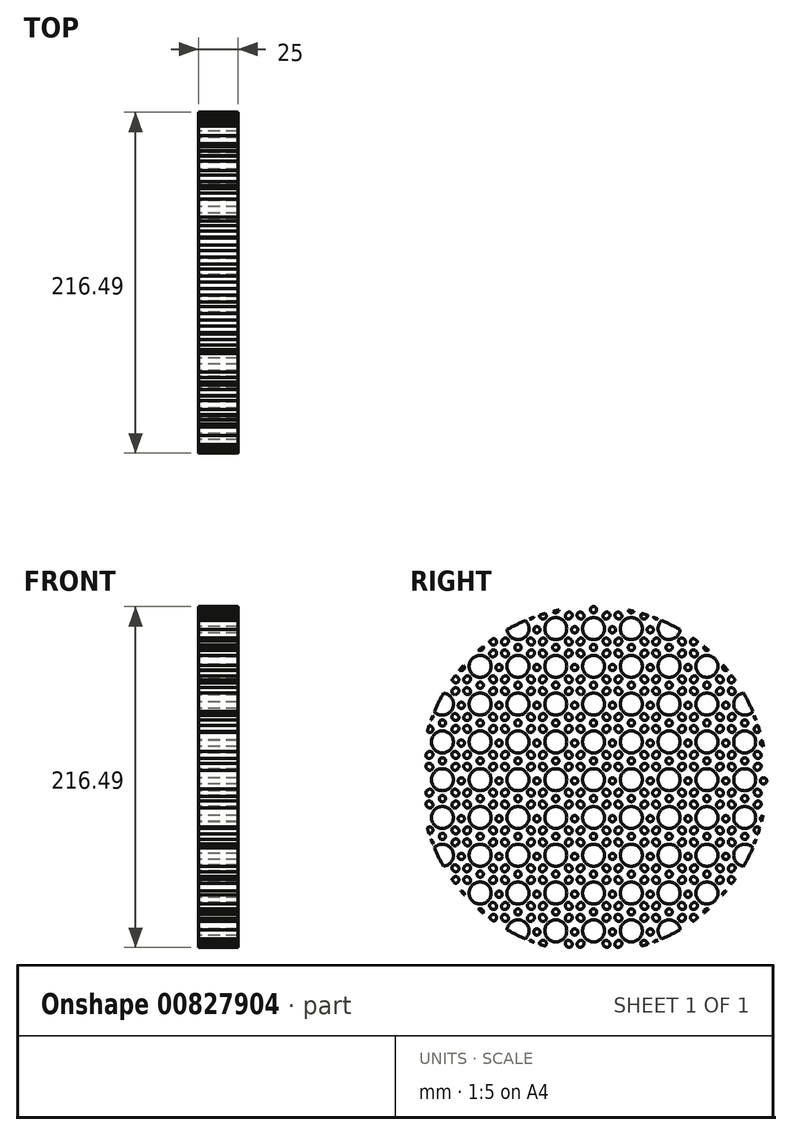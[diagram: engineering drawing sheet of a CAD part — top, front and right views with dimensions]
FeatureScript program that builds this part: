
annotation { "Feature Type Name" : "Feature", "Feature Type Description" : "" }
export const myFeature = defineFeature(function(context is Context, id is Id, definition is map)
    precondition{}
    {
        {
            var Q0;
            Q0=qCreatedBy(makeId("Right.planeOp"),FACE);
            var sketch = newSketch(context, id + "F0", { "sketchPlane" : qUnion([Q0])});
            skCircle(sketch, "E0.0", {"center": v(0, 0) * mm, "radius": 7 * mm});
            skArc(sketch, "E1.0", {"start": v(6.59, 9.41) * mm, "mid": v(6.59, 6.59) * mm, "end": v(9.41, 6.59) * mm});
            skArc(sketch, "E2.0", {"start": v(9.9, 7.07) * mm, "mid": v(9.9, 9.9) * mm, "end": v(7.07, 9.9) * mm});
            skCircle(sketch, "E3.0", {"center": v(0, 12) * mm, "radius": 2 * mm});
            skArc(sketch, "E4.0.0", {"start": v(-9.9, 7.07) * mm, "mid": v(-9.9, 9.9) * mm, "end": v(-7.07, 9.9) * mm});
            skArc(sketch, "E5.0", {"start": v(-9.41, 6.59) * mm, "mid": v(-6.59, 6.59) * mm, "end": v(-6.59, 9.41) * mm});
            skArc(sketch, "E6.0", {"start": v(-9.9, -7.07) * mm, "mid": v(-9.9, -9.9) * mm, "end": v(-7.07, -9.9) * mm});
            skArc(sketch, "E7.0", {"start": v(-6.59, -9.41) * mm, "mid": v(-6.59, -6.59) * mm, "end": v(-9.41, -6.59) * mm});
            skArc(sketch, "E8.0", {"start": v(9.41, -6.59) * mm, "mid": v(6.59, -6.59) * mm, "end": v(6.59, -9.41) * mm});
            skArc(sketch, "E9.0", {"start": v(7.07, -9.9) * mm, "mid": v(9.9, -9.9) * mm, "end": v(9.9, -7.07) * mm});
            skLineSegment(sketch, "E10", {"start": v(7.07, 9.9) * mm, "end": v(6.59, 9.41) * mm});
            skLineSegment(sketch, "E11", {"start": v(9.9, 7.07) * mm, "end": v(9.41, 6.59) * mm});
            skLineSegment(sketch, "E12", {"start": v(-7.07, 9.9) * mm, "end": v(-6.59, 9.41) * mm});
            skLineSegment(sketch, "E13", {"start": v(-9.9, 7.07) * mm, "end": v(-9.41, 6.59) * mm});
            skLineSegment(sketch, "E14", {"start": v(-9.41, -6.59) * mm, "end": v(-9.9, -7.07) * mm});
            skLineSegment(sketch, "E15", {"start": v(-7.07, -9.9) * mm, "end": v(-6.59, -9.41) * mm});
            skLineSegment(sketch, "E16", {"start": v(9.41, -6.59) * mm, "end": v(9.9, -7.07) * mm});
            skLineSegment(sketch, "E17", {"start": v(7.07, -9.9) * mm, "end": v(6.59, -9.41) * mm});
            skCircle(sketch, "E18", {"center": v(12, -0.75) * mm, "radius": 2 * mm});
            skCircle(sketch, "E19.0.1.0", {"center": v(12, 23.25) * mm, "radius": 2 * mm});
            skArc(sketch, "E19.0.1.1", {"start": v(9.41, 17.41) * mm, "mid": v(6.59, 17.41) * mm, "end": v(6.59, 14.59) * mm});
            skArc(sketch, "E19.0.1.2", {"start": v(-9.9, 31.07) * mm, "mid": v(-9.9, 33.9) * mm, "end": v(-7.07, 33.9) * mm});
            skArc(sketch, "E19.0.1.3", {"start": v(-6.59, 14.59) * mm, "mid": v(-6.59, 17.41) * mm, "end": v(-9.41, 17.41) * mm});
            skCircle(sketch, "E19.0.1.4", {"center": v(0, 36) * mm, "radius": 2 * mm});
            skArc(sketch, "E19.0.1.5", {"start": v(6.59, 33.41) * mm, "mid": v(6.59, 30.59) * mm, "end": v(9.41, 30.59) * mm});
            skArc(sketch, "E19.0.1.6", {"start": v(-9.41, 30.59) * mm, "mid": v(-6.59, 30.59) * mm, "end": v(-6.59, 33.41) * mm});
            skCircle(sketch, "E19.0.1.7", {"center": v(0, 24) * mm, "radius": 7 * mm});
            skArc(sketch, "E19.0.1.8", {"start": v(9.9, 31.07) * mm, "mid": v(9.9, 33.9) * mm, "end": v(7.07, 33.9) * mm});
            skArc(sketch, "E19.0.1.9", {"start": v(7.07, 14.1) * mm, "mid": v(9.9, 14.1) * mm, "end": v(9.9, 16.93) * mm});
            skArc(sketch, "E19.0.1.10", {"start": v(-9.9, 16.93) * mm, "mid": v(-9.9, 14.1) * mm, "end": v(-7.07, 14.1) * mm});
            skLineSegment(sketch, "E19.0.1.11", {"start": v(7.07, 14.1) * mm, "end": v(6.59, 14.59) * mm});
            skLineSegment(sketch, "E19.0.1.12", {"start": v(-7.07, 33.9) * mm, "end": v(-6.59, 33.41) * mm});
            skLineSegment(sketch, "E19.0.1.13", {"start": v(9.9, 31.07) * mm, "end": v(9.41, 30.59) * mm});
            skLineSegment(sketch, "E19.0.1.14", {"start": v(9.41, 17.41) * mm, "end": v(9.9, 16.93) * mm});
            skLineSegment(sketch, "E19.0.1.15", {"start": v(7.07, 33.9) * mm, "end": v(6.59, 33.41) * mm});
            skLineSegment(sketch, "E19.0.1.16", {"start": v(-9.9, 31.07) * mm, "end": v(-9.41, 30.59) * mm});
            skLineSegment(sketch, "E19.0.1.17", {"start": v(-9.41, 17.41) * mm, "end": v(-9.9, 16.93) * mm});
            skLineSegment(sketch, "E19.0.1.18", {"start": v(-7.07, 14.1) * mm, "end": v(-6.59, 14.59) * mm});
            skCircle(sketch, "E19.0.2.0", {"center": v(12, 47.25) * mm, "radius": 2 * mm});
            skArc(sketch, "E19.0.2.1", {"start": v(9.41, 41.41) * mm, "mid": v(6.59, 41.41) * mm, "end": v(6.59, 38.59) * mm});
            skArc(sketch, "E19.0.2.2", {"start": v(-9.9, 55.07) * mm, "mid": v(-9.9, 57.9) * mm, "end": v(-7.07, 57.9) * mm});
            skArc(sketch, "E19.0.2.3", {"start": v(-6.59, 38.59) * mm, "mid": v(-6.59, 41.41) * mm, "end": v(-9.41, 41.41) * mm});
            skCircle(sketch, "E19.0.2.4", {"center": v(0, 60) * mm, "radius": 2 * mm});
            skArc(sketch, "E19.0.2.5", {"start": v(6.59, 57.41) * mm, "mid": v(6.59, 54.59) * mm, "end": v(9.41, 54.59) * mm});
            skArc(sketch, "E19.0.2.6", {"start": v(-9.41, 54.59) * mm, "mid": v(-6.59, 54.59) * mm, "end": v(-6.59, 57.41) * mm});
            skCircle(sketch, "E19.0.2.7", {"center": v(0, 48) * mm, "radius": 7 * mm});
            skArc(sketch, "E19.0.2.8", {"start": v(9.9, 55.07) * mm, "mid": v(9.9, 57.9) * mm, "end": v(7.07, 57.9) * mm});
            skArc(sketch, "E19.0.2.9", {"start": v(7.07, 38.1) * mm, "mid": v(9.9, 38.1) * mm, "end": v(9.9, 40.93) * mm});
            skArc(sketch, "E19.0.2.10", {"start": v(-9.9, 40.93) * mm, "mid": v(-9.9, 38.1) * mm, "end": v(-7.07, 38.1) * mm});
            skLineSegment(sketch, "E19.0.2.11", {"start": v(7.07, 38.1) * mm, "end": v(6.59, 38.59) * mm});
            skLineSegment(sketch, "E19.0.2.12", {"start": v(-7.07, 57.9) * mm, "end": v(-6.59, 57.41) * mm});
            skLineSegment(sketch, "E19.0.2.13", {"start": v(9.9, 55.07) * mm, "end": v(9.41, 54.59) * mm});
            skLineSegment(sketch, "E19.0.2.14", {"start": v(9.41, 41.41) * mm, "end": v(9.9, 40.93) * mm});
            skLineSegment(sketch, "E19.0.2.15", {"start": v(7.07, 57.9) * mm, "end": v(6.59, 57.41) * mm});
            skLineSegment(sketch, "E19.0.2.16", {"start": v(-9.9, 55.07) * mm, "end": v(-9.41, 54.59) * mm});
            skLineSegment(sketch, "E19.0.2.17", {"start": v(-9.41, 41.41) * mm, "end": v(-9.9, 40.93) * mm});
            skLineSegment(sketch, "E19.0.2.18", {"start": v(-7.07, 38.1) * mm, "end": v(-6.59, 38.59) * mm});
            skCircle(sketch, "E19.0.3.0", {"center": v(12, 71.25) * mm, "radius": 2 * mm});
            skArc(sketch, "E19.0.3.1", {"start": v(9.41, 65.41) * mm, "mid": v(6.59, 65.41) * mm, "end": v(6.59, 62.59) * mm});
            skArc(sketch, "E19.0.3.2", {"start": v(-9.9, 79.07) * mm, "mid": v(-9.9, 81.9) * mm, "end": v(-7.07, 81.9) * mm});
            skArc(sketch, "E19.0.3.3", {"start": v(-6.59, 62.59) * mm, "mid": v(-6.59, 65.41) * mm, "end": v(-9.41, 65.41) * mm});
            skCircle(sketch, "E19.0.3.4", {"center": v(0, 84) * mm, "radius": 2 * mm});
            skArc(sketch, "E19.0.3.5", {"start": v(6.59, 81.41) * mm, "mid": v(6.59, 78.59) * mm, "end": v(9.41, 78.59) * mm});
            skArc(sketch, "E19.0.3.6", {"start": v(-9.41, 78.59) * mm, "mid": v(-6.59, 78.59) * mm, "end": v(-6.59, 81.41) * mm});
            skCircle(sketch, "E19.0.3.7", {"center": v(0, 72) * mm, "radius": 7 * mm});
            skArc(sketch, "E19.0.3.8", {"start": v(9.9, 79.07) * mm, "mid": v(9.9, 81.9) * mm, "end": v(7.07, 81.9) * mm});
            skArc(sketch, "E19.0.3.9", {"start": v(7.07, 62.1) * mm, "mid": v(9.9, 62.1) * mm, "end": v(9.9, 64.93) * mm});
            skArc(sketch, "E19.0.3.10", {"start": v(-9.9, 64.93) * mm, "mid": v(-9.9, 62.1) * mm, "end": v(-7.07, 62.1) * mm});
            skLineSegment(sketch, "E19.0.3.11", {"start": v(7.07, 62.1) * mm, "end": v(6.59, 62.59) * mm});
            skLineSegment(sketch, "E19.0.3.12", {"start": v(-7.07, 81.9) * mm, "end": v(-6.59, 81.41) * mm});
            skLineSegment(sketch, "E19.0.3.13", {"start": v(9.9, 79.07) * mm, "end": v(9.41, 78.59) * mm});
            skLineSegment(sketch, "E19.0.3.14", {"start": v(9.41, 65.41) * mm, "end": v(9.9, 64.93) * mm});
            skLineSegment(sketch, "E19.0.3.15", {"start": v(7.07, 81.9) * mm, "end": v(6.59, 81.41) * mm});
            skLineSegment(sketch, "E19.0.3.16", {"start": v(-9.9, 79.07) * mm, "end": v(-9.41, 78.59) * mm});
            skLineSegment(sketch, "E19.0.3.17", {"start": v(-9.41, 65.41) * mm, "end": v(-9.9, 64.93) * mm});
            skLineSegment(sketch, "E19.0.3.18", {"start": v(-7.07, 62.1) * mm, "end": v(-6.59, 62.59) * mm});
            skCircle(sketch, "E19.0.4.0", {"center": v(12, 95.25) * mm, "radius": 2 * mm});
            skArc(sketch, "E19.0.4.1", {"start": v(9.41, 89.41) * mm, "mid": v(6.59, 89.41) * mm, "end": v(6.59, 86.59) * mm});
            skArc(sketch, "E19.0.4.2", {"start": v(-9.9, 103.07) * mm, "mid": v(-9.9, 105.9) * mm, "end": v(-7.07, 105.9) * mm});
            skArc(sketch, "E19.0.4.3", {"start": v(-6.59, 86.59) * mm, "mid": v(-6.59, 89.41) * mm, "end": v(-9.41, 89.41) * mm});
            skCircle(sketch, "E19.0.4.4", {"center": v(0, 108) * mm, "radius": 2 * mm});
            skArc(sketch, "E19.0.4.5", {"start": v(6.59, 105.41) * mm, "mid": v(6.59, 102.59) * mm, "end": v(9.41, 102.59) * mm});
            skArc(sketch, "E19.0.4.6", {"start": v(-9.41, 102.59) * mm, "mid": v(-6.59, 102.59) * mm, "end": v(-6.59, 105.41) * mm});
            skCircle(sketch, "E19.0.4.7", {"center": v(0, 96) * mm, "radius": 7 * mm});
            skArc(sketch, "E19.0.4.8", {"start": v(9.9, 103.07) * mm, "mid": v(9.9, 105.9) * mm, "end": v(7.07, 105.9) * mm});
            skArc(sketch, "E19.0.4.9", {"start": v(7.07, 86.1) * mm, "mid": v(9.9, 86.1) * mm, "end": v(9.9, 88.93) * mm});
            skArc(sketch, "E19.0.4.10", {"start": v(-9.9, 88.93) * mm, "mid": v(-9.9, 86.1) * mm, "end": v(-7.07, 86.1) * mm});
            skLineSegment(sketch, "E19.0.4.11", {"start": v(7.07, 86.1) * mm, "end": v(6.59, 86.59) * mm});
            skLineSegment(sketch, "E19.0.4.12", {"start": v(-7.07, 105.9) * mm, "end": v(-6.59, 105.41) * mm});
            skLineSegment(sketch, "E19.0.4.13", {"start": v(9.9, 103.07) * mm, "end": v(9.41, 102.59) * mm});
            skLineSegment(sketch, "E19.0.4.14", {"start": v(9.41, 89.41) * mm, "end": v(9.9, 88.93) * mm});
            skLineSegment(sketch, "E19.0.4.15", {"start": v(7.07, 105.9) * mm, "end": v(6.59, 105.41) * mm});
            skLineSegment(sketch, "E19.0.4.16", {"start": v(-9.9, 103.07) * mm, "end": v(-9.41, 102.59) * mm});
            skLineSegment(sketch, "E19.0.4.17", {"start": v(-9.41, 89.41) * mm, "end": v(-9.9, 88.93) * mm});
            skLineSegment(sketch, "E19.0.4.18", {"start": v(-7.07, 86.1) * mm, "end": v(-6.59, 86.59) * mm});
            skCircle(sketch, "E19.0.5.0", {"center": v(12, 119.25) * mm, "radius": 2 * mm});
            skArc(sketch, "E19.0.5.1", {"start": v(9.41, 113.41) * mm, "mid": v(6.59, 113.41) * mm, "end": v(6.59, 110.59) * mm});
            skArc(sketch, "E19.0.5.2", {"start": v(-9.9, 127.07) * mm, "mid": v(-9.9, 129.9) * mm, "end": v(-7.07, 129.9) * mm});
            skArc(sketch, "E19.0.5.3", {"start": v(-6.59, 110.59) * mm, "mid": v(-6.59, 113.41) * mm, "end": v(-9.41, 113.41) * mm});
            skCircle(sketch, "E19.0.5.4", {"center": v(0, 132) * mm, "radius": 2 * mm});
            skArc(sketch, "E19.0.5.5", {"start": v(6.59, 129.41) * mm, "mid": v(6.59, 126.59) * mm, "end": v(9.41, 126.59) * mm});
            skArc(sketch, "E19.0.5.6", {"start": v(-9.41, 126.59) * mm, "mid": v(-6.59, 126.59) * mm, "end": v(-6.59, 129.41) * mm});
            skCircle(sketch, "E19.0.5.7", {"center": v(0, 120) * mm, "radius": 7 * mm});
            skArc(sketch, "E19.0.5.8", {"start": v(9.9, 127.07) * mm, "mid": v(9.9, 129.9) * mm, "end": v(7.07, 129.9) * mm});
            skArc(sketch, "E19.0.5.9", {"start": v(7.07, 110.1) * mm, "mid": v(9.9, 110.1) * mm, "end": v(9.9, 112.93) * mm});
            skArc(sketch, "E19.0.5.10", {"start": v(-9.9, 112.93) * mm, "mid": v(-9.9, 110.1) * mm, "end": v(-7.07, 110.1) * mm});
            skLineSegment(sketch, "E19.0.5.11", {"start": v(7.07, 110.1) * mm, "end": v(6.59, 110.59) * mm});
            skLineSegment(sketch, "E19.0.5.12", {"start": v(-7.07, 129.9) * mm, "end": v(-6.59, 129.41) * mm});
            skLineSegment(sketch, "E19.0.5.13", {"start": v(9.9, 127.07) * mm, "end": v(9.41, 126.59) * mm});
            skLineSegment(sketch, "E19.0.5.14", {"start": v(9.41, 113.41) * mm, "end": v(9.9, 112.93) * mm});
            skLineSegment(sketch, "E19.0.5.15", {"start": v(7.07, 129.9) * mm, "end": v(6.59, 129.41) * mm});
            skLineSegment(sketch, "E19.0.5.16", {"start": v(-9.9, 127.07) * mm, "end": v(-9.41, 126.59) * mm});
            skLineSegment(sketch, "E19.0.5.17", {"start": v(-9.41, 113.41) * mm, "end": v(-9.9, 112.93) * mm});
            skLineSegment(sketch, "E19.0.5.18", {"start": v(-7.07, 110.1) * mm, "end": v(-6.59, 110.59) * mm});
            skCircle(sketch, "E19.0.6.0", {"center": v(12, 143.25) * mm, "radius": 2 * mm});
            skArc(sketch, "E19.0.6.1", {"start": v(9.41, 137.41) * mm, "mid": v(6.59, 137.41) * mm, "end": v(6.59, 134.59) * mm});
            skArc(sketch, "E19.0.6.2", {"start": v(-9.9, 151.07) * mm, "mid": v(-9.9, 153.9) * mm, "end": v(-7.07, 153.9) * mm});
            skArc(sketch, "E19.0.6.3", {"start": v(-6.59, 134.59) * mm, "mid": v(-6.59, 137.41) * mm, "end": v(-9.41, 137.41) * mm});
            skCircle(sketch, "E19.0.6.4", {"center": v(0, 156) * mm, "radius": 2 * mm});
            skArc(sketch, "E19.0.6.5", {"start": v(6.59, 153.41) * mm, "mid": v(6.59, 150.59) * mm, "end": v(9.41, 150.59) * mm});
            skArc(sketch, "E19.0.6.6", {"start": v(-9.41, 150.59) * mm, "mid": v(-6.59, 150.59) * mm, "end": v(-6.59, 153.41) * mm});
            skCircle(sketch, "E19.0.6.7", {"center": v(0, 144) * mm, "radius": 7 * mm});
            skArc(sketch, "E19.0.6.8", {"start": v(9.9, 151.07) * mm, "mid": v(9.9, 153.9) * mm, "end": v(7.07, 153.9) * mm});
            skArc(sketch, "E19.0.6.9", {"start": v(7.07, 134.1) * mm, "mid": v(9.9, 134.1) * mm, "end": v(9.9, 136.93) * mm});
            skArc(sketch, "E19.0.6.10", {"start": v(-9.9, 136.93) * mm, "mid": v(-9.9, 134.1) * mm, "end": v(-7.07, 134.1) * mm});
            skLineSegment(sketch, "E19.0.6.11", {"start": v(7.07, 134.1) * mm, "end": v(6.59, 134.59) * mm});
            skLineSegment(sketch, "E19.0.6.12", {"start": v(-7.07, 153.9) * mm, "end": v(-6.59, 153.41) * mm});
            skLineSegment(sketch, "E19.0.6.13", {"start": v(9.9, 151.07) * mm, "end": v(9.41, 150.59) * mm});
            skLineSegment(sketch, "E19.0.6.14", {"start": v(9.41, 137.41) * mm, "end": v(9.9, 136.93) * mm});
            skLineSegment(sketch, "E19.0.6.15", {"start": v(7.07, 153.9) * mm, "end": v(6.59, 153.41) * mm});
            skLineSegment(sketch, "E19.0.6.16", {"start": v(-9.9, 151.07) * mm, "end": v(-9.41, 150.59) * mm});
            skLineSegment(sketch, "E19.0.6.17", {"start": v(-9.41, 137.41) * mm, "end": v(-9.9, 136.93) * mm});
            skLineSegment(sketch, "E19.0.6.18", {"start": v(-7.07, 134.1) * mm, "end": v(-6.59, 134.59) * mm});
            skCircle(sketch, "E19.0.7.0", {"center": v(12, 167.25) * mm, "radius": 2 * mm});
            skArc(sketch, "E19.0.7.1", {"start": v(9.41, 161.41) * mm, "mid": v(6.59, 161.41) * mm, "end": v(6.59, 158.59) * mm});
            skArc(sketch, "E19.0.7.2", {"start": v(-9.9, 175.07) * mm, "mid": v(-9.9, 177.9) * mm, "end": v(-7.07, 177.9) * mm});
            skArc(sketch, "E19.0.7.3", {"start": v(-6.59, 158.59) * mm, "mid": v(-6.59, 161.41) * mm, "end": v(-9.41, 161.41) * mm});
            skCircle(sketch, "E19.0.7.4", {"center": v(0, 180) * mm, "radius": 2 * mm});
            skArc(sketch, "E19.0.7.5", {"start": v(6.59, 177.41) * mm, "mid": v(6.59, 174.59) * mm, "end": v(9.41, 174.59) * mm});
            skArc(sketch, "E19.0.7.6", {"start": v(-9.41, 174.59) * mm, "mid": v(-6.59, 174.59) * mm, "end": v(-6.59, 177.41) * mm});
            skCircle(sketch, "E19.0.7.7", {"center": v(0, 168) * mm, "radius": 7 * mm});
            skArc(sketch, "E19.0.7.8", {"start": v(9.9, 175.07) * mm, "mid": v(9.9, 177.9) * mm, "end": v(7.07, 177.9) * mm});
            skArc(sketch, "E19.0.7.9", {"start": v(7.07, 158.1) * mm, "mid": v(9.9, 158.1) * mm, "end": v(9.9, 160.93) * mm});
            skArc(sketch, "E19.0.7.10", {"start": v(-9.9, 160.93) * mm, "mid": v(-9.9, 158.1) * mm, "end": v(-7.07, 158.1) * mm});
            skLineSegment(sketch, "E19.0.7.11", {"start": v(7.07, 158.1) * mm, "end": v(6.59, 158.59) * mm});
            skLineSegment(sketch, "E19.0.7.12", {"start": v(-7.07, 177.9) * mm, "end": v(-6.59, 177.41) * mm});
            skLineSegment(sketch, "E19.0.7.13", {"start": v(9.9, 175.07) * mm, "end": v(9.41, 174.59) * mm});
            skLineSegment(sketch, "E19.0.7.14", {"start": v(9.41, 161.41) * mm, "end": v(9.9, 160.93) * mm});
            skLineSegment(sketch, "E19.0.7.15", {"start": v(7.07, 177.9) * mm, "end": v(6.59, 177.41) * mm});
            skLineSegment(sketch, "E19.0.7.16", {"start": v(-9.9, 175.07) * mm, "end": v(-9.41, 174.59) * mm});
            skLineSegment(sketch, "E19.0.7.17", {"start": v(-9.41, 161.41) * mm, "end": v(-9.9, 160.93) * mm});
            skLineSegment(sketch, "E19.0.7.18", {"start": v(-7.07, 158.1) * mm, "end": v(-6.59, 158.59) * mm});
            skCircle(sketch, "E19.0.8.0", {"center": v(12, 191.25) * mm, "radius": 2 * mm});
            skArc(sketch, "E19.0.8.1", {"start": v(9.41, 185.41) * mm, "mid": v(6.59, 185.41) * mm, "end": v(6.59, 182.59) * mm});
            skArc(sketch, "E19.0.8.2", {"start": v(-9.9, 199.07) * mm, "mid": v(-9.9, 201.9) * mm, "end": v(-7.07, 201.9) * mm});
            skArc(sketch, "E19.0.8.3", {"start": v(-6.59, 182.59) * mm, "mid": v(-6.59, 185.41) * mm, "end": v(-9.41, 185.41) * mm});
            skCircle(sketch, "E19.0.8.4", {"center": v(0, 204) * mm, "radius": 2 * mm});
            skArc(sketch, "E19.0.8.5", {"start": v(6.59, 201.41) * mm, "mid": v(6.59, 198.59) * mm, "end": v(9.41, 198.59) * mm});
            skArc(sketch, "E19.0.8.6", {"start": v(-9.41, 198.59) * mm, "mid": v(-6.59, 198.59) * mm, "end": v(-6.59, 201.41) * mm});
            skCircle(sketch, "E19.0.8.7", {"center": v(0, 192) * mm, "radius": 7 * mm});
            skArc(sketch, "E19.0.8.8", {"start": v(9.9, 199.07) * mm, "mid": v(9.9, 201.9) * mm, "end": v(7.07, 201.9) * mm});
            skArc(sketch, "E19.0.8.9", {"start": v(7.07, 182.1) * mm, "mid": v(9.9, 182.1) * mm, "end": v(9.9, 184.93) * mm});
            skArc(sketch, "E19.0.8.10", {"start": v(-9.9, 184.93) * mm, "mid": v(-9.9, 182.1) * mm, "end": v(-7.07, 182.1) * mm});
            skLineSegment(sketch, "E19.0.8.11", {"start": v(7.07, 182.1) * mm, "end": v(6.59, 182.59) * mm});
            skLineSegment(sketch, "E19.0.8.12", {"start": v(-7.07, 201.9) * mm, "end": v(-6.59, 201.41) * mm});
            skLineSegment(sketch, "E19.0.8.13", {"start": v(9.9, 199.07) * mm, "end": v(9.41, 198.59) * mm});
            skLineSegment(sketch, "E19.0.8.14", {"start": v(9.41, 185.41) * mm, "end": v(9.9, 184.93) * mm});
            skLineSegment(sketch, "E19.0.8.15", {"start": v(7.07, 201.9) * mm, "end": v(6.59, 201.41) * mm});
            skLineSegment(sketch, "E19.0.8.16", {"start": v(-9.9, 199.07) * mm, "end": v(-9.41, 198.59) * mm});
            skLineSegment(sketch, "E19.0.8.17", {"start": v(-9.41, 185.41) * mm, "end": v(-9.9, 184.93) * mm});
            skLineSegment(sketch, "E19.0.8.18", {"start": v(-7.07, 182.1) * mm, "end": v(-6.59, 182.59) * mm});
            skCircle(sketch, "E19.1.0.0", {"center": v(36, -0.75) * mm, "radius": 2 * mm});
            skArc(sketch, "E19.1.0.1", {"start": v(33.41, -6.59) * mm, "mid": v(30.59, -6.59) * mm, "end": v(30.59, -9.41) * mm});
            skArc(sketch, "E19.1.0.2", {"start": v(14.1, 7.07) * mm, "mid": v(14.1, 9.9) * mm, "end": v(16.93, 9.9) * mm});
            skArc(sketch, "E19.1.0.3", {"start": v(17.41, -9.41) * mm, "mid": v(17.41, -6.59) * mm, "end": v(14.59, -6.59) * mm});
            skCircle(sketch, "E19.1.0.4", {"center": v(24, 12) * mm, "radius": 2 * mm});
            skArc(sketch, "E19.1.0.5", {"start": v(30.59, 9.41) * mm, "mid": v(30.59, 6.59) * mm, "end": v(33.41, 6.59) * mm});
            skArc(sketch, "E19.1.0.6", {"start": v(14.59, 6.59) * mm, "mid": v(17.41, 6.59) * mm, "end": v(17.41, 9.41) * mm});
            skCircle(sketch, "E19.1.0.7", {"center": v(24, 0) * mm, "radius": 7 * mm});
            skArc(sketch, "E19.1.0.8", {"start": v(33.9, 7.07) * mm, "mid": v(33.9, 9.9) * mm, "end": v(31.07, 9.9) * mm});
            skArc(sketch, "E19.1.0.9", {"start": v(31.07, -9.9) * mm, "mid": v(33.9, -9.9) * mm, "end": v(33.9, -7.07) * mm});
            skArc(sketch, "E19.1.0.10", {"start": v(14.1, -7.07) * mm, "mid": v(14.1, -9.9) * mm, "end": v(16.93, -9.9) * mm});
            skLineSegment(sketch, "E19.1.0.11", {"start": v(31.07, -9.9) * mm, "end": v(30.59, -9.41) * mm});
            skLineSegment(sketch, "E19.1.0.12", {"start": v(16.93, 9.9) * mm, "end": v(17.41, 9.41) * mm});
            skLineSegment(sketch, "E19.1.0.13", {"start": v(33.9, 7.07) * mm, "end": v(33.41, 6.59) * mm});
            skLineSegment(sketch, "E19.1.0.14", {"start": v(33.41, -6.59) * mm, "end": v(33.9, -7.07) * mm});
            skLineSegment(sketch, "E19.1.0.15", {"start": v(31.07, 9.9) * mm, "end": v(30.59, 9.41) * mm});
            skLineSegment(sketch, "E19.1.0.16", {"start": v(14.1, 7.07) * mm, "end": v(14.59, 6.59) * mm});
            skLineSegment(sketch, "E19.1.0.17", {"start": v(14.59, -6.59) * mm, "end": v(14.1, -7.07) * mm});
            skLineSegment(sketch, "E19.1.0.18", {"start": v(16.93, -9.9) * mm, "end": v(17.41, -9.41) * mm});
            skCircle(sketch, "E19.1.1.0", {"center": v(36, 23.25) * mm, "radius": 2 * mm});
            skArc(sketch, "E19.1.1.1", {"start": v(33.41, 17.41) * mm, "mid": v(30.59, 17.41) * mm, "end": v(30.59, 14.59) * mm});
            skArc(sketch, "E19.1.1.2", {"start": v(14.1, 31.07) * mm, "mid": v(14.1, 33.9) * mm, "end": v(16.93, 33.9) * mm});
            skArc(sketch, "E19.1.1.3", {"start": v(17.41, 14.59) * mm, "mid": v(17.41, 17.41) * mm, "end": v(14.59, 17.41) * mm});
            skCircle(sketch, "E19.1.1.4", {"center": v(24, 36) * mm, "radius": 2 * mm});
            skArc(sketch, "E19.1.1.5", {"start": v(30.59, 33.41) * mm, "mid": v(30.59, 30.59) * mm, "end": v(33.41, 30.59) * mm});
            skArc(sketch, "E19.1.1.6", {"start": v(14.59, 30.59) * mm, "mid": v(17.41, 30.59) * mm, "end": v(17.41, 33.41) * mm});
            skCircle(sketch, "E19.1.1.7", {"center": v(24, 24) * mm, "radius": 7 * mm});
            skArc(sketch, "E19.1.1.8", {"start": v(33.9, 31.07) * mm, "mid": v(33.9, 33.9) * mm, "end": v(31.07, 33.9) * mm});
            skArc(sketch, "E19.1.1.9", {"start": v(31.07, 14.1) * mm, "mid": v(33.9, 14.1) * mm, "end": v(33.9, 16.93) * mm});
            skArc(sketch, "E19.1.1.10", {"start": v(14.1, 16.93) * mm, "mid": v(14.1, 14.1) * mm, "end": v(16.93, 14.1) * mm});
            skLineSegment(sketch, "E19.1.1.11", {"start": v(31.07, 14.1) * mm, "end": v(30.59, 14.59) * mm});
            skLineSegment(sketch, "E19.1.1.12", {"start": v(16.93, 33.9) * mm, "end": v(17.41, 33.41) * mm});
            skLineSegment(sketch, "E19.1.1.13", {"start": v(33.9, 31.07) * mm, "end": v(33.41, 30.59) * mm});
            skLineSegment(sketch, "E19.1.1.14", {"start": v(33.41, 17.41) * mm, "end": v(33.9, 16.93) * mm});
            skLineSegment(sketch, "E19.1.1.15", {"start": v(31.07, 33.9) * mm, "end": v(30.59, 33.41) * mm});
            skLineSegment(sketch, "E19.1.1.16", {"start": v(14.1, 31.07) * mm, "end": v(14.59, 30.59) * mm});
            skLineSegment(sketch, "E19.1.1.17", {"start": v(14.59, 17.41) * mm, "end": v(14.1, 16.93) * mm});
            skLineSegment(sketch, "E19.1.1.18", {"start": v(16.93, 14.1) * mm, "end": v(17.41, 14.59) * mm});
            skCircle(sketch, "E19.1.2.0", {"center": v(36, 47.25) * mm, "radius": 2 * mm});
            skArc(sketch, "E19.1.2.1", {"start": v(33.41, 41.41) * mm, "mid": v(30.59, 41.41) * mm, "end": v(30.59, 38.59) * mm});
            skArc(sketch, "E19.1.2.2", {"start": v(14.1, 55.07) * mm, "mid": v(14.1, 57.9) * mm, "end": v(16.93, 57.9) * mm});
            skArc(sketch, "E19.1.2.3", {"start": v(17.41, 38.59) * mm, "mid": v(17.41, 41.41) * mm, "end": v(14.59, 41.41) * mm});
            skCircle(sketch, "E19.1.2.4", {"center": v(24, 60) * mm, "radius": 2 * mm});
            skArc(sketch, "E19.1.2.5", {"start": v(30.59, 57.41) * mm, "mid": v(30.59, 54.59) * mm, "end": v(33.41, 54.59) * mm});
            skArc(sketch, "E19.1.2.6", {"start": v(14.59, 54.59) * mm, "mid": v(17.41, 54.59) * mm, "end": v(17.41, 57.41) * mm});
            skCircle(sketch, "E19.1.2.7", {"center": v(24, 48) * mm, "radius": 7 * mm});
            skArc(sketch, "E19.1.2.8", {"start": v(33.9, 55.07) * mm, "mid": v(33.9, 57.9) * mm, "end": v(31.07, 57.9) * mm});
            skArc(sketch, "E19.1.2.9", {"start": v(31.07, 38.1) * mm, "mid": v(33.9, 38.1) * mm, "end": v(33.9, 40.93) * mm});
            skArc(sketch, "E19.1.2.10", {"start": v(14.1, 40.93) * mm, "mid": v(14.1, 38.1) * mm, "end": v(16.93, 38.1) * mm});
            skLineSegment(sketch, "E19.1.2.11", {"start": v(31.07, 38.1) * mm, "end": v(30.59, 38.59) * mm});
            skLineSegment(sketch, "E19.1.2.12", {"start": v(16.93, 57.9) * mm, "end": v(17.41, 57.41) * mm});
            skLineSegment(sketch, "E19.1.2.13", {"start": v(33.9, 55.07) * mm, "end": v(33.41, 54.59) * mm});
            skLineSegment(sketch, "E19.1.2.14", {"start": v(33.41, 41.41) * mm, "end": v(33.9, 40.93) * mm});
            skLineSegment(sketch, "E19.1.2.15", {"start": v(31.07, 57.9) * mm, "end": v(30.59, 57.41) * mm});
            skLineSegment(sketch, "E19.1.2.16", {"start": v(14.1, 55.07) * mm, "end": v(14.59, 54.59) * mm});
            skLineSegment(sketch, "E19.1.2.17", {"start": v(14.59, 41.41) * mm, "end": v(14.1, 40.93) * mm});
            skLineSegment(sketch, "E19.1.2.18", {"start": v(16.93, 38.1) * mm, "end": v(17.41, 38.59) * mm});
            skCircle(sketch, "E19.1.3.0", {"center": v(36, 71.25) * mm, "radius": 2 * mm});
            skArc(sketch, "E19.1.3.1", {"start": v(33.41, 65.41) * mm, "mid": v(30.59, 65.41) * mm, "end": v(30.59, 62.59) * mm});
            skArc(sketch, "E19.1.3.2", {"start": v(14.1, 79.07) * mm, "mid": v(14.1, 81.9) * mm, "end": v(16.93, 81.9) * mm});
            skArc(sketch, "E19.1.3.3", {"start": v(17.41, 62.59) * mm, "mid": v(17.41, 65.41) * mm, "end": v(14.59, 65.41) * mm});
            skCircle(sketch, "E19.1.3.4", {"center": v(24, 84) * mm, "radius": 2 * mm});
            skArc(sketch, "E19.1.3.5", {"start": v(30.59, 81.41) * mm, "mid": v(30.59, 78.59) * mm, "end": v(33.41, 78.59) * mm});
            skArc(sketch, "E19.1.3.6", {"start": v(14.59, 78.59) * mm, "mid": v(17.41, 78.59) * mm, "end": v(17.41, 81.41) * mm});
            skCircle(sketch, "E19.1.3.7", {"center": v(24, 72) * mm, "radius": 7 * mm});
            skArc(sketch, "E19.1.3.8", {"start": v(33.9, 79.07) * mm, "mid": v(33.9, 81.9) * mm, "end": v(31.07, 81.9) * mm});
            skArc(sketch, "E19.1.3.9", {"start": v(31.07, 62.1) * mm, "mid": v(33.9, 62.1) * mm, "end": v(33.9, 64.93) * mm});
            skArc(sketch, "E19.1.3.10", {"start": v(14.1, 64.93) * mm, "mid": v(14.1, 62.1) * mm, "end": v(16.93, 62.1) * mm});
            skLineSegment(sketch, "E19.1.3.11", {"start": v(31.07, 62.1) * mm, "end": v(30.59, 62.59) * mm});
            skLineSegment(sketch, "E19.1.3.12", {"start": v(16.93, 81.9) * mm, "end": v(17.41, 81.41) * mm});
            skLineSegment(sketch, "E19.1.3.13", {"start": v(33.9, 79.07) * mm, "end": v(33.41, 78.59) * mm});
            skLineSegment(sketch, "E19.1.3.14", {"start": v(33.41, 65.41) * mm, "end": v(33.9, 64.93) * mm});
            skLineSegment(sketch, "E19.1.3.15", {"start": v(31.07, 81.9) * mm, "end": v(30.59, 81.41) * mm});
            skLineSegment(sketch, "E19.1.3.16", {"start": v(14.1, 79.07) * mm, "end": v(14.59, 78.59) * mm});
            skLineSegment(sketch, "E19.1.3.17", {"start": v(14.59, 65.41) * mm, "end": v(14.1, 64.93) * mm});
            skLineSegment(sketch, "E19.1.3.18", {"start": v(16.93, 62.1) * mm, "end": v(17.41, 62.59) * mm});
            skCircle(sketch, "E19.1.4.0", {"center": v(36, 95.25) * mm, "radius": 2 * mm});
            skArc(sketch, "E19.1.4.1", {"start": v(33.41, 89.41) * mm, "mid": v(30.59, 89.41) * mm, "end": v(30.59, 86.59) * mm});
            skArc(sketch, "E19.1.4.2", {"start": v(14.1, 103.07) * mm, "mid": v(14.1, 105.9) * mm, "end": v(16.93, 105.9) * mm});
            skArc(sketch, "E19.1.4.3", {"start": v(17.41, 86.59) * mm, "mid": v(17.41, 89.41) * mm, "end": v(14.59, 89.41) * mm});
            skCircle(sketch, "E19.1.4.4", {"center": v(24, 108) * mm, "radius": 2 * mm});
            skArc(sketch, "E19.1.4.5", {"start": v(30.59, 105.41) * mm, "mid": v(30.59, 102.59) * mm, "end": v(33.41, 102.59) * mm});
            skArc(sketch, "E19.1.4.6", {"start": v(14.59, 102.59) * mm, "mid": v(17.41, 102.59) * mm, "end": v(17.41, 105.41) * mm});
            skCircle(sketch, "E19.1.4.7", {"center": v(24, 96) * mm, "radius": 7 * mm});
            skArc(sketch, "E19.1.4.8", {"start": v(33.9, 103.07) * mm, "mid": v(33.9, 105.9) * mm, "end": v(31.07, 105.9) * mm});
            skArc(sketch, "E19.1.4.9", {"start": v(31.07, 86.1) * mm, "mid": v(33.9, 86.1) * mm, "end": v(33.9, 88.93) * mm});
            skArc(sketch, "E19.1.4.10", {"start": v(14.1, 88.93) * mm, "mid": v(14.1, 86.1) * mm, "end": v(16.93, 86.1) * mm});
            skLineSegment(sketch, "E19.1.4.11", {"start": v(31.07, 86.1) * mm, "end": v(30.59, 86.59) * mm});
            skLineSegment(sketch, "E19.1.4.12", {"start": v(16.93, 105.9) * mm, "end": v(17.41, 105.41) * mm});
            skLineSegment(sketch, "E19.1.4.13", {"start": v(33.9, 103.07) * mm, "end": v(33.41, 102.59) * mm});
            skLineSegment(sketch, "E19.1.4.14", {"start": v(33.41, 89.41) * mm, "end": v(33.9, 88.93) * mm});
            skLineSegment(sketch, "E19.1.4.15", {"start": v(31.07, 105.9) * mm, "end": v(30.59, 105.41) * mm});
            skLineSegment(sketch, "E19.1.4.16", {"start": v(14.1, 103.07) * mm, "end": v(14.59, 102.59) * mm});
            skLineSegment(sketch, "E19.1.4.17", {"start": v(14.59, 89.41) * mm, "end": v(14.1, 88.93) * mm});
            skLineSegment(sketch, "E19.1.4.18", {"start": v(16.93, 86.1) * mm, "end": v(17.41, 86.59) * mm});
            skCircle(sketch, "E19.1.5.0", {"center": v(36, 119.25) * mm, "radius": 2 * mm});
            skArc(sketch, "E19.1.5.1", {"start": v(33.41, 113.41) * mm, "mid": v(30.59, 113.41) * mm, "end": v(30.59, 110.59) * mm});
            skArc(sketch, "E19.1.5.2", {"start": v(14.1, 127.07) * mm, "mid": v(14.1, 129.9) * mm, "end": v(16.93, 129.9) * mm});
            skArc(sketch, "E19.1.5.3", {"start": v(17.41, 110.59) * mm, "mid": v(17.41, 113.41) * mm, "end": v(14.59, 113.41) * mm});
            skCircle(sketch, "E19.1.5.4", {"center": v(24, 132) * mm, "radius": 2 * mm});
            skArc(sketch, "E19.1.5.5", {"start": v(30.59, 129.41) * mm, "mid": v(30.59, 126.59) * mm, "end": v(33.41, 126.59) * mm});
            skArc(sketch, "E19.1.5.6", {"start": v(14.59, 126.59) * mm, "mid": v(17.41, 126.59) * mm, "end": v(17.41, 129.41) * mm});
            skCircle(sketch, "E19.1.5.7", {"center": v(24, 120) * mm, "radius": 7 * mm});
            skArc(sketch, "E19.1.5.8", {"start": v(33.9, 127.07) * mm, "mid": v(33.9, 129.9) * mm, "end": v(31.07, 129.9) * mm});
            skArc(sketch, "E19.1.5.9", {"start": v(31.07, 110.1) * mm, "mid": v(33.9, 110.1) * mm, "end": v(33.9, 112.93) * mm});
            skArc(sketch, "E19.1.5.10", {"start": v(14.1, 112.93) * mm, "mid": v(14.1, 110.1) * mm, "end": v(16.93, 110.1) * mm});
            skLineSegment(sketch, "E19.1.5.11", {"start": v(31.07, 110.1) * mm, "end": v(30.59, 110.59) * mm});
            skLineSegment(sketch, "E19.1.5.12", {"start": v(16.93, 129.9) * mm, "end": v(17.41, 129.41) * mm});
            skLineSegment(sketch, "E19.1.5.13", {"start": v(33.9, 127.07) * mm, "end": v(33.41, 126.59) * mm});
            skLineSegment(sketch, "E19.1.5.14", {"start": v(33.41, 113.41) * mm, "end": v(33.9, 112.93) * mm});
            skLineSegment(sketch, "E19.1.5.15", {"start": v(31.07, 129.9) * mm, "end": v(30.59, 129.41) * mm});
            skLineSegment(sketch, "E19.1.5.16", {"start": v(14.1, 127.07) * mm, "end": v(14.59, 126.59) * mm});
            skLineSegment(sketch, "E19.1.5.17", {"start": v(14.59, 113.41) * mm, "end": v(14.1, 112.93) * mm});
            skLineSegment(sketch, "E19.1.5.18", {"start": v(16.93, 110.1) * mm, "end": v(17.41, 110.59) * mm});
            skCircle(sketch, "E19.1.6.0", {"center": v(36, 143.25) * mm, "radius": 2 * mm});
            skArc(sketch, "E19.1.6.1", {"start": v(33.41, 137.41) * mm, "mid": v(30.59, 137.41) * mm, "end": v(30.59, 134.59) * mm});
            skArc(sketch, "E19.1.6.2", {"start": v(14.1, 151.07) * mm, "mid": v(14.1, 153.9) * mm, "end": v(16.93, 153.9) * mm});
            skArc(sketch, "E19.1.6.3", {"start": v(17.41, 134.59) * mm, "mid": v(17.41, 137.41) * mm, "end": v(14.59, 137.41) * mm});
            skCircle(sketch, "E19.1.6.4", {"center": v(24, 156) * mm, "radius": 2 * mm});
            skArc(sketch, "E19.1.6.5", {"start": v(30.59, 153.41) * mm, "mid": v(30.59, 150.59) * mm, "end": v(33.41, 150.59) * mm});
            skArc(sketch, "E19.1.6.6", {"start": v(14.59, 150.59) * mm, "mid": v(17.41, 150.59) * mm, "end": v(17.41, 153.41) * mm});
            skCircle(sketch, "E19.1.6.7", {"center": v(24, 144) * mm, "radius": 7 * mm});
            skArc(sketch, "E19.1.6.8", {"start": v(33.9, 151.07) * mm, "mid": v(33.9, 153.9) * mm, "end": v(31.07, 153.9) * mm});
            skArc(sketch, "E19.1.6.9", {"start": v(31.07, 134.1) * mm, "mid": v(33.9, 134.1) * mm, "end": v(33.9, 136.93) * mm});
            skArc(sketch, "E19.1.6.10", {"start": v(14.1, 136.93) * mm, "mid": v(14.1, 134.1) * mm, "end": v(16.93, 134.1) * mm});
            skLineSegment(sketch, "E19.1.6.11", {"start": v(31.07, 134.1) * mm, "end": v(30.59, 134.59) * mm});
            skLineSegment(sketch, "E19.1.6.12", {"start": v(16.93, 153.9) * mm, "end": v(17.41, 153.41) * mm});
            skLineSegment(sketch, "E19.1.6.13", {"start": v(33.9, 151.07) * mm, "end": v(33.41, 150.59) * mm});
            skLineSegment(sketch, "E19.1.6.14", {"start": v(33.41, 137.41) * mm, "end": v(33.9, 136.93) * mm});
            skLineSegment(sketch, "E19.1.6.15", {"start": v(31.07, 153.9) * mm, "end": v(30.59, 153.41) * mm});
            skLineSegment(sketch, "E19.1.6.16", {"start": v(14.1, 151.07) * mm, "end": v(14.59, 150.59) * mm});
            skLineSegment(sketch, "E19.1.6.17", {"start": v(14.59, 137.41) * mm, "end": v(14.1, 136.93) * mm});
            skLineSegment(sketch, "E19.1.6.18", {"start": v(16.93, 134.1) * mm, "end": v(17.41, 134.59) * mm});
            skCircle(sketch, "E19.1.7.0", {"center": v(36, 167.25) * mm, "radius": 2 * mm});
            skArc(sketch, "E19.1.7.1", {"start": v(33.41, 161.41) * mm, "mid": v(30.59, 161.41) * mm, "end": v(30.59, 158.59) * mm});
            skArc(sketch, "E19.1.7.2", {"start": v(14.1, 175.07) * mm, "mid": v(14.1, 177.9) * mm, "end": v(16.93, 177.9) * mm});
            skArc(sketch, "E19.1.7.3", {"start": v(17.41, 158.59) * mm, "mid": v(17.41, 161.41) * mm, "end": v(14.59, 161.41) * mm});
            skCircle(sketch, "E19.1.7.4", {"center": v(24, 180) * mm, "radius": 2 * mm});
            skArc(sketch, "E19.1.7.5", {"start": v(30.59, 177.41) * mm, "mid": v(30.59, 174.59) * mm, "end": v(33.41, 174.59) * mm});
            skArc(sketch, "E19.1.7.6", {"start": v(14.59, 174.59) * mm, "mid": v(17.41, 174.59) * mm, "end": v(17.41, 177.41) * mm});
            skCircle(sketch, "E19.1.7.7", {"center": v(24, 168) * mm, "radius": 7 * mm});
            skArc(sketch, "E19.1.7.8", {"start": v(33.9, 175.07) * mm, "mid": v(33.9, 177.9) * mm, "end": v(31.07, 177.9) * mm});
            skArc(sketch, "E19.1.7.9", {"start": v(31.07, 158.1) * mm, "mid": v(33.9, 158.1) * mm, "end": v(33.9, 160.93) * mm});
            skArc(sketch, "E19.1.7.10", {"start": v(14.1, 160.93) * mm, "mid": v(14.1, 158.1) * mm, "end": v(16.93, 158.1) * mm});
            skLineSegment(sketch, "E19.1.7.11", {"start": v(31.07, 158.1) * mm, "end": v(30.59, 158.59) * mm});
            skLineSegment(sketch, "E19.1.7.12", {"start": v(16.93, 177.9) * mm, "end": v(17.41, 177.41) * mm});
            skLineSegment(sketch, "E19.1.7.13", {"start": v(33.9, 175.07) * mm, "end": v(33.41, 174.59) * mm});
            skLineSegment(sketch, "E19.1.7.14", {"start": v(33.41, 161.41) * mm, "end": v(33.9, 160.93) * mm});
            skLineSegment(sketch, "E19.1.7.15", {"start": v(31.07, 177.9) * mm, "end": v(30.59, 177.41) * mm});
            skLineSegment(sketch, "E19.1.7.16", {"start": v(14.1, 175.07) * mm, "end": v(14.59, 174.59) * mm});
            skLineSegment(sketch, "E19.1.7.17", {"start": v(14.59, 161.41) * mm, "end": v(14.1, 160.93) * mm});
            skLineSegment(sketch, "E19.1.7.18", {"start": v(16.93, 158.1) * mm, "end": v(17.41, 158.59) * mm});
            skCircle(sketch, "E19.1.8.0", {"center": v(36, 191.25) * mm, "radius": 2 * mm});
            skArc(sketch, "E19.1.8.1", {"start": v(33.41, 185.41) * mm, "mid": v(30.59, 185.41) * mm, "end": v(30.59, 182.59) * mm});
            skArc(sketch, "E19.1.8.2", {"start": v(14.1, 199.07) * mm, "mid": v(14.1, 201.9) * mm, "end": v(16.93, 201.9) * mm});
            skArc(sketch, "E19.1.8.3", {"start": v(17.41, 182.59) * mm, "mid": v(17.41, 185.41) * mm, "end": v(14.59, 185.41) * mm});
            skCircle(sketch, "E19.1.8.4", {"center": v(24, 204) * mm, "radius": 2 * mm});
            skArc(sketch, "E19.1.8.5", {"start": v(30.59, 201.41) * mm, "mid": v(30.59, 198.59) * mm, "end": v(33.41, 198.59) * mm});
            skArc(sketch, "E19.1.8.6", {"start": v(14.59, 198.59) * mm, "mid": v(17.41, 198.59) * mm, "end": v(17.41, 201.41) * mm});
            skCircle(sketch, "E19.1.8.7", {"center": v(24, 192) * mm, "radius": 7 * mm});
            skArc(sketch, "E19.1.8.8", {"start": v(33.9, 199.07) * mm, "mid": v(33.9, 201.9) * mm, "end": v(31.07, 201.9) * mm});
            skArc(sketch, "E19.1.8.9", {"start": v(31.07, 182.1) * mm, "mid": v(33.9, 182.1) * mm, "end": v(33.9, 184.93) * mm});
            skArc(sketch, "E19.1.8.10", {"start": v(14.1, 184.93) * mm, "mid": v(14.1, 182.1) * mm, "end": v(16.93, 182.1) * mm});
            skLineSegment(sketch, "E19.1.8.11", {"start": v(31.07, 182.1) * mm, "end": v(30.59, 182.59) * mm});
            skLineSegment(sketch, "E19.1.8.12", {"start": v(16.93, 201.9) * mm, "end": v(17.41, 201.41) * mm});
            skLineSegment(sketch, "E19.1.8.13", {"start": v(33.9, 199.07) * mm, "end": v(33.41, 198.59) * mm});
            skLineSegment(sketch, "E19.1.8.14", {"start": v(33.41, 185.41) * mm, "end": v(33.9, 184.93) * mm});
            skLineSegment(sketch, "E19.1.8.15", {"start": v(31.07, 201.9) * mm, "end": v(30.59, 201.41) * mm});
            skLineSegment(sketch, "E19.1.8.16", {"start": v(14.1, 199.07) * mm, "end": v(14.59, 198.59) * mm});
            skLineSegment(sketch, "E19.1.8.17", {"start": v(14.59, 185.41) * mm, "end": v(14.1, 184.93) * mm});
            skLineSegment(sketch, "E19.1.8.18", {"start": v(16.93, 182.1) * mm, "end": v(17.41, 182.59) * mm});
            skCircle(sketch, "E19.2.0.0", {"center": v(60, -0.75) * mm, "radius": 2 * mm});
            skArc(sketch, "E19.2.0.1", {"start": v(57.41, -6.59) * mm, "mid": v(54.59, -6.59) * mm, "end": v(54.59, -9.41) * mm});
            skArc(sketch, "E19.2.0.2", {"start": v(38.1, 7.07) * mm, "mid": v(38.1, 9.9) * mm, "end": v(40.93, 9.9) * mm});
            skArc(sketch, "E19.2.0.3", {"start": v(41.41, -9.41) * mm, "mid": v(41.41, -6.59) * mm, "end": v(38.59, -6.59) * mm});
            skCircle(sketch, "E19.2.0.4", {"center": v(48, 12) * mm, "radius": 2 * mm});
            skArc(sketch, "E19.2.0.5", {"start": v(54.59, 9.41) * mm, "mid": v(54.59, 6.59) * mm, "end": v(57.41, 6.59) * mm});
            skArc(sketch, "E19.2.0.6", {"start": v(38.59, 6.59) * mm, "mid": v(41.41, 6.59) * mm, "end": v(41.41, 9.41) * mm});
            skCircle(sketch, "E19.2.0.7", {"center": v(48, 0) * mm, "radius": 7 * mm});
            skArc(sketch, "E19.2.0.8", {"start": v(57.9, 7.07) * mm, "mid": v(57.9, 9.9) * mm, "end": v(55.07, 9.9) * mm});
            skArc(sketch, "E19.2.0.9", {"start": v(55.07, -9.9) * mm, "mid": v(57.9, -9.9) * mm, "end": v(57.9, -7.07) * mm});
            skArc(sketch, "E19.2.0.10", {"start": v(38.1, -7.07) * mm, "mid": v(38.1, -9.9) * mm, "end": v(40.93, -9.9) * mm});
            skLineSegment(sketch, "E19.2.0.11", {"start": v(55.07, -9.9) * mm, "end": v(54.59, -9.41) * mm});
            skLineSegment(sketch, "E19.2.0.12", {"start": v(40.93, 9.9) * mm, "end": v(41.41, 9.41) * mm});
            skLineSegment(sketch, "E19.2.0.13", {"start": v(57.9, 7.07) * mm, "end": v(57.41, 6.59) * mm});
            skLineSegment(sketch, "E19.2.0.14", {"start": v(57.41, -6.59) * mm, "end": v(57.9, -7.07) * mm});
            skLineSegment(sketch, "E19.2.0.15", {"start": v(55.07, 9.9) * mm, "end": v(54.59, 9.41) * mm});
            skLineSegment(sketch, "E19.2.0.16", {"start": v(38.1, 7.07) * mm, "end": v(38.59, 6.59) * mm});
            skLineSegment(sketch, "E19.2.0.17", {"start": v(38.59, -6.59) * mm, "end": v(38.1, -7.07) * mm});
            skLineSegment(sketch, "E19.2.0.18", {"start": v(40.93, -9.9) * mm, "end": v(41.41, -9.41) * mm});
            skCircle(sketch, "E19.2.1.0", {"center": v(60, 23.25) * mm, "radius": 2 * mm});
            skArc(sketch, "E19.2.1.1", {"start": v(57.41, 17.41) * mm, "mid": v(54.59, 17.41) * mm, "end": v(54.59, 14.59) * mm});
            skArc(sketch, "E19.2.1.2", {"start": v(38.1, 31.07) * mm, "mid": v(38.1, 33.9) * mm, "end": v(40.93, 33.9) * mm});
            skArc(sketch, "E19.2.1.3", {"start": v(41.41, 14.59) * mm, "mid": v(41.41, 17.41) * mm, "end": v(38.59, 17.41) * mm});
            skCircle(sketch, "E19.2.1.4", {"center": v(48, 36) * mm, "radius": 2 * mm});
            skArc(sketch, "E19.2.1.5", {"start": v(54.59, 33.41) * mm, "mid": v(54.59, 30.59) * mm, "end": v(57.41, 30.59) * mm});
            skArc(sketch, "E19.2.1.6", {"start": v(38.59, 30.59) * mm, "mid": v(41.41, 30.59) * mm, "end": v(41.41, 33.41) * mm});
            skCircle(sketch, "E19.2.1.7", {"center": v(48, 24) * mm, "radius": 7 * mm});
            skArc(sketch, "E19.2.1.8", {"start": v(57.9, 31.07) * mm, "mid": v(57.9, 33.9) * mm, "end": v(55.07, 33.9) * mm});
            skArc(sketch, "E19.2.1.9", {"start": v(55.07, 14.1) * mm, "mid": v(57.9, 14.1) * mm, "end": v(57.9, 16.93) * mm});
            skArc(sketch, "E19.2.1.10", {"start": v(38.1, 16.93) * mm, "mid": v(38.1, 14.1) * mm, "end": v(40.93, 14.1) * mm});
            skLineSegment(sketch, "E19.2.1.11", {"start": v(55.07, 14.1) * mm, "end": v(54.59, 14.59) * mm});
            skLineSegment(sketch, "E19.2.1.12", {"start": v(40.93, 33.9) * mm, "end": v(41.41, 33.41) * mm});
            skLineSegment(sketch, "E19.2.1.13", {"start": v(57.9, 31.07) * mm, "end": v(57.41, 30.59) * mm});
            skLineSegment(sketch, "E19.2.1.14", {"start": v(57.41, 17.41) * mm, "end": v(57.9, 16.93) * mm});
            skLineSegment(sketch, "E19.2.1.15", {"start": v(55.07, 33.9) * mm, "end": v(54.59, 33.41) * mm});
            skLineSegment(sketch, "E19.2.1.16", {"start": v(38.1, 31.07) * mm, "end": v(38.59, 30.59) * mm});
            skLineSegment(sketch, "E19.2.1.17", {"start": v(38.59, 17.41) * mm, "end": v(38.1, 16.93) * mm});
            skLineSegment(sketch, "E19.2.1.18", {"start": v(40.93, 14.1) * mm, "end": v(41.41, 14.59) * mm});
            skCircle(sketch, "E19.2.2.0", {"center": v(60, 47.25) * mm, "radius": 2 * mm});
            skArc(sketch, "E19.2.2.1", {"start": v(57.41, 41.41) * mm, "mid": v(54.59, 41.41) * mm, "end": v(54.59, 38.59) * mm});
            skArc(sketch, "E19.2.2.2", {"start": v(38.1, 55.07) * mm, "mid": v(38.1, 57.9) * mm, "end": v(40.93, 57.9) * mm});
            skArc(sketch, "E19.2.2.3", {"start": v(41.41, 38.59) * mm, "mid": v(41.41, 41.41) * mm, "end": v(38.59, 41.41) * mm});
            skCircle(sketch, "E19.2.2.4", {"center": v(48, 60) * mm, "radius": 2 * mm});
            skArc(sketch, "E19.2.2.5", {"start": v(54.59, 57.41) * mm, "mid": v(54.59, 54.59) * mm, "end": v(57.41, 54.59) * mm});
            skArc(sketch, "E19.2.2.6", {"start": v(38.59, 54.59) * mm, "mid": v(41.41, 54.59) * mm, "end": v(41.41, 57.41) * mm});
            skCircle(sketch, "E19.2.2.7", {"center": v(48, 48) * mm, "radius": 7 * mm});
            skArc(sketch, "E19.2.2.8", {"start": v(57.9, 55.07) * mm, "mid": v(57.9, 57.9) * mm, "end": v(55.07, 57.9) * mm});
            skArc(sketch, "E19.2.2.9", {"start": v(55.07, 38.1) * mm, "mid": v(57.9, 38.1) * mm, "end": v(57.9, 40.93) * mm});
            skArc(sketch, "E19.2.2.10", {"start": v(38.1, 40.93) * mm, "mid": v(38.1, 38.1) * mm, "end": v(40.93, 38.1) * mm});
            skLineSegment(sketch, "E19.2.2.11", {"start": v(55.07, 38.1) * mm, "end": v(54.59, 38.59) * mm});
            skLineSegment(sketch, "E19.2.2.12", {"start": v(40.93, 57.9) * mm, "end": v(41.41, 57.41) * mm});
            skLineSegment(sketch, "E19.2.2.13", {"start": v(57.9, 55.07) * mm, "end": v(57.41, 54.59) * mm});
            skLineSegment(sketch, "E19.2.2.14", {"start": v(57.41, 41.41) * mm, "end": v(57.9, 40.93) * mm});
            skLineSegment(sketch, "E19.2.2.15", {"start": v(55.07, 57.9) * mm, "end": v(54.59, 57.41) * mm});
            skLineSegment(sketch, "E19.2.2.16", {"start": v(38.1, 55.07) * mm, "end": v(38.59, 54.59) * mm});
            skLineSegment(sketch, "E19.2.2.17", {"start": v(38.59, 41.41) * mm, "end": v(38.1, 40.93) * mm});
            skLineSegment(sketch, "E19.2.2.18", {"start": v(40.93, 38.1) * mm, "end": v(41.41, 38.59) * mm});
            skCircle(sketch, "E19.2.3.0", {"center": v(60, 71.25) * mm, "radius": 2 * mm});
            skArc(sketch, "E19.2.3.1", {"start": v(57.41, 65.41) * mm, "mid": v(54.59, 65.41) * mm, "end": v(54.59, 62.59) * mm});
            skArc(sketch, "E19.2.3.2", {"start": v(38.1, 79.07) * mm, "mid": v(38.1, 81.9) * mm, "end": v(40.93, 81.9) * mm});
            skArc(sketch, "E19.2.3.3", {"start": v(41.41, 62.59) * mm, "mid": v(41.41, 65.41) * mm, "end": v(38.59, 65.41) * mm});
            skCircle(sketch, "E19.2.3.4", {"center": v(48, 84) * mm, "radius": 2 * mm});
            skArc(sketch, "E19.2.3.5", {"start": v(54.59, 81.41) * mm, "mid": v(54.59, 78.59) * mm, "end": v(57.41, 78.59) * mm});
            skArc(sketch, "E19.2.3.6", {"start": v(38.59, 78.59) * mm, "mid": v(41.41, 78.59) * mm, "end": v(41.41, 81.41) * mm});
            skCircle(sketch, "E19.2.3.7", {"center": v(48, 72) * mm, "radius": 7 * mm});
            skArc(sketch, "E19.2.3.8", {"start": v(57.9, 79.07) * mm, "mid": v(57.9, 81.9) * mm, "end": v(55.07, 81.9) * mm});
            skArc(sketch, "E19.2.3.9", {"start": v(55.07, 62.1) * mm, "mid": v(57.9, 62.1) * mm, "end": v(57.9, 64.93) * mm});
            skArc(sketch, "E19.2.3.10", {"start": v(38.1, 64.93) * mm, "mid": v(38.1, 62.1) * mm, "end": v(40.93, 62.1) * mm});
            skLineSegment(sketch, "E19.2.3.11", {"start": v(55.07, 62.1) * mm, "end": v(54.59, 62.59) * mm});
            skLineSegment(sketch, "E19.2.3.12", {"start": v(40.93, 81.9) * mm, "end": v(41.41, 81.41) * mm});
            skLineSegment(sketch, "E19.2.3.13", {"start": v(57.9, 79.07) * mm, "end": v(57.41, 78.59) * mm});
            skLineSegment(sketch, "E19.2.3.14", {"start": v(57.41, 65.41) * mm, "end": v(57.9, 64.93) * mm});
            skLineSegment(sketch, "E19.2.3.15", {"start": v(55.07, 81.9) * mm, "end": v(54.59, 81.41) * mm});
            skLineSegment(sketch, "E19.2.3.16", {"start": v(38.1, 79.07) * mm, "end": v(38.59, 78.59) * mm});
            skLineSegment(sketch, "E19.2.3.17", {"start": v(38.59, 65.41) * mm, "end": v(38.1, 64.93) * mm});
            skLineSegment(sketch, "E19.2.3.18", {"start": v(40.93, 62.1) * mm, "end": v(41.41, 62.59) * mm});
            skCircle(sketch, "E19.2.4.0", {"center": v(60, 95.25) * mm, "radius": 2 * mm});
            skArc(sketch, "E19.2.4.1", {"start": v(57.41, 89.41) * mm, "mid": v(54.59, 89.41) * mm, "end": v(54.59, 86.59) * mm});
            skArc(sketch, "E19.2.4.2", {"start": v(38.1, 103.07) * mm, "mid": v(38.1, 105.9) * mm, "end": v(40.93, 105.9) * mm});
            skArc(sketch, "E19.2.4.3", {"start": v(41.41, 86.59) * mm, "mid": v(41.41, 89.41) * mm, "end": v(38.59, 89.41) * mm});
            skCircle(sketch, "E19.2.4.4", {"center": v(48, 108) * mm, "radius": 2 * mm});
            skArc(sketch, "E19.2.4.5", {"start": v(54.59, 105.41) * mm, "mid": v(54.59, 102.59) * mm, "end": v(57.41, 102.59) * mm});
            skArc(sketch, "E19.2.4.6", {"start": v(38.59, 102.59) * mm, "mid": v(41.41, 102.59) * mm, "end": v(41.41, 105.41) * mm});
            skCircle(sketch, "E19.2.4.7", {"center": v(48, 96) * mm, "radius": 7 * mm});
            skArc(sketch, "E19.2.4.8", {"start": v(57.9, 103.07) * mm, "mid": v(57.9, 105.9) * mm, "end": v(55.07, 105.9) * mm});
            skArc(sketch, "E19.2.4.9", {"start": v(55.07, 86.1) * mm, "mid": v(57.9, 86.1) * mm, "end": v(57.9, 88.93) * mm});
            skArc(sketch, "E19.2.4.10", {"start": v(38.1, 88.93) * mm, "mid": v(38.1, 86.1) * mm, "end": v(40.93, 86.1) * mm});
            skLineSegment(sketch, "E19.2.4.11", {"start": v(55.07, 86.1) * mm, "end": v(54.59, 86.59) * mm});
            skLineSegment(sketch, "E19.2.4.12", {"start": v(40.93, 105.9) * mm, "end": v(41.41, 105.41) * mm});
            skLineSegment(sketch, "E19.2.4.13", {"start": v(57.9, 103.07) * mm, "end": v(57.41, 102.59) * mm});
            skLineSegment(sketch, "E19.2.4.14", {"start": v(57.41, 89.41) * mm, "end": v(57.9, 88.93) * mm});
            skLineSegment(sketch, "E19.2.4.15", {"start": v(55.07, 105.9) * mm, "end": v(54.59, 105.41) * mm});
            skLineSegment(sketch, "E19.2.4.16", {"start": v(38.1, 103.07) * mm, "end": v(38.59, 102.59) * mm});
            skLineSegment(sketch, "E19.2.4.17", {"start": v(38.59, 89.41) * mm, "end": v(38.1, 88.93) * mm});
            skLineSegment(sketch, "E19.2.4.18", {"start": v(40.93, 86.1) * mm, "end": v(41.41, 86.59) * mm});
            skCircle(sketch, "E19.2.5.0", {"center": v(60, 119.25) * mm, "radius": 2 * mm});
            skArc(sketch, "E19.2.5.1", {"start": v(57.41, 113.41) * mm, "mid": v(54.59, 113.41) * mm, "end": v(54.59, 110.59) * mm});
            skArc(sketch, "E19.2.5.2", {"start": v(38.1, 127.07) * mm, "mid": v(38.1, 129.9) * mm, "end": v(40.93, 129.9) * mm});
            skArc(sketch, "E19.2.5.3", {"start": v(41.41, 110.59) * mm, "mid": v(41.41, 113.41) * mm, "end": v(38.59, 113.41) * mm});
            skCircle(sketch, "E19.2.5.4", {"center": v(48, 132) * mm, "radius": 2 * mm});
            skArc(sketch, "E19.2.5.5", {"start": v(54.59, 129.41) * mm, "mid": v(54.59, 126.59) * mm, "end": v(57.41, 126.59) * mm});
            skArc(sketch, "E19.2.5.6", {"start": v(38.59, 126.59) * mm, "mid": v(41.41, 126.59) * mm, "end": v(41.41, 129.41) * mm});
            skCircle(sketch, "E19.2.5.7", {"center": v(48, 120) * mm, "radius": 7 * mm});
            skArc(sketch, "E19.2.5.8", {"start": v(57.9, 127.07) * mm, "mid": v(57.9, 129.9) * mm, "end": v(55.07, 129.9) * mm});
            skArc(sketch, "E19.2.5.9", {"start": v(55.07, 110.1) * mm, "mid": v(57.9, 110.1) * mm, "end": v(57.9, 112.93) * mm});
            skArc(sketch, "E19.2.5.10", {"start": v(38.1, 112.93) * mm, "mid": v(38.1, 110.1) * mm, "end": v(40.93, 110.1) * mm});
            skLineSegment(sketch, "E19.2.5.11", {"start": v(55.07, 110.1) * mm, "end": v(54.59, 110.59) * mm});
            skLineSegment(sketch, "E19.2.5.12", {"start": v(40.93, 129.9) * mm, "end": v(41.41, 129.41) * mm});
            skLineSegment(sketch, "E19.2.5.13", {"start": v(57.9, 127.07) * mm, "end": v(57.41, 126.59) * mm});
            skLineSegment(sketch, "E19.2.5.14", {"start": v(57.41, 113.41) * mm, "end": v(57.9, 112.93) * mm});
            skLineSegment(sketch, "E19.2.5.15", {"start": v(55.07, 129.9) * mm, "end": v(54.59, 129.41) * mm});
            skLineSegment(sketch, "E19.2.5.16", {"start": v(38.1, 127.07) * mm, "end": v(38.59, 126.59) * mm});
            skLineSegment(sketch, "E19.2.5.17", {"start": v(38.59, 113.41) * mm, "end": v(38.1, 112.93) * mm});
            skLineSegment(sketch, "E19.2.5.18", {"start": v(40.93, 110.1) * mm, "end": v(41.41, 110.59) * mm});
            skCircle(sketch, "E19.2.6.0", {"center": v(60, 143.25) * mm, "radius": 2 * mm});
            skArc(sketch, "E19.2.6.1", {"start": v(57.41, 137.41) * mm, "mid": v(54.59, 137.41) * mm, "end": v(54.59, 134.59) * mm});
            skArc(sketch, "E19.2.6.2", {"start": v(38.1, 151.07) * mm, "mid": v(38.1, 153.9) * mm, "end": v(40.93, 153.9) * mm});
            skArc(sketch, "E19.2.6.3", {"start": v(41.41, 134.59) * mm, "mid": v(41.41, 137.41) * mm, "end": v(38.59, 137.41) * mm});
            skCircle(sketch, "E19.2.6.4", {"center": v(48, 156) * mm, "radius": 2 * mm});
            skArc(sketch, "E19.2.6.5", {"start": v(54.59, 153.41) * mm, "mid": v(54.59, 150.59) * mm, "end": v(57.41, 150.59) * mm});
            skArc(sketch, "E19.2.6.6", {"start": v(38.59, 150.59) * mm, "mid": v(41.41, 150.59) * mm, "end": v(41.41, 153.41) * mm});
            skCircle(sketch, "E19.2.6.7", {"center": v(48, 144) * mm, "radius": 7 * mm});
            skArc(sketch, "E19.2.6.8", {"start": v(57.9, 151.07) * mm, "mid": v(57.9, 153.9) * mm, "end": v(55.07, 153.9) * mm});
            skArc(sketch, "E19.2.6.9", {"start": v(55.07, 134.1) * mm, "mid": v(57.9, 134.1) * mm, "end": v(57.9, 136.93) * mm});
            skArc(sketch, "E19.2.6.10", {"start": v(38.1, 136.93) * mm, "mid": v(38.1, 134.1) * mm, "end": v(40.93, 134.1) * mm});
            skLineSegment(sketch, "E19.2.6.11", {"start": v(55.07, 134.1) * mm, "end": v(54.59, 134.59) * mm});
            skLineSegment(sketch, "E19.2.6.12", {"start": v(40.93, 153.9) * mm, "end": v(41.41, 153.41) * mm});
            skLineSegment(sketch, "E19.2.6.13", {"start": v(57.9, 151.07) * mm, "end": v(57.41, 150.59) * mm});
            skLineSegment(sketch, "E19.2.6.14", {"start": v(57.41, 137.41) * mm, "end": v(57.9, 136.93) * mm});
            skLineSegment(sketch, "E19.2.6.15", {"start": v(55.07, 153.9) * mm, "end": v(54.59, 153.41) * mm});
            skLineSegment(sketch, "E19.2.6.16", {"start": v(38.1, 151.07) * mm, "end": v(38.59, 150.59) * mm});
            skLineSegment(sketch, "E19.2.6.17", {"start": v(38.59, 137.41) * mm, "end": v(38.1, 136.93) * mm});
            skLineSegment(sketch, "E19.2.6.18", {"start": v(40.93, 134.1) * mm, "end": v(41.41, 134.59) * mm});
            skCircle(sketch, "E19.2.7.0", {"center": v(60, 167.25) * mm, "radius": 2 * mm});
            skArc(sketch, "E19.2.7.1", {"start": v(57.41, 161.41) * mm, "mid": v(54.59, 161.41) * mm, "end": v(54.59, 158.59) * mm});
            skArc(sketch, "E19.2.7.2", {"start": v(38.1, 175.07) * mm, "mid": v(38.1, 177.9) * mm, "end": v(40.93, 177.9) * mm});
            skArc(sketch, "E19.2.7.3", {"start": v(41.41, 158.59) * mm, "mid": v(41.41, 161.41) * mm, "end": v(38.59, 161.41) * mm});
            skCircle(sketch, "E19.2.7.4", {"center": v(48, 180) * mm, "radius": 2 * mm});
            skArc(sketch, "E19.2.7.5", {"start": v(54.59, 177.41) * mm, "mid": v(54.59, 174.59) * mm, "end": v(57.41, 174.59) * mm});
            skArc(sketch, "E19.2.7.6", {"start": v(38.59, 174.59) * mm, "mid": v(41.41, 174.59) * mm, "end": v(41.41, 177.41) * mm});
            skCircle(sketch, "E19.2.7.7", {"center": v(48, 168) * mm, "radius": 7 * mm});
            skArc(sketch, "E19.2.7.8", {"start": v(57.9, 175.07) * mm, "mid": v(57.9, 177.9) * mm, "end": v(55.07, 177.9) * mm});
            skArc(sketch, "E19.2.7.9", {"start": v(55.07, 158.1) * mm, "mid": v(57.9, 158.1) * mm, "end": v(57.9, 160.93) * mm});
            skArc(sketch, "E19.2.7.10", {"start": v(38.1, 160.93) * mm, "mid": v(38.1, 158.1) * mm, "end": v(40.93, 158.1) * mm});
            skLineSegment(sketch, "E19.2.7.11", {"start": v(55.07, 158.1) * mm, "end": v(54.59, 158.59) * mm});
            skLineSegment(sketch, "E19.2.7.12", {"start": v(40.93, 177.9) * mm, "end": v(41.41, 177.41) * mm});
            skLineSegment(sketch, "E19.2.7.13", {"start": v(57.9, 175.07) * mm, "end": v(57.41, 174.59) * mm});
            skLineSegment(sketch, "E19.2.7.14", {"start": v(57.41, 161.41) * mm, "end": v(57.9, 160.93) * mm});
            skLineSegment(sketch, "E19.2.7.15", {"start": v(55.07, 177.9) * mm, "end": v(54.59, 177.41) * mm});
            skLineSegment(sketch, "E19.2.7.16", {"start": v(38.1, 175.07) * mm, "end": v(38.59, 174.59) * mm});
            skLineSegment(sketch, "E19.2.7.17", {"start": v(38.59, 161.41) * mm, "end": v(38.1, 160.93) * mm});
            skLineSegment(sketch, "E19.2.7.18", {"start": v(40.93, 158.1) * mm, "end": v(41.41, 158.59) * mm});
            skCircle(sketch, "E19.2.8.0", {"center": v(60, 191.25) * mm, "radius": 2 * mm});
            skArc(sketch, "E19.2.8.1", {"start": v(57.41, 185.41) * mm, "mid": v(54.59, 185.41) * mm, "end": v(54.59, 182.59) * mm});
            skArc(sketch, "E19.2.8.2", {"start": v(38.1, 199.07) * mm, "mid": v(38.1, 201.9) * mm, "end": v(40.93, 201.9) * mm});
            skArc(sketch, "E19.2.8.3", {"start": v(41.41, 182.59) * mm, "mid": v(41.41, 185.41) * mm, "end": v(38.59, 185.41) * mm});
            skCircle(sketch, "E19.2.8.4", {"center": v(48, 204) * mm, "radius": 2 * mm});
            skArc(sketch, "E19.2.8.5", {"start": v(54.59, 201.41) * mm, "mid": v(54.59, 198.59) * mm, "end": v(57.41, 198.59) * mm});
            skArc(sketch, "E19.2.8.6", {"start": v(38.59, 198.59) * mm, "mid": v(41.41, 198.59) * mm, "end": v(41.41, 201.41) * mm});
            skCircle(sketch, "E19.2.8.7", {"center": v(48, 192) * mm, "radius": 7 * mm});
            skArc(sketch, "E19.2.8.8", {"start": v(57.9, 199.07) * mm, "mid": v(57.9, 201.9) * mm, "end": v(55.07, 201.9) * mm});
            skArc(sketch, "E19.2.8.9", {"start": v(55.07, 182.1) * mm, "mid": v(57.9, 182.1) * mm, "end": v(57.9, 184.93) * mm});
            skArc(sketch, "E19.2.8.10", {"start": v(38.1, 184.93) * mm, "mid": v(38.1, 182.1) * mm, "end": v(40.93, 182.1) * mm});
            skLineSegment(sketch, "E19.2.8.11", {"start": v(55.07, 182.1) * mm, "end": v(54.59, 182.59) * mm});
            skLineSegment(sketch, "E19.2.8.12", {"start": v(40.93, 201.9) * mm, "end": v(41.41, 201.41) * mm});
            skLineSegment(sketch, "E19.2.8.13", {"start": v(57.9, 199.07) * mm, "end": v(57.41, 198.59) * mm});
            skLineSegment(sketch, "E19.2.8.14", {"start": v(57.41, 185.41) * mm, "end": v(57.9, 184.93) * mm});
            skLineSegment(sketch, "E19.2.8.15", {"start": v(55.07, 201.9) * mm, "end": v(54.59, 201.41) * mm});
            skLineSegment(sketch, "E19.2.8.16", {"start": v(38.1, 199.07) * mm, "end": v(38.59, 198.59) * mm});
            skLineSegment(sketch, "E19.2.8.17", {"start": v(38.59, 185.41) * mm, "end": v(38.1, 184.93) * mm});
            skLineSegment(sketch, "E19.2.8.18", {"start": v(40.93, 182.1) * mm, "end": v(41.41, 182.59) * mm});
            skCircle(sketch, "E19.3.0.0", {"center": v(84, -0.75) * mm, "radius": 2 * mm});
            skArc(sketch, "E19.3.0.1", {"start": v(81.41, -6.59) * mm, "mid": v(78.59, -6.59) * mm, "end": v(78.59, -9.41) * mm});
            skArc(sketch, "E19.3.0.2", {"start": v(62.1, 7.07) * mm, "mid": v(62.1, 9.9) * mm, "end": v(64.93, 9.9) * mm});
            skArc(sketch, "E19.3.0.3", {"start": v(65.41, -9.41) * mm, "mid": v(65.41, -6.59) * mm, "end": v(62.59, -6.59) * mm});
            skCircle(sketch, "E19.3.0.4", {"center": v(72, 12) * mm, "radius": 2 * mm});
            skArc(sketch, "E19.3.0.5", {"start": v(78.59, 9.41) * mm, "mid": v(78.59, 6.59) * mm, "end": v(81.41, 6.59) * mm});
            skArc(sketch, "E19.3.0.6", {"start": v(62.59, 6.59) * mm, "mid": v(65.41, 6.59) * mm, "end": v(65.41, 9.41) * mm});
            skCircle(sketch, "E19.3.0.7", {"center": v(72, 0) * mm, "radius": 7 * mm});
            skArc(sketch, "E19.3.0.8", {"start": v(81.9, 7.07) * mm, "mid": v(81.9, 9.9) * mm, "end": v(79.07, 9.9) * mm});
            skArc(sketch, "E19.3.0.9", {"start": v(79.07, -9.9) * mm, "mid": v(81.9, -9.9) * mm, "end": v(81.9, -7.07) * mm});
            skArc(sketch, "E19.3.0.10", {"start": v(62.1, -7.07) * mm, "mid": v(62.1, -9.9) * mm, "end": v(64.93, -9.9) * mm});
            skLineSegment(sketch, "E19.3.0.11", {"start": v(79.07, -9.9) * mm, "end": v(78.59, -9.41) * mm});
            skLineSegment(sketch, "E19.3.0.12", {"start": v(64.93, 9.9) * mm, "end": v(65.41, 9.41) * mm});
            skLineSegment(sketch, "E19.3.0.13", {"start": v(81.9, 7.07) * mm, "end": v(81.41, 6.59) * mm});
            skLineSegment(sketch, "E19.3.0.14", {"start": v(81.41, -6.59) * mm, "end": v(81.9, -7.07) * mm});
            skLineSegment(sketch, "E19.3.0.15", {"start": v(79.07, 9.9) * mm, "end": v(78.59, 9.41) * mm});
            skLineSegment(sketch, "E19.3.0.16", {"start": v(62.1, 7.07) * mm, "end": v(62.59, 6.59) * mm});
            skLineSegment(sketch, "E19.3.0.17", {"start": v(62.59, -6.59) * mm, "end": v(62.1, -7.07) * mm});
            skLineSegment(sketch, "E19.3.0.18", {"start": v(64.93, -9.9) * mm, "end": v(65.41, -9.41) * mm});
            skCircle(sketch, "E19.3.1.0", {"center": v(84, 23.25) * mm, "radius": 2 * mm});
            skArc(sketch, "E19.3.1.1", {"start": v(81.41, 17.41) * mm, "mid": v(78.59, 17.41) * mm, "end": v(78.59, 14.59) * mm});
            skArc(sketch, "E19.3.1.2", {"start": v(62.1, 31.07) * mm, "mid": v(62.1, 33.9) * mm, "end": v(64.93, 33.9) * mm});
            skArc(sketch, "E19.3.1.3", {"start": v(65.41, 14.59) * mm, "mid": v(65.41, 17.41) * mm, "end": v(62.59, 17.41) * mm});
            skCircle(sketch, "E19.3.1.4", {"center": v(72, 36) * mm, "radius": 2 * mm});
            skArc(sketch, "E19.3.1.5", {"start": v(78.59, 33.41) * mm, "mid": v(78.59, 30.59) * mm, "end": v(81.41, 30.59) * mm});
            skArc(sketch, "E19.3.1.6", {"start": v(62.59, 30.59) * mm, "mid": v(65.41, 30.59) * mm, "end": v(65.41, 33.41) * mm});
            skCircle(sketch, "E19.3.1.7", {"center": v(72, 24) * mm, "radius": 7 * mm});
            skArc(sketch, "E19.3.1.8", {"start": v(81.9, 31.07) * mm, "mid": v(81.9, 33.9) * mm, "end": v(79.07, 33.9) * mm});
            skArc(sketch, "E19.3.1.9", {"start": v(79.07, 14.1) * mm, "mid": v(81.9, 14.1) * mm, "end": v(81.9, 16.93) * mm});
            skArc(sketch, "E19.3.1.10", {"start": v(62.1, 16.93) * mm, "mid": v(62.1, 14.1) * mm, "end": v(64.93, 14.1) * mm});
            skLineSegment(sketch, "E19.3.1.11", {"start": v(79.07, 14.1) * mm, "end": v(78.59, 14.59) * mm});
            skLineSegment(sketch, "E19.3.1.12", {"start": v(64.93, 33.9) * mm, "end": v(65.41, 33.41) * mm});
            skLineSegment(sketch, "E19.3.1.13", {"start": v(81.9, 31.07) * mm, "end": v(81.41, 30.59) * mm});
            skLineSegment(sketch, "E19.3.1.14", {"start": v(81.41, 17.41) * mm, "end": v(81.9, 16.93) * mm});
            skLineSegment(sketch, "E19.3.1.15", {"start": v(79.07, 33.9) * mm, "end": v(78.59, 33.41) * mm});
            skLineSegment(sketch, "E19.3.1.16", {"start": v(62.1, 31.07) * mm, "end": v(62.59, 30.59) * mm});
            skLineSegment(sketch, "E19.3.1.17", {"start": v(62.59, 17.41) * mm, "end": v(62.1, 16.93) * mm});
            skLineSegment(sketch, "E19.3.1.18", {"start": v(64.93, 14.1) * mm, "end": v(65.41, 14.59) * mm});
            skCircle(sketch, "E19.3.2.0", {"center": v(84, 47.25) * mm, "radius": 2 * mm});
            skArc(sketch, "E19.3.2.1", {"start": v(81.41, 41.41) * mm, "mid": v(78.59, 41.41) * mm, "end": v(78.59, 38.59) * mm});
            skArc(sketch, "E19.3.2.2", {"start": v(62.1, 55.07) * mm, "mid": v(62.1, 57.9) * mm, "end": v(64.93, 57.9) * mm});
            skArc(sketch, "E19.3.2.3", {"start": v(65.41, 38.59) * mm, "mid": v(65.41, 41.41) * mm, "end": v(62.59, 41.41) * mm});
            skCircle(sketch, "E19.3.2.4", {"center": v(72, 60) * mm, "radius": 2 * mm});
            skArc(sketch, "E19.3.2.5", {"start": v(78.59, 57.41) * mm, "mid": v(78.59, 54.59) * mm, "end": v(81.41, 54.59) * mm});
            skArc(sketch, "E19.3.2.6", {"start": v(62.59, 54.59) * mm, "mid": v(65.41, 54.59) * mm, "end": v(65.41, 57.41) * mm});
            skCircle(sketch, "E19.3.2.7", {"center": v(72, 48) * mm, "radius": 7 * mm});
            skArc(sketch, "E19.3.2.8", {"start": v(81.9, 55.07) * mm, "mid": v(81.9, 57.9) * mm, "end": v(79.07, 57.9) * mm});
            skArc(sketch, "E19.3.2.9", {"start": v(79.07, 38.1) * mm, "mid": v(81.9, 38.1) * mm, "end": v(81.9, 40.93) * mm});
            skArc(sketch, "E19.3.2.10", {"start": v(62.1, 40.93) * mm, "mid": v(62.1, 38.1) * mm, "end": v(64.93, 38.1) * mm});
            skLineSegment(sketch, "E19.3.2.11", {"start": v(79.07, 38.1) * mm, "end": v(78.59, 38.59) * mm});
            skLineSegment(sketch, "E19.3.2.12", {"start": v(64.93, 57.9) * mm, "end": v(65.41, 57.41) * mm});
            skLineSegment(sketch, "E19.3.2.13", {"start": v(81.9, 55.07) * mm, "end": v(81.41, 54.59) * mm});
            skLineSegment(sketch, "E19.3.2.14", {"start": v(81.41, 41.41) * mm, "end": v(81.9, 40.93) * mm});
            skLineSegment(sketch, "E19.3.2.15", {"start": v(79.07, 57.9) * mm, "end": v(78.59, 57.41) * mm});
            skLineSegment(sketch, "E19.3.2.16", {"start": v(62.1, 55.07) * mm, "end": v(62.59, 54.59) * mm});
            skLineSegment(sketch, "E19.3.2.17", {"start": v(62.59, 41.41) * mm, "end": v(62.1, 40.93) * mm});
            skLineSegment(sketch, "E19.3.2.18", {"start": v(64.93, 38.1) * mm, "end": v(65.41, 38.59) * mm});
            skCircle(sketch, "E19.3.3.0", {"center": v(84, 71.25) * mm, "radius": 2 * mm});
            skArc(sketch, "E19.3.3.1", {"start": v(81.41, 65.41) * mm, "mid": v(78.59, 65.41) * mm, "end": v(78.59, 62.59) * mm});
            skArc(sketch, "E19.3.3.2", {"start": v(62.1, 79.07) * mm, "mid": v(62.1, 81.9) * mm, "end": v(64.93, 81.9) * mm});
            skArc(sketch, "E19.3.3.3", {"start": v(65.41, 62.59) * mm, "mid": v(65.41, 65.41) * mm, "end": v(62.59, 65.41) * mm});
            skCircle(sketch, "E19.3.3.4", {"center": v(72, 84) * mm, "radius": 2 * mm});
            skArc(sketch, "E19.3.3.5", {"start": v(78.59, 81.41) * mm, "mid": v(78.59, 78.59) * mm, "end": v(81.41, 78.59) * mm});
            skArc(sketch, "E19.3.3.6", {"start": v(62.59, 78.59) * mm, "mid": v(65.41, 78.59) * mm, "end": v(65.41, 81.41) * mm});
            skCircle(sketch, "E19.3.3.7", {"center": v(72, 72) * mm, "radius": 7 * mm});
            skArc(sketch, "E19.3.3.8", {"start": v(81.9, 79.07) * mm, "mid": v(81.9, 81.9) * mm, "end": v(79.07, 81.9) * mm});
            skArc(sketch, "E19.3.3.9", {"start": v(79.07, 62.1) * mm, "mid": v(81.9, 62.1) * mm, "end": v(81.9, 64.93) * mm});
            skArc(sketch, "E19.3.3.10", {"start": v(62.1, 64.93) * mm, "mid": v(62.1, 62.1) * mm, "end": v(64.93, 62.1) * mm});
            skLineSegment(sketch, "E19.3.3.11", {"start": v(79.07, 62.1) * mm, "end": v(78.59, 62.59) * mm});
            skLineSegment(sketch, "E19.3.3.12", {"start": v(64.93, 81.9) * mm, "end": v(65.41, 81.41) * mm});
            skLineSegment(sketch, "E19.3.3.13", {"start": v(81.9, 79.07) * mm, "end": v(81.41, 78.59) * mm});
            skLineSegment(sketch, "E19.3.3.14", {"start": v(81.41, 65.41) * mm, "end": v(81.9, 64.93) * mm});
            skLineSegment(sketch, "E19.3.3.15", {"start": v(79.07, 81.9) * mm, "end": v(78.59, 81.41) * mm});
            skLineSegment(sketch, "E19.3.3.16", {"start": v(62.1, 79.07) * mm, "end": v(62.59, 78.59) * mm});
            skLineSegment(sketch, "E19.3.3.17", {"start": v(62.59, 65.41) * mm, "end": v(62.1, 64.93) * mm});
            skLineSegment(sketch, "E19.3.3.18", {"start": v(64.93, 62.1) * mm, "end": v(65.41, 62.59) * mm});
            skCircle(sketch, "E19.3.4.0", {"center": v(84, 95.25) * mm, "radius": 2 * mm});
            skArc(sketch, "E19.3.4.1", {"start": v(81.41, 89.41) * mm, "mid": v(78.59, 89.41) * mm, "end": v(78.59, 86.59) * mm});
            skArc(sketch, "E19.3.4.2", {"start": v(62.1, 103.07) * mm, "mid": v(62.1, 105.9) * mm, "end": v(64.93, 105.9) * mm});
            skArc(sketch, "E19.3.4.3", {"start": v(65.41, 86.59) * mm, "mid": v(65.41, 89.41) * mm, "end": v(62.59, 89.41) * mm});
            skCircle(sketch, "E19.3.4.4", {"center": v(72, 108) * mm, "radius": 2 * mm});
            skArc(sketch, "E19.3.4.5", {"start": v(78.59, 105.41) * mm, "mid": v(78.59, 102.59) * mm, "end": v(81.41, 102.59) * mm});
            skArc(sketch, "E19.3.4.6", {"start": v(62.59, 102.59) * mm, "mid": v(65.41, 102.59) * mm, "end": v(65.41, 105.41) * mm});
            skCircle(sketch, "E19.3.4.7", {"center": v(72, 96) * mm, "radius": 7 * mm});
            skArc(sketch, "E19.3.4.8", {"start": v(81.9, 103.07) * mm, "mid": v(81.9, 105.9) * mm, "end": v(79.07, 105.9) * mm});
            skArc(sketch, "E19.3.4.9", {"start": v(79.07, 86.1) * mm, "mid": v(81.9, 86.1) * mm, "end": v(81.9, 88.93) * mm});
            skArc(sketch, "E19.3.4.10", {"start": v(62.1, 88.93) * mm, "mid": v(62.1, 86.1) * mm, "end": v(64.93, 86.1) * mm});
            skLineSegment(sketch, "E19.3.4.11", {"start": v(79.07, 86.1) * mm, "end": v(78.59, 86.59) * mm});
            skLineSegment(sketch, "E19.3.4.12", {"start": v(64.93, 105.9) * mm, "end": v(65.41, 105.41) * mm});
            skLineSegment(sketch, "E19.3.4.13", {"start": v(81.9, 103.07) * mm, "end": v(81.41, 102.59) * mm});
            skLineSegment(sketch, "E19.3.4.14", {"start": v(81.41, 89.41) * mm, "end": v(81.9, 88.93) * mm});
            skLineSegment(sketch, "E19.3.4.15", {"start": v(79.07, 105.9) * mm, "end": v(78.59, 105.41) * mm});
            skLineSegment(sketch, "E19.3.4.16", {"start": v(62.1, 103.07) * mm, "end": v(62.59, 102.59) * mm});
            skLineSegment(sketch, "E19.3.4.17", {"start": v(62.59, 89.41) * mm, "end": v(62.1, 88.93) * mm});
            skLineSegment(sketch, "E19.3.4.18", {"start": v(64.93, 86.1) * mm, "end": v(65.41, 86.59) * mm});
            skCircle(sketch, "E19.3.5.0", {"center": v(84, 119.25) * mm, "radius": 2 * mm});
            skArc(sketch, "E19.3.5.1", {"start": v(81.41, 113.41) * mm, "mid": v(78.59, 113.41) * mm, "end": v(78.59, 110.59) * mm});
            skArc(sketch, "E19.3.5.2", {"start": v(62.1, 127.07) * mm, "mid": v(62.1, 129.9) * mm, "end": v(64.93, 129.9) * mm});
            skArc(sketch, "E19.3.5.3", {"start": v(65.41, 110.59) * mm, "mid": v(65.41, 113.41) * mm, "end": v(62.59, 113.41) * mm});
            skCircle(sketch, "E19.3.5.4", {"center": v(72, 132) * mm, "radius": 2 * mm});
            skArc(sketch, "E19.3.5.5", {"start": v(78.59, 129.41) * mm, "mid": v(78.59, 126.59) * mm, "end": v(81.41, 126.59) * mm});
            skArc(sketch, "E19.3.5.6", {"start": v(62.59, 126.59) * mm, "mid": v(65.41, 126.59) * mm, "end": v(65.41, 129.41) * mm});
            skCircle(sketch, "E19.3.5.7", {"center": v(72, 120) * mm, "radius": 7 * mm});
            skArc(sketch, "E19.3.5.8", {"start": v(81.9, 127.07) * mm, "mid": v(81.9, 129.9) * mm, "end": v(79.07, 129.9) * mm});
            skArc(sketch, "E19.3.5.9", {"start": v(79.07, 110.1) * mm, "mid": v(81.9, 110.1) * mm, "end": v(81.9, 112.93) * mm});
            skArc(sketch, "E19.3.5.10", {"start": v(62.1, 112.93) * mm, "mid": v(62.1, 110.1) * mm, "end": v(64.93, 110.1) * mm});
            skLineSegment(sketch, "E19.3.5.11", {"start": v(79.07, 110.1) * mm, "end": v(78.59, 110.59) * mm});
            skLineSegment(sketch, "E19.3.5.12", {"start": v(64.93, 129.9) * mm, "end": v(65.41, 129.41) * mm});
            skLineSegment(sketch, "E19.3.5.13", {"start": v(81.9, 127.07) * mm, "end": v(81.41, 126.59) * mm});
            skLineSegment(sketch, "E19.3.5.14", {"start": v(81.41, 113.41) * mm, "end": v(81.9, 112.93) * mm});
            skLineSegment(sketch, "E19.3.5.15", {"start": v(79.07, 129.9) * mm, "end": v(78.59, 129.41) * mm});
            skLineSegment(sketch, "E19.3.5.16", {"start": v(62.1, 127.07) * mm, "end": v(62.59, 126.59) * mm});
            skLineSegment(sketch, "E19.3.5.17", {"start": v(62.59, 113.41) * mm, "end": v(62.1, 112.93) * mm});
            skLineSegment(sketch, "E19.3.5.18", {"start": v(64.93, 110.1) * mm, "end": v(65.41, 110.59) * mm});
            skCircle(sketch, "E19.3.6.0", {"center": v(84, 143.25) * mm, "radius": 2 * mm});
            skArc(sketch, "E19.3.6.1", {"start": v(81.41, 137.41) * mm, "mid": v(78.59, 137.41) * mm, "end": v(78.59, 134.59) * mm});
            skArc(sketch, "E19.3.6.2", {"start": v(62.1, 151.07) * mm, "mid": v(62.1, 153.9) * mm, "end": v(64.93, 153.9) * mm});
            skArc(sketch, "E19.3.6.3", {"start": v(65.41, 134.59) * mm, "mid": v(65.41, 137.41) * mm, "end": v(62.59, 137.41) * mm});
            skCircle(sketch, "E19.3.6.4", {"center": v(72, 156) * mm, "radius": 2 * mm});
            skArc(sketch, "E19.3.6.5", {"start": v(78.59, 153.41) * mm, "mid": v(78.59, 150.59) * mm, "end": v(81.41, 150.59) * mm});
            skArc(sketch, "E19.3.6.6", {"start": v(62.59, 150.59) * mm, "mid": v(65.41, 150.59) * mm, "end": v(65.41, 153.41) * mm});
            skCircle(sketch, "E19.3.6.7", {"center": v(72, 144) * mm, "radius": 7 * mm});
            skArc(sketch, "E19.3.6.8", {"start": v(81.9, 151.07) * mm, "mid": v(81.9, 153.9) * mm, "end": v(79.07, 153.9) * mm});
            skArc(sketch, "E19.3.6.9", {"start": v(79.07, 134.1) * mm, "mid": v(81.9, 134.1) * mm, "end": v(81.9, 136.93) * mm});
            skArc(sketch, "E19.3.6.10", {"start": v(62.1, 136.93) * mm, "mid": v(62.1, 134.1) * mm, "end": v(64.93, 134.1) * mm});
            skLineSegment(sketch, "E19.3.6.11", {"start": v(79.07, 134.1) * mm, "end": v(78.59, 134.59) * mm});
            skLineSegment(sketch, "E19.3.6.12", {"start": v(64.93, 153.9) * mm, "end": v(65.41, 153.41) * mm});
            skLineSegment(sketch, "E19.3.6.13", {"start": v(81.9, 151.07) * mm, "end": v(81.41, 150.59) * mm});
            skLineSegment(sketch, "E19.3.6.14", {"start": v(81.41, 137.41) * mm, "end": v(81.9, 136.93) * mm});
            skLineSegment(sketch, "E19.3.6.15", {"start": v(79.07, 153.9) * mm, "end": v(78.59, 153.41) * mm});
            skLineSegment(sketch, "E19.3.6.16", {"start": v(62.1, 151.07) * mm, "end": v(62.59, 150.59) * mm});
            skLineSegment(sketch, "E19.3.6.17", {"start": v(62.59, 137.41) * mm, "end": v(62.1, 136.93) * mm});
            skLineSegment(sketch, "E19.3.6.18", {"start": v(64.93, 134.1) * mm, "end": v(65.41, 134.59) * mm});
            skCircle(sketch, "E19.3.7.0", {"center": v(84, 167.25) * mm, "radius": 2 * mm});
            skArc(sketch, "E19.3.7.1", {"start": v(81.41, 161.41) * mm, "mid": v(78.59, 161.41) * mm, "end": v(78.59, 158.59) * mm});
            skArc(sketch, "E19.3.7.2", {"start": v(62.1, 175.07) * mm, "mid": v(62.1, 177.9) * mm, "end": v(64.93, 177.9) * mm});
            skArc(sketch, "E19.3.7.3", {"start": v(65.41, 158.59) * mm, "mid": v(65.41, 161.41) * mm, "end": v(62.59, 161.41) * mm});
            skCircle(sketch, "E19.3.7.4", {"center": v(72, 180) * mm, "radius": 2 * mm});
            skArc(sketch, "E19.3.7.5", {"start": v(78.59, 177.41) * mm, "mid": v(78.59, 174.59) * mm, "end": v(81.41, 174.59) * mm});
            skArc(sketch, "E19.3.7.6", {"start": v(62.59, 174.59) * mm, "mid": v(65.41, 174.59) * mm, "end": v(65.41, 177.41) * mm});
            skCircle(sketch, "E19.3.7.7", {"center": v(72, 168) * mm, "radius": 7 * mm});
            skArc(sketch, "E19.3.7.8", {"start": v(81.9, 175.07) * mm, "mid": v(81.9, 177.9) * mm, "end": v(79.07, 177.9) * mm});
            skArc(sketch, "E19.3.7.9", {"start": v(79.07, 158.1) * mm, "mid": v(81.9, 158.1) * mm, "end": v(81.9, 160.93) * mm});
            skArc(sketch, "E19.3.7.10", {"start": v(62.1, 160.93) * mm, "mid": v(62.1, 158.1) * mm, "end": v(64.93, 158.1) * mm});
            skLineSegment(sketch, "E19.3.7.11", {"start": v(79.07, 158.1) * mm, "end": v(78.59, 158.59) * mm});
            skLineSegment(sketch, "E19.3.7.12", {"start": v(64.93, 177.9) * mm, "end": v(65.41, 177.41) * mm});
            skLineSegment(sketch, "E19.3.7.13", {"start": v(81.9, 175.07) * mm, "end": v(81.41, 174.59) * mm});
            skLineSegment(sketch, "E19.3.7.14", {"start": v(81.41, 161.41) * mm, "end": v(81.9, 160.93) * mm});
            skLineSegment(sketch, "E19.3.7.15", {"start": v(79.07, 177.9) * mm, "end": v(78.59, 177.41) * mm});
            skLineSegment(sketch, "E19.3.7.16", {"start": v(62.1, 175.07) * mm, "end": v(62.59, 174.59) * mm});
            skLineSegment(sketch, "E19.3.7.17", {"start": v(62.59, 161.41) * mm, "end": v(62.1, 160.93) * mm});
            skLineSegment(sketch, "E19.3.7.18", {"start": v(64.93, 158.1) * mm, "end": v(65.41, 158.59) * mm});
            skCircle(sketch, "E19.3.8.0", {"center": v(84, 191.25) * mm, "radius": 2 * mm});
            skArc(sketch, "E19.3.8.1", {"start": v(81.41, 185.41) * mm, "mid": v(78.59, 185.41) * mm, "end": v(78.59, 182.59) * mm});
            skArc(sketch, "E19.3.8.2", {"start": v(62.1, 199.07) * mm, "mid": v(62.1, 201.9) * mm, "end": v(64.93, 201.9) * mm});
            skArc(sketch, "E19.3.8.3", {"start": v(65.41, 182.59) * mm, "mid": v(65.41, 185.41) * mm, "end": v(62.59, 185.41) * mm});
            skCircle(sketch, "E19.3.8.4", {"center": v(72, 204) * mm, "radius": 2 * mm});
            skArc(sketch, "E19.3.8.5", {"start": v(78.59, 201.41) * mm, "mid": v(78.59, 198.59) * mm, "end": v(81.41, 198.59) * mm});
            skArc(sketch, "E19.3.8.6", {"start": v(62.59, 198.59) * mm, "mid": v(65.41, 198.59) * mm, "end": v(65.41, 201.41) * mm});
            skCircle(sketch, "E19.3.8.7", {"center": v(72, 192) * mm, "radius": 7 * mm});
            skArc(sketch, "E19.3.8.8", {"start": v(81.9, 199.07) * mm, "mid": v(81.9, 201.9) * mm, "end": v(79.07, 201.9) * mm});
            skArc(sketch, "E19.3.8.9", {"start": v(79.07, 182.1) * mm, "mid": v(81.9, 182.1) * mm, "end": v(81.9, 184.93) * mm});
            skArc(sketch, "E19.3.8.10", {"start": v(62.1, 184.93) * mm, "mid": v(62.1, 182.1) * mm, "end": v(64.93, 182.1) * mm});
            skLineSegment(sketch, "E19.3.8.11", {"start": v(79.07, 182.1) * mm, "end": v(78.59, 182.59) * mm});
            skLineSegment(sketch, "E19.3.8.12", {"start": v(64.93, 201.9) * mm, "end": v(65.41, 201.41) * mm});
            skLineSegment(sketch, "E19.3.8.13", {"start": v(81.9, 199.07) * mm, "end": v(81.41, 198.59) * mm});
            skLineSegment(sketch, "E19.3.8.14", {"start": v(81.41, 185.41) * mm, "end": v(81.9, 184.93) * mm});
            skLineSegment(sketch, "E19.3.8.15", {"start": v(79.07, 201.9) * mm, "end": v(78.59, 201.41) * mm});
            skLineSegment(sketch, "E19.3.8.16", {"start": v(62.1, 199.07) * mm, "end": v(62.59, 198.59) * mm});
            skLineSegment(sketch, "E19.3.8.17", {"start": v(62.59, 185.41) * mm, "end": v(62.1, 184.93) * mm});
            skLineSegment(sketch, "E19.3.8.18", {"start": v(64.93, 182.1) * mm, "end": v(65.41, 182.59) * mm});
            skCircle(sketch, "E19.4.0.0", {"center": v(108, -0.75) * mm, "radius": 2 * mm});
            skArc(sketch, "E19.4.0.1", {"start": v(105.41, -6.59) * mm, "mid": v(102.59, -6.59) * mm, "end": v(102.59, -9.41) * mm});
            skArc(sketch, "E19.4.0.2", {"start": v(86.1, 7.07) * mm, "mid": v(86.1, 9.9) * mm, "end": v(88.93, 9.9) * mm});
            skArc(sketch, "E19.4.0.3", {"start": v(89.41, -9.41) * mm, "mid": v(89.41, -6.59) * mm, "end": v(86.59, -6.59) * mm});
            skCircle(sketch, "E19.4.0.4", {"center": v(96, 12) * mm, "radius": 2 * mm});
            skArc(sketch, "E19.4.0.5", {"start": v(102.59, 9.41) * mm, "mid": v(102.59, 6.59) * mm, "end": v(105.41, 6.59) * mm});
            skArc(sketch, "E19.4.0.6", {"start": v(86.59, 6.59) * mm, "mid": v(89.41, 6.59) * mm, "end": v(89.41, 9.41) * mm});
            skCircle(sketch, "E19.4.0.7", {"center": v(96, 0) * mm, "radius": 7 * mm});
            skArc(sketch, "E19.4.0.8", {"start": v(105.9, 7.07) * mm, "mid": v(105.9, 9.9) * mm, "end": v(103.07, 9.9) * mm});
            skArc(sketch, "E19.4.0.9", {"start": v(103.07, -9.9) * mm, "mid": v(105.9, -9.9) * mm, "end": v(105.9, -7.07) * mm});
            skArc(sketch, "E19.4.0.10", {"start": v(86.1, -7.07) * mm, "mid": v(86.1, -9.9) * mm, "end": v(88.93, -9.9) * mm});
            skLineSegment(sketch, "E19.4.0.11", {"start": v(103.07, -9.9) * mm, "end": v(102.59, -9.41) * mm});
            skLineSegment(sketch, "E19.4.0.12", {"start": v(88.93, 9.9) * mm, "end": v(89.41, 9.41) * mm});
            skLineSegment(sketch, "E19.4.0.13", {"start": v(105.9, 7.07) * mm, "end": v(105.41, 6.59) * mm});
            skLineSegment(sketch, "E19.4.0.14", {"start": v(105.41, -6.59) * mm, "end": v(105.9, -7.07) * mm});
            skLineSegment(sketch, "E19.4.0.15", {"start": v(103.07, 9.9) * mm, "end": v(102.59, 9.41) * mm});
            skLineSegment(sketch, "E19.4.0.16", {"start": v(86.1, 7.07) * mm, "end": v(86.59, 6.59) * mm});
            skLineSegment(sketch, "E19.4.0.17", {"start": v(86.59, -6.59) * mm, "end": v(86.1, -7.07) * mm});
            skLineSegment(sketch, "E19.4.0.18", {"start": v(88.93, -9.9) * mm, "end": v(89.41, -9.41) * mm});
            skCircle(sketch, "E19.4.1.0", {"center": v(108, 23.25) * mm, "radius": 2 * mm});
            skArc(sketch, "E19.4.1.1", {"start": v(105.41, 17.41) * mm, "mid": v(102.59, 17.41) * mm, "end": v(102.59, 14.59) * mm});
            skArc(sketch, "E19.4.1.2", {"start": v(86.1, 31.07) * mm, "mid": v(86.1, 33.9) * mm, "end": v(88.93, 33.9) * mm});
            skArc(sketch, "E19.4.1.3", {"start": v(89.41, 14.59) * mm, "mid": v(89.41, 17.41) * mm, "end": v(86.59, 17.41) * mm});
            skCircle(sketch, "E19.4.1.4", {"center": v(96, 36) * mm, "radius": 2 * mm});
            skArc(sketch, "E19.4.1.5", {"start": v(102.59, 33.41) * mm, "mid": v(102.59, 30.59) * mm, "end": v(105.41, 30.59) * mm});
            skArc(sketch, "E19.4.1.6", {"start": v(86.59, 30.59) * mm, "mid": v(89.41, 30.59) * mm, "end": v(89.41, 33.41) * mm});
            skCircle(sketch, "E19.4.1.7", {"center": v(96, 24) * mm, "radius": 7 * mm});
            skArc(sketch, "E19.4.1.8", {"start": v(105.9, 31.07) * mm, "mid": v(105.9, 33.9) * mm, "end": v(103.07, 33.9) * mm});
            skArc(sketch, "E19.4.1.9", {"start": v(103.07, 14.1) * mm, "mid": v(105.9, 14.1) * mm, "end": v(105.9, 16.93) * mm});
            skArc(sketch, "E19.4.1.10", {"start": v(86.1, 16.93) * mm, "mid": v(86.1, 14.1) * mm, "end": v(88.93, 14.1) * mm});
            skLineSegment(sketch, "E19.4.1.11", {"start": v(103.07, 14.1) * mm, "end": v(102.59, 14.59) * mm});
            skLineSegment(sketch, "E19.4.1.12", {"start": v(88.93, 33.9) * mm, "end": v(89.41, 33.41) * mm});
            skLineSegment(sketch, "E19.4.1.13", {"start": v(105.9, 31.07) * mm, "end": v(105.41, 30.59) * mm});
            skLineSegment(sketch, "E19.4.1.14", {"start": v(105.41, 17.41) * mm, "end": v(105.9, 16.93) * mm});
            skLineSegment(sketch, "E19.4.1.15", {"start": v(103.07, 33.9) * mm, "end": v(102.59, 33.41) * mm});
            skLineSegment(sketch, "E19.4.1.16", {"start": v(86.1, 31.07) * mm, "end": v(86.59, 30.59) * mm});
            skLineSegment(sketch, "E19.4.1.17", {"start": v(86.59, 17.41) * mm, "end": v(86.1, 16.93) * mm});
            skLineSegment(sketch, "E19.4.1.18", {"start": v(88.93, 14.1) * mm, "end": v(89.41, 14.59) * mm});
            skCircle(sketch, "E19.4.2.0", {"center": v(108, 47.25) * mm, "radius": 2 * mm});
            skArc(sketch, "E19.4.2.1", {"start": v(105.41, 41.41) * mm, "mid": v(102.59, 41.41) * mm, "end": v(102.59, 38.59) * mm});
            skArc(sketch, "E19.4.2.2", {"start": v(86.1, 55.07) * mm, "mid": v(86.1, 57.9) * mm, "end": v(88.93, 57.9) * mm});
            skArc(sketch, "E19.4.2.3", {"start": v(89.41, 38.59) * mm, "mid": v(89.41, 41.41) * mm, "end": v(86.59, 41.41) * mm});
            skCircle(sketch, "E19.4.2.4", {"center": v(96, 60) * mm, "radius": 2 * mm});
            skArc(sketch, "E19.4.2.5", {"start": v(102.59, 57.41) * mm, "mid": v(102.59, 54.59) * mm, "end": v(105.41, 54.59) * mm});
            skArc(sketch, "E19.4.2.6", {"start": v(86.59, 54.59) * mm, "mid": v(89.41, 54.59) * mm, "end": v(89.41, 57.41) * mm});
            skCircle(sketch, "E19.4.2.7", {"center": v(96, 48) * mm, "radius": 7 * mm});
            skArc(sketch, "E19.4.2.8", {"start": v(105.9, 55.07) * mm, "mid": v(105.9, 57.9) * mm, "end": v(103.07, 57.9) * mm});
            skArc(sketch, "E19.4.2.9", {"start": v(103.07, 38.1) * mm, "mid": v(105.9, 38.1) * mm, "end": v(105.9, 40.93) * mm});
            skArc(sketch, "E19.4.2.10", {"start": v(86.1, 40.93) * mm, "mid": v(86.1, 38.1) * mm, "end": v(88.93, 38.1) * mm});
            skLineSegment(sketch, "E19.4.2.11", {"start": v(103.07, 38.1) * mm, "end": v(102.59, 38.59) * mm});
            skLineSegment(sketch, "E19.4.2.12", {"start": v(88.93, 57.9) * mm, "end": v(89.41, 57.41) * mm});
            skLineSegment(sketch, "E19.4.2.13", {"start": v(105.9, 55.07) * mm, "end": v(105.41, 54.59) * mm});
            skLineSegment(sketch, "E19.4.2.14", {"start": v(105.41, 41.41) * mm, "end": v(105.9, 40.93) * mm});
            skLineSegment(sketch, "E19.4.2.15", {"start": v(103.07, 57.9) * mm, "end": v(102.59, 57.41) * mm});
            skLineSegment(sketch, "E19.4.2.16", {"start": v(86.1, 55.07) * mm, "end": v(86.59, 54.59) * mm});
            skLineSegment(sketch, "E19.4.2.17", {"start": v(86.59, 41.41) * mm, "end": v(86.1, 40.93) * mm});
            skLineSegment(sketch, "E19.4.2.18", {"start": v(88.93, 38.1) * mm, "end": v(89.41, 38.59) * mm});
            skCircle(sketch, "E19.4.3.0", {"center": v(108, 71.25) * mm, "radius": 2 * mm});
            skArc(sketch, "E19.4.3.1", {"start": v(105.41, 65.41) * mm, "mid": v(102.59, 65.41) * mm, "end": v(102.59, 62.59) * mm});
            skArc(sketch, "E19.4.3.2", {"start": v(86.1, 79.07) * mm, "mid": v(86.1, 81.9) * mm, "end": v(88.93, 81.9) * mm});
            skArc(sketch, "E19.4.3.3", {"start": v(89.41, 62.59) * mm, "mid": v(89.41, 65.41) * mm, "end": v(86.59, 65.41) * mm});
            skCircle(sketch, "E19.4.3.4", {"center": v(96, 84) * mm, "radius": 2 * mm});
            skArc(sketch, "E19.4.3.5", {"start": v(102.59, 81.41) * mm, "mid": v(102.59, 78.59) * mm, "end": v(105.41, 78.59) * mm});
            skArc(sketch, "E19.4.3.6", {"start": v(86.59, 78.59) * mm, "mid": v(89.41, 78.59) * mm, "end": v(89.41, 81.41) * mm});
            skCircle(sketch, "E19.4.3.7", {"center": v(96, 72) * mm, "radius": 7 * mm});
            skArc(sketch, "E19.4.3.8", {"start": v(105.9, 79.07) * mm, "mid": v(105.9, 81.9) * mm, "end": v(103.07, 81.9) * mm});
            skArc(sketch, "E19.4.3.9", {"start": v(103.07, 62.1) * mm, "mid": v(105.9, 62.1) * mm, "end": v(105.9, 64.93) * mm});
            skArc(sketch, "E19.4.3.10", {"start": v(86.1, 64.93) * mm, "mid": v(86.1, 62.1) * mm, "end": v(88.93, 62.1) * mm});
            skLineSegment(sketch, "E19.4.3.11", {"start": v(103.07, 62.1) * mm, "end": v(102.59, 62.59) * mm});
            skLineSegment(sketch, "E19.4.3.12", {"start": v(88.93, 81.9) * mm, "end": v(89.41, 81.41) * mm});
            skLineSegment(sketch, "E19.4.3.13", {"start": v(105.9, 79.07) * mm, "end": v(105.41, 78.59) * mm});
            skLineSegment(sketch, "E19.4.3.14", {"start": v(105.41, 65.41) * mm, "end": v(105.9, 64.93) * mm});
            skLineSegment(sketch, "E19.4.3.15", {"start": v(103.07, 81.9) * mm, "end": v(102.59, 81.41) * mm});
            skLineSegment(sketch, "E19.4.3.16", {"start": v(86.1, 79.07) * mm, "end": v(86.59, 78.59) * mm});
            skLineSegment(sketch, "E19.4.3.17", {"start": v(86.59, 65.41) * mm, "end": v(86.1, 64.93) * mm});
            skLineSegment(sketch, "E19.4.3.18", {"start": v(88.93, 62.1) * mm, "end": v(89.41, 62.59) * mm});
            skCircle(sketch, "E19.4.4.0", {"center": v(108, 95.25) * mm, "radius": 2 * mm});
            skArc(sketch, "E19.4.4.1", {"start": v(105.41, 89.41) * mm, "mid": v(102.59, 89.41) * mm, "end": v(102.59, 86.59) * mm});
            skArc(sketch, "E19.4.4.2", {"start": v(86.1, 103.07) * mm, "mid": v(86.1, 105.9) * mm, "end": v(88.93, 105.9) * mm});
            skArc(sketch, "E19.4.4.3", {"start": v(89.41, 86.59) * mm, "mid": v(89.41, 89.41) * mm, "end": v(86.59, 89.41) * mm});
            skCircle(sketch, "E19.4.4.4", {"center": v(96, 108) * mm, "radius": 2 * mm});
            skArc(sketch, "E19.4.4.5", {"start": v(102.59, 105.41) * mm, "mid": v(102.59, 102.59) * mm, "end": v(105.41, 102.59) * mm});
            skArc(sketch, "E19.4.4.6", {"start": v(86.59, 102.59) * mm, "mid": v(89.41, 102.59) * mm, "end": v(89.41, 105.41) * mm});
            skCircle(sketch, "E19.4.4.7", {"center": v(96, 96) * mm, "radius": 7 * mm});
            skArc(sketch, "E19.4.4.8", {"start": v(105.9, 103.07) * mm, "mid": v(105.9, 105.9) * mm, "end": v(103.07, 105.9) * mm});
            skArc(sketch, "E19.4.4.9", {"start": v(103.07, 86.1) * mm, "mid": v(105.9, 86.1) * mm, "end": v(105.9, 88.93) * mm});
            skArc(sketch, "E19.4.4.10", {"start": v(86.1, 88.93) * mm, "mid": v(86.1, 86.1) * mm, "end": v(88.93, 86.1) * mm});
            skLineSegment(sketch, "E19.4.4.11", {"start": v(103.07, 86.1) * mm, "end": v(102.59, 86.59) * mm});
            skLineSegment(sketch, "E19.4.4.12", {"start": v(88.93, 105.9) * mm, "end": v(89.41, 105.41) * mm});
            skLineSegment(sketch, "E19.4.4.13", {"start": v(105.9, 103.07) * mm, "end": v(105.41, 102.59) * mm});
            skLineSegment(sketch, "E19.4.4.14", {"start": v(105.41, 89.41) * mm, "end": v(105.9, 88.93) * mm});
            skLineSegment(sketch, "E19.4.4.15", {"start": v(103.07, 105.9) * mm, "end": v(102.59, 105.41) * mm});
            skLineSegment(sketch, "E19.4.4.16", {"start": v(86.1, 103.07) * mm, "end": v(86.59, 102.59) * mm});
            skLineSegment(sketch, "E19.4.4.17", {"start": v(86.59, 89.41) * mm, "end": v(86.1, 88.93) * mm});
            skLineSegment(sketch, "E19.4.4.18", {"start": v(88.93, 86.1) * mm, "end": v(89.41, 86.59) * mm});
            skCircle(sketch, "E19.4.5.0", {"center": v(108, 119.25) * mm, "radius": 2 * mm});
            skArc(sketch, "E19.4.5.1", {"start": v(105.41, 113.41) * mm, "mid": v(102.59, 113.41) * mm, "end": v(102.59, 110.59) * mm});
            skArc(sketch, "E19.4.5.2", {"start": v(86.1, 127.07) * mm, "mid": v(86.1, 129.9) * mm, "end": v(88.93, 129.9) * mm});
            skArc(sketch, "E19.4.5.3", {"start": v(89.41, 110.59) * mm, "mid": v(89.41, 113.41) * mm, "end": v(86.59, 113.41) * mm});
            skCircle(sketch, "E19.4.5.4", {"center": v(96, 132) * mm, "radius": 2 * mm});
            skArc(sketch, "E19.4.5.5", {"start": v(102.59, 129.41) * mm, "mid": v(102.59, 126.59) * mm, "end": v(105.41, 126.59) * mm});
            skArc(sketch, "E19.4.5.6", {"start": v(86.59, 126.59) * mm, "mid": v(89.41, 126.59) * mm, "end": v(89.41, 129.41) * mm});
            skCircle(sketch, "E19.4.5.7", {"center": v(96, 120) * mm, "radius": 7 * mm});
            skArc(sketch, "E19.4.5.8", {"start": v(105.9, 127.07) * mm, "mid": v(105.9, 129.9) * mm, "end": v(103.07, 129.9) * mm});
            skArc(sketch, "E19.4.5.9", {"start": v(103.07, 110.1) * mm, "mid": v(105.9, 110.1) * mm, "end": v(105.9, 112.93) * mm});
            skArc(sketch, "E19.4.5.10", {"start": v(86.1, 112.93) * mm, "mid": v(86.1, 110.1) * mm, "end": v(88.93, 110.1) * mm});
            skLineSegment(sketch, "E19.4.5.11", {"start": v(103.07, 110.1) * mm, "end": v(102.59, 110.59) * mm});
            skLineSegment(sketch, "E19.4.5.12", {"start": v(88.93, 129.9) * mm, "end": v(89.41, 129.41) * mm});
            skLineSegment(sketch, "E19.4.5.13", {"start": v(105.9, 127.07) * mm, "end": v(105.41, 126.59) * mm});
            skLineSegment(sketch, "E19.4.5.14", {"start": v(105.41, 113.41) * mm, "end": v(105.9, 112.93) * mm});
            skLineSegment(sketch, "E19.4.5.15", {"start": v(103.07, 129.9) * mm, "end": v(102.59, 129.41) * mm});
            skLineSegment(sketch, "E19.4.5.16", {"start": v(86.1, 127.07) * mm, "end": v(86.59, 126.59) * mm});
            skLineSegment(sketch, "E19.4.5.17", {"start": v(86.59, 113.41) * mm, "end": v(86.1, 112.93) * mm});
            skLineSegment(sketch, "E19.4.5.18", {"start": v(88.93, 110.1) * mm, "end": v(89.41, 110.59) * mm});
            skCircle(sketch, "E19.4.6.0", {"center": v(108, 143.25) * mm, "radius": 2 * mm});
            skArc(sketch, "E19.4.6.1", {"start": v(105.41, 137.41) * mm, "mid": v(102.59, 137.41) * mm, "end": v(102.59, 134.59) * mm});
            skArc(sketch, "E19.4.6.2", {"start": v(86.1, 151.07) * mm, "mid": v(86.1, 153.9) * mm, "end": v(88.93, 153.9) * mm});
            skArc(sketch, "E19.4.6.3", {"start": v(89.41, 134.59) * mm, "mid": v(89.41, 137.41) * mm, "end": v(86.59, 137.41) * mm});
            skCircle(sketch, "E19.4.6.4", {"center": v(96, 156) * mm, "radius": 2 * mm});
            skArc(sketch, "E19.4.6.5", {"start": v(102.59, 153.41) * mm, "mid": v(102.59, 150.59) * mm, "end": v(105.41, 150.59) * mm});
            skArc(sketch, "E19.4.6.6", {"start": v(86.59, 150.59) * mm, "mid": v(89.41, 150.59) * mm, "end": v(89.41, 153.41) * mm});
            skCircle(sketch, "E19.4.6.7", {"center": v(96, 144) * mm, "radius": 7 * mm});
            skArc(sketch, "E19.4.6.8", {"start": v(105.9, 151.07) * mm, "mid": v(105.9, 153.9) * mm, "end": v(103.07, 153.9) * mm});
            skArc(sketch, "E19.4.6.9", {"start": v(103.07, 134.1) * mm, "mid": v(105.9, 134.1) * mm, "end": v(105.9, 136.93) * mm});
            skArc(sketch, "E19.4.6.10", {"start": v(86.1, 136.93) * mm, "mid": v(86.1, 134.1) * mm, "end": v(88.93, 134.1) * mm});
            skLineSegment(sketch, "E19.4.6.11", {"start": v(103.07, 134.1) * mm, "end": v(102.59, 134.59) * mm});
            skLineSegment(sketch, "E19.4.6.12", {"start": v(88.93, 153.9) * mm, "end": v(89.41, 153.41) * mm});
            skLineSegment(sketch, "E19.4.6.13", {"start": v(105.9, 151.07) * mm, "end": v(105.41, 150.59) * mm});
            skLineSegment(sketch, "E19.4.6.14", {"start": v(105.41, 137.41) * mm, "end": v(105.9, 136.93) * mm});
            skLineSegment(sketch, "E19.4.6.15", {"start": v(103.07, 153.9) * mm, "end": v(102.59, 153.41) * mm});
            skLineSegment(sketch, "E19.4.6.16", {"start": v(86.1, 151.07) * mm, "end": v(86.59, 150.59) * mm});
            skLineSegment(sketch, "E19.4.6.17", {"start": v(86.59, 137.41) * mm, "end": v(86.1, 136.93) * mm});
            skLineSegment(sketch, "E19.4.6.18", {"start": v(88.93, 134.1) * mm, "end": v(89.41, 134.59) * mm});
            skCircle(sketch, "E19.4.7.0", {"center": v(108, 167.25) * mm, "radius": 2 * mm});
            skArc(sketch, "E19.4.7.1", {"start": v(105.41, 161.41) * mm, "mid": v(102.59, 161.41) * mm, "end": v(102.59, 158.59) * mm});
            skArc(sketch, "E19.4.7.2", {"start": v(86.1, 175.07) * mm, "mid": v(86.1, 177.9) * mm, "end": v(88.93, 177.9) * mm});
            skArc(sketch, "E19.4.7.3", {"start": v(89.41, 158.59) * mm, "mid": v(89.41, 161.41) * mm, "end": v(86.59, 161.41) * mm});
            skCircle(sketch, "E19.4.7.4", {"center": v(96, 180) * mm, "radius": 2 * mm});
            skArc(sketch, "E19.4.7.5", {"start": v(102.59, 177.41) * mm, "mid": v(102.59, 174.59) * mm, "end": v(105.41, 174.59) * mm});
            skArc(sketch, "E19.4.7.6", {"start": v(86.59, 174.59) * mm, "mid": v(89.41, 174.59) * mm, "end": v(89.41, 177.41) * mm});
            skCircle(sketch, "E19.4.7.7", {"center": v(96, 168) * mm, "radius": 7 * mm});
            skArc(sketch, "E19.4.7.8", {"start": v(105.9, 175.07) * mm, "mid": v(105.9, 177.9) * mm, "end": v(103.07, 177.9) * mm});
            skArc(sketch, "E19.4.7.9", {"start": v(103.07, 158.1) * mm, "mid": v(105.9, 158.1) * mm, "end": v(105.9, 160.93) * mm});
            skArc(sketch, "E19.4.7.10", {"start": v(86.1, 160.93) * mm, "mid": v(86.1, 158.1) * mm, "end": v(88.93, 158.1) * mm});
            skLineSegment(sketch, "E19.4.7.11", {"start": v(103.07, 158.1) * mm, "end": v(102.59, 158.59) * mm});
            skLineSegment(sketch, "E19.4.7.12", {"start": v(88.93, 177.9) * mm, "end": v(89.41, 177.41) * mm});
            skLineSegment(sketch, "E19.4.7.13", {"start": v(105.9, 175.07) * mm, "end": v(105.41, 174.59) * mm});
            skLineSegment(sketch, "E19.4.7.14", {"start": v(105.41, 161.41) * mm, "end": v(105.9, 160.93) * mm});
            skLineSegment(sketch, "E19.4.7.15", {"start": v(103.07, 177.9) * mm, "end": v(102.59, 177.41) * mm});
            skLineSegment(sketch, "E19.4.7.16", {"start": v(86.1, 175.07) * mm, "end": v(86.59, 174.59) * mm});
            skLineSegment(sketch, "E19.4.7.17", {"start": v(86.59, 161.41) * mm, "end": v(86.1, 160.93) * mm});
            skLineSegment(sketch, "E19.4.7.18", {"start": v(88.93, 158.1) * mm, "end": v(89.41, 158.59) * mm});
            skCircle(sketch, "E19.4.8.0", {"center": v(108, 191.25) * mm, "radius": 2 * mm});
            skArc(sketch, "E19.4.8.1", {"start": v(105.41, 185.41) * mm, "mid": v(102.59, 185.41) * mm, "end": v(102.59, 182.59) * mm});
            skArc(sketch, "E19.4.8.2", {"start": v(86.1, 199.07) * mm, "mid": v(86.1, 201.9) * mm, "end": v(88.93, 201.9) * mm});
            skArc(sketch, "E19.4.8.3", {"start": v(89.41, 182.59) * mm, "mid": v(89.41, 185.41) * mm, "end": v(86.59, 185.41) * mm});
            skCircle(sketch, "E19.4.8.4", {"center": v(96, 204) * mm, "radius": 2 * mm});
            skArc(sketch, "E19.4.8.5", {"start": v(102.59, 201.41) * mm, "mid": v(102.59, 198.59) * mm, "end": v(105.41, 198.59) * mm});
            skArc(sketch, "E19.4.8.6", {"start": v(86.59, 198.59) * mm, "mid": v(89.41, 198.59) * mm, "end": v(89.41, 201.41) * mm});
            skCircle(sketch, "E19.4.8.7", {"center": v(96, 192) * mm, "radius": 7 * mm});
            skArc(sketch, "E19.4.8.8", {"start": v(105.9, 199.07) * mm, "mid": v(105.9, 201.9) * mm, "end": v(103.07, 201.9) * mm});
            skArc(sketch, "E19.4.8.9", {"start": v(103.07, 182.1) * mm, "mid": v(105.9, 182.1) * mm, "end": v(105.9, 184.93) * mm});
            skArc(sketch, "E19.4.8.10", {"start": v(86.1, 184.93) * mm, "mid": v(86.1, 182.1) * mm, "end": v(88.93, 182.1) * mm});
            skLineSegment(sketch, "E19.4.8.11", {"start": v(103.07, 182.1) * mm, "end": v(102.59, 182.59) * mm});
            skLineSegment(sketch, "E19.4.8.12", {"start": v(88.93, 201.9) * mm, "end": v(89.41, 201.41) * mm});
            skLineSegment(sketch, "E19.4.8.13", {"start": v(105.9, 199.07) * mm, "end": v(105.41, 198.59) * mm});
            skLineSegment(sketch, "E19.4.8.14", {"start": v(105.41, 185.41) * mm, "end": v(105.9, 184.93) * mm});
            skLineSegment(sketch, "E19.4.8.15", {"start": v(103.07, 201.9) * mm, "end": v(102.59, 201.41) * mm});
            skLineSegment(sketch, "E19.4.8.16", {"start": v(86.1, 199.07) * mm, "end": v(86.59, 198.59) * mm});
            skLineSegment(sketch, "E19.4.8.17", {"start": v(86.59, 185.41) * mm, "end": v(86.1, 184.93) * mm});
            skLineSegment(sketch, "E19.4.8.18", {"start": v(88.93, 182.1) * mm, "end": v(89.41, 182.59) * mm});
            skCircle(sketch, "E19.5.0.0", {"center": v(132, -0.75) * mm, "radius": 2 * mm});
            skArc(sketch, "E19.5.0.1", {"start": v(129.41, -6.59) * mm, "mid": v(126.59, -6.59) * mm, "end": v(126.59, -9.41) * mm});
            skArc(sketch, "E19.5.0.2", {"start": v(110.1, 7.07) * mm, "mid": v(110.1, 9.9) * mm, "end": v(112.93, 9.9) * mm});
            skArc(sketch, "E19.5.0.3", {"start": v(113.41, -9.41) * mm, "mid": v(113.41, -6.59) * mm, "end": v(110.59, -6.59) * mm});
            skCircle(sketch, "E19.5.0.4", {"center": v(120, 12) * mm, "radius": 2 * mm});
            skArc(sketch, "E19.5.0.5", {"start": v(126.59, 9.41) * mm, "mid": v(126.59, 6.59) * mm, "end": v(129.41, 6.59) * mm});
            skArc(sketch, "E19.5.0.6", {"start": v(110.59, 6.59) * mm, "mid": v(113.41, 6.59) * mm, "end": v(113.41, 9.41) * mm});
            skCircle(sketch, "E19.5.0.7", {"center": v(120, 0) * mm, "radius": 7 * mm});
            skArc(sketch, "E19.5.0.8", {"start": v(129.9, 7.07) * mm, "mid": v(129.9, 9.9) * mm, "end": v(127.07, 9.9) * mm});
            skArc(sketch, "E19.5.0.9", {"start": v(127.07, -9.9) * mm, "mid": v(129.9, -9.9) * mm, "end": v(129.9, -7.07) * mm});
            skArc(sketch, "E19.5.0.10", {"start": v(110.1, -7.07) * mm, "mid": v(110.1, -9.9) * mm, "end": v(112.93, -9.9) * mm});
            skLineSegment(sketch, "E19.5.0.11", {"start": v(127.07, -9.9) * mm, "end": v(126.59, -9.41) * mm});
            skLineSegment(sketch, "E19.5.0.12", {"start": v(112.93, 9.9) * mm, "end": v(113.41, 9.41) * mm});
            skLineSegment(sketch, "E19.5.0.13", {"start": v(129.9, 7.07) * mm, "end": v(129.41, 6.59) * mm});
            skLineSegment(sketch, "E19.5.0.14", {"start": v(129.41, -6.59) * mm, "end": v(129.9, -7.07) * mm});
            skLineSegment(sketch, "E19.5.0.15", {"start": v(127.07, 9.9) * mm, "end": v(126.59, 9.41) * mm});
            skLineSegment(sketch, "E19.5.0.16", {"start": v(110.1, 7.07) * mm, "end": v(110.59, 6.59) * mm});
            skLineSegment(sketch, "E19.5.0.17", {"start": v(110.59, -6.59) * mm, "end": v(110.1, -7.07) * mm});
            skLineSegment(sketch, "E19.5.0.18", {"start": v(112.93, -9.9) * mm, "end": v(113.41, -9.41) * mm});
            skCircle(sketch, "E19.5.1.0", {"center": v(132, 23.25) * mm, "radius": 2 * mm});
            skArc(sketch, "E19.5.1.1", {"start": v(129.41, 17.41) * mm, "mid": v(126.59, 17.41) * mm, "end": v(126.59, 14.59) * mm});
            skArc(sketch, "E19.5.1.2", {"start": v(110.1, 31.07) * mm, "mid": v(110.1, 33.9) * mm, "end": v(112.93, 33.9) * mm});
            skArc(sketch, "E19.5.1.3", {"start": v(113.41, 14.59) * mm, "mid": v(113.41, 17.41) * mm, "end": v(110.59, 17.41) * mm});
            skCircle(sketch, "E19.5.1.4", {"center": v(120, 36) * mm, "radius": 2 * mm});
            skArc(sketch, "E19.5.1.5", {"start": v(126.59, 33.41) * mm, "mid": v(126.59, 30.59) * mm, "end": v(129.41, 30.59) * mm});
            skArc(sketch, "E19.5.1.6", {"start": v(110.59, 30.59) * mm, "mid": v(113.41, 30.59) * mm, "end": v(113.41, 33.41) * mm});
            skCircle(sketch, "E19.5.1.7", {"center": v(120, 24) * mm, "radius": 7 * mm});
            skArc(sketch, "E19.5.1.8", {"start": v(129.9, 31.07) * mm, "mid": v(129.9, 33.9) * mm, "end": v(127.07, 33.9) * mm});
            skArc(sketch, "E19.5.1.9", {"start": v(127.07, 14.1) * mm, "mid": v(129.9, 14.1) * mm, "end": v(129.9, 16.93) * mm});
            skArc(sketch, "E19.5.1.10", {"start": v(110.1, 16.93) * mm, "mid": v(110.1, 14.1) * mm, "end": v(112.93, 14.1) * mm});
            skLineSegment(sketch, "E19.5.1.11", {"start": v(127.07, 14.1) * mm, "end": v(126.59, 14.59) * mm});
            skLineSegment(sketch, "E19.5.1.12", {"start": v(112.93, 33.9) * mm, "end": v(113.41, 33.41) * mm});
            skLineSegment(sketch, "E19.5.1.13", {"start": v(129.9, 31.07) * mm, "end": v(129.41, 30.59) * mm});
            skLineSegment(sketch, "E19.5.1.14", {"start": v(129.41, 17.41) * mm, "end": v(129.9, 16.93) * mm});
            skLineSegment(sketch, "E19.5.1.15", {"start": v(127.07, 33.9) * mm, "end": v(126.59, 33.41) * mm});
            skLineSegment(sketch, "E19.5.1.16", {"start": v(110.1, 31.07) * mm, "end": v(110.59, 30.59) * mm});
            skLineSegment(sketch, "E19.5.1.17", {"start": v(110.59, 17.41) * mm, "end": v(110.1, 16.93) * mm});
            skLineSegment(sketch, "E19.5.1.18", {"start": v(112.93, 14.1) * mm, "end": v(113.41, 14.59) * mm});
            skCircle(sketch, "E19.5.2.0", {"center": v(132, 47.25) * mm, "radius": 2 * mm});
            skArc(sketch, "E19.5.2.1", {"start": v(129.41, 41.41) * mm, "mid": v(126.59, 41.41) * mm, "end": v(126.59, 38.59) * mm});
            skArc(sketch, "E19.5.2.2", {"start": v(110.1, 55.07) * mm, "mid": v(110.1, 57.9) * mm, "end": v(112.93, 57.9) * mm});
            skArc(sketch, "E19.5.2.3", {"start": v(113.41, 38.59) * mm, "mid": v(113.41, 41.41) * mm, "end": v(110.59, 41.41) * mm});
            skCircle(sketch, "E19.5.2.4", {"center": v(120, 60) * mm, "radius": 2 * mm});
            skArc(sketch, "E19.5.2.5", {"start": v(126.59, 57.41) * mm, "mid": v(126.59, 54.59) * mm, "end": v(129.41, 54.59) * mm});
            skArc(sketch, "E19.5.2.6", {"start": v(110.59, 54.59) * mm, "mid": v(113.41, 54.59) * mm, "end": v(113.41, 57.41) * mm});
            skCircle(sketch, "E19.5.2.7", {"center": v(120, 48) * mm, "radius": 7 * mm});
            skArc(sketch, "E19.5.2.8", {"start": v(129.9, 55.07) * mm, "mid": v(129.9, 57.9) * mm, "end": v(127.07, 57.9) * mm});
            skArc(sketch, "E19.5.2.9", {"start": v(127.07, 38.1) * mm, "mid": v(129.9, 38.1) * mm, "end": v(129.9, 40.93) * mm});
            skArc(sketch, "E19.5.2.10", {"start": v(110.1, 40.93) * mm, "mid": v(110.1, 38.1) * mm, "end": v(112.93, 38.1) * mm});
            skLineSegment(sketch, "E19.5.2.11", {"start": v(127.07, 38.1) * mm, "end": v(126.59, 38.59) * mm});
            skLineSegment(sketch, "E19.5.2.12", {"start": v(112.93, 57.9) * mm, "end": v(113.41, 57.41) * mm});
            skLineSegment(sketch, "E19.5.2.13", {"start": v(129.9, 55.07) * mm, "end": v(129.41, 54.59) * mm});
            skLineSegment(sketch, "E19.5.2.14", {"start": v(129.41, 41.41) * mm, "end": v(129.9, 40.93) * mm});
            skLineSegment(sketch, "E19.5.2.15", {"start": v(127.07, 57.9) * mm, "end": v(126.59, 57.41) * mm});
            skLineSegment(sketch, "E19.5.2.16", {"start": v(110.1, 55.07) * mm, "end": v(110.59, 54.59) * mm});
            skLineSegment(sketch, "E19.5.2.17", {"start": v(110.59, 41.41) * mm, "end": v(110.1, 40.93) * mm});
            skLineSegment(sketch, "E19.5.2.18", {"start": v(112.93, 38.1) * mm, "end": v(113.41, 38.59) * mm});
            skCircle(sketch, "E19.5.3.0", {"center": v(132, 71.25) * mm, "radius": 2 * mm});
            skArc(sketch, "E19.5.3.1", {"start": v(129.41, 65.41) * mm, "mid": v(126.59, 65.41) * mm, "end": v(126.59, 62.59) * mm});
            skArc(sketch, "E19.5.3.2", {"start": v(110.1, 79.07) * mm, "mid": v(110.1, 81.9) * mm, "end": v(112.93, 81.9) * mm});
            skArc(sketch, "E19.5.3.3", {"start": v(113.41, 62.59) * mm, "mid": v(113.41, 65.41) * mm, "end": v(110.59, 65.41) * mm});
            skCircle(sketch, "E19.5.3.4", {"center": v(120, 84) * mm, "radius": 2 * mm});
            skArc(sketch, "E19.5.3.5", {"start": v(126.59, 81.41) * mm, "mid": v(126.59, 78.59) * mm, "end": v(129.41, 78.59) * mm});
            skArc(sketch, "E19.5.3.6", {"start": v(110.59, 78.59) * mm, "mid": v(113.41, 78.59) * mm, "end": v(113.41, 81.41) * mm});
            skCircle(sketch, "E19.5.3.7", {"center": v(120, 72) * mm, "radius": 7 * mm});
            skArc(sketch, "E19.5.3.8", {"start": v(129.9, 79.07) * mm, "mid": v(129.9, 81.9) * mm, "end": v(127.07, 81.9) * mm});
            skArc(sketch, "E19.5.3.9", {"start": v(127.07, 62.1) * mm, "mid": v(129.9, 62.1) * mm, "end": v(129.9, 64.93) * mm});
            skArc(sketch, "E19.5.3.10", {"start": v(110.1, 64.93) * mm, "mid": v(110.1, 62.1) * mm, "end": v(112.93, 62.1) * mm});
            skLineSegment(sketch, "E19.5.3.11", {"start": v(127.07, 62.1) * mm, "end": v(126.59, 62.59) * mm});
            skLineSegment(sketch, "E19.5.3.12", {"start": v(112.93, 81.9) * mm, "end": v(113.41, 81.41) * mm});
            skLineSegment(sketch, "E19.5.3.13", {"start": v(129.9, 79.07) * mm, "end": v(129.41, 78.59) * mm});
            skLineSegment(sketch, "E19.5.3.14", {"start": v(129.41, 65.41) * mm, "end": v(129.9, 64.93) * mm});
            skLineSegment(sketch, "E19.5.3.15", {"start": v(127.07, 81.9) * mm, "end": v(126.59, 81.41) * mm});
            skLineSegment(sketch, "E19.5.3.16", {"start": v(110.1, 79.07) * mm, "end": v(110.59, 78.59) * mm});
            skLineSegment(sketch, "E19.5.3.17", {"start": v(110.59, 65.41) * mm, "end": v(110.1, 64.93) * mm});
            skLineSegment(sketch, "E19.5.3.18", {"start": v(112.93, 62.1) * mm, "end": v(113.41, 62.59) * mm});
            skCircle(sketch, "E19.5.4.0", {"center": v(132, 95.25) * mm, "radius": 2 * mm});
            skArc(sketch, "E19.5.4.1", {"start": v(129.41, 89.41) * mm, "mid": v(126.59, 89.41) * mm, "end": v(126.59, 86.59) * mm});
            skArc(sketch, "E19.5.4.2", {"start": v(110.1, 103.07) * mm, "mid": v(110.1, 105.9) * mm, "end": v(112.93, 105.9) * mm});
            skArc(sketch, "E19.5.4.3", {"start": v(113.41, 86.59) * mm, "mid": v(113.41, 89.41) * mm, "end": v(110.59, 89.41) * mm});
            skCircle(sketch, "E19.5.4.4", {"center": v(120, 108) * mm, "radius": 2 * mm});
            skArc(sketch, "E19.5.4.5", {"start": v(126.59, 105.41) * mm, "mid": v(126.59, 102.59) * mm, "end": v(129.41, 102.59) * mm});
            skArc(sketch, "E19.5.4.6", {"start": v(110.59, 102.59) * mm, "mid": v(113.41, 102.59) * mm, "end": v(113.41, 105.41) * mm});
            skCircle(sketch, "E19.5.4.7", {"center": v(120, 96) * mm, "radius": 7 * mm});
            skArc(sketch, "E19.5.4.8", {"start": v(129.9, 103.07) * mm, "mid": v(129.9, 105.9) * mm, "end": v(127.07, 105.9) * mm});
            skArc(sketch, "E19.5.4.9", {"start": v(127.07, 86.1) * mm, "mid": v(129.9, 86.1) * mm, "end": v(129.9, 88.93) * mm});
            skArc(sketch, "E19.5.4.10", {"start": v(110.1, 88.93) * mm, "mid": v(110.1, 86.1) * mm, "end": v(112.93, 86.1) * mm});
            skLineSegment(sketch, "E19.5.4.11", {"start": v(127.07, 86.1) * mm, "end": v(126.59, 86.59) * mm});
            skLineSegment(sketch, "E19.5.4.12", {"start": v(112.93, 105.9) * mm, "end": v(113.41, 105.41) * mm});
            skLineSegment(sketch, "E19.5.4.13", {"start": v(129.9, 103.07) * mm, "end": v(129.41, 102.59) * mm});
            skLineSegment(sketch, "E19.5.4.14", {"start": v(129.41, 89.41) * mm, "end": v(129.9, 88.93) * mm});
            skLineSegment(sketch, "E19.5.4.15", {"start": v(127.07, 105.9) * mm, "end": v(126.59, 105.41) * mm});
            skLineSegment(sketch, "E19.5.4.16", {"start": v(110.1, 103.07) * mm, "end": v(110.59, 102.59) * mm});
            skLineSegment(sketch, "E19.5.4.17", {"start": v(110.59, 89.41) * mm, "end": v(110.1, 88.93) * mm});
            skLineSegment(sketch, "E19.5.4.18", {"start": v(112.93, 86.1) * mm, "end": v(113.41, 86.59) * mm});
            skCircle(sketch, "E19.5.5.0", {"center": v(132, 119.25) * mm, "radius": 2 * mm});
            skArc(sketch, "E19.5.5.1", {"start": v(129.41, 113.41) * mm, "mid": v(126.59, 113.41) * mm, "end": v(126.59, 110.59) * mm});
            skArc(sketch, "E19.5.5.2", {"start": v(110.1, 127.07) * mm, "mid": v(110.1, 129.9) * mm, "end": v(112.93, 129.9) * mm});
            skArc(sketch, "E19.5.5.3", {"start": v(113.41, 110.59) * mm, "mid": v(113.41, 113.41) * mm, "end": v(110.59, 113.41) * mm});
            skCircle(sketch, "E19.5.5.4", {"center": v(120, 132) * mm, "radius": 2 * mm});
            skArc(sketch, "E19.5.5.5", {"start": v(126.59, 129.41) * mm, "mid": v(126.59, 126.59) * mm, "end": v(129.41, 126.59) * mm});
            skArc(sketch, "E19.5.5.6", {"start": v(110.59, 126.59) * mm, "mid": v(113.41, 126.59) * mm, "end": v(113.41, 129.41) * mm});
            skCircle(sketch, "E19.5.5.7", {"center": v(120, 120) * mm, "radius": 7 * mm});
            skArc(sketch, "E19.5.5.8", {"start": v(129.9, 127.07) * mm, "mid": v(129.9, 129.9) * mm, "end": v(127.07, 129.9) * mm});
            skArc(sketch, "E19.5.5.9", {"start": v(127.07, 110.1) * mm, "mid": v(129.9, 110.1) * mm, "end": v(129.9, 112.93) * mm});
            skArc(sketch, "E19.5.5.10", {"start": v(110.1, 112.93) * mm, "mid": v(110.1, 110.1) * mm, "end": v(112.93, 110.1) * mm});
            skLineSegment(sketch, "E19.5.5.11", {"start": v(127.07, 110.1) * mm, "end": v(126.59, 110.59) * mm});
            skLineSegment(sketch, "E19.5.5.12", {"start": v(112.93, 129.9) * mm, "end": v(113.41, 129.41) * mm});
            skLineSegment(sketch, "E19.5.5.13", {"start": v(129.9, 127.07) * mm, "end": v(129.41, 126.59) * mm});
            skLineSegment(sketch, "E19.5.5.14", {"start": v(129.41, 113.41) * mm, "end": v(129.9, 112.93) * mm});
            skLineSegment(sketch, "E19.5.5.15", {"start": v(127.07, 129.9) * mm, "end": v(126.59, 129.41) * mm});
            skLineSegment(sketch, "E19.5.5.16", {"start": v(110.1, 127.07) * mm, "end": v(110.59, 126.59) * mm});
            skLineSegment(sketch, "E19.5.5.17", {"start": v(110.59, 113.41) * mm, "end": v(110.1, 112.93) * mm});
            skLineSegment(sketch, "E19.5.5.18", {"start": v(112.93, 110.1) * mm, "end": v(113.41, 110.59) * mm});
            skCircle(sketch, "E19.5.6.0", {"center": v(132, 143.25) * mm, "radius": 2 * mm});
            skArc(sketch, "E19.5.6.1", {"start": v(129.41, 137.41) * mm, "mid": v(126.59, 137.41) * mm, "end": v(126.59, 134.59) * mm});
            skArc(sketch, "E19.5.6.2", {"start": v(110.1, 151.07) * mm, "mid": v(110.1, 153.9) * mm, "end": v(112.93, 153.9) * mm});
            skArc(sketch, "E19.5.6.3", {"start": v(113.41, 134.59) * mm, "mid": v(113.41, 137.41) * mm, "end": v(110.59, 137.41) * mm});
            skCircle(sketch, "E19.5.6.4", {"center": v(120, 156) * mm, "radius": 2 * mm});
            skArc(sketch, "E19.5.6.5", {"start": v(126.59, 153.41) * mm, "mid": v(126.59, 150.59) * mm, "end": v(129.41, 150.59) * mm});
            skArc(sketch, "E19.5.6.6", {"start": v(110.59, 150.59) * mm, "mid": v(113.41, 150.59) * mm, "end": v(113.41, 153.41) * mm});
            skCircle(sketch, "E19.5.6.7", {"center": v(120, 144) * mm, "radius": 7 * mm});
            skArc(sketch, "E19.5.6.8", {"start": v(129.9, 151.07) * mm, "mid": v(129.9, 153.9) * mm, "end": v(127.07, 153.9) * mm});
            skArc(sketch, "E19.5.6.9", {"start": v(127.07, 134.1) * mm, "mid": v(129.9, 134.1) * mm, "end": v(129.9, 136.93) * mm});
            skArc(sketch, "E19.5.6.10", {"start": v(110.1, 136.93) * mm, "mid": v(110.1, 134.1) * mm, "end": v(112.93, 134.1) * mm});
            skLineSegment(sketch, "E19.5.6.11", {"start": v(127.07, 134.1) * mm, "end": v(126.59, 134.59) * mm});
            skLineSegment(sketch, "E19.5.6.12", {"start": v(112.93, 153.9) * mm, "end": v(113.41, 153.41) * mm});
            skLineSegment(sketch, "E19.5.6.13", {"start": v(129.9, 151.07) * mm, "end": v(129.41, 150.59) * mm});
            skLineSegment(sketch, "E19.5.6.14", {"start": v(129.41, 137.41) * mm, "end": v(129.9, 136.93) * mm});
            skLineSegment(sketch, "E19.5.6.15", {"start": v(127.07, 153.9) * mm, "end": v(126.59, 153.41) * mm});
            skLineSegment(sketch, "E19.5.6.16", {"start": v(110.1, 151.07) * mm, "end": v(110.59, 150.59) * mm});
            skLineSegment(sketch, "E19.5.6.17", {"start": v(110.59, 137.41) * mm, "end": v(110.1, 136.93) * mm});
            skLineSegment(sketch, "E19.5.6.18", {"start": v(112.93, 134.1) * mm, "end": v(113.41, 134.59) * mm});
            skCircle(sketch, "E19.5.7.0", {"center": v(132, 167.25) * mm, "radius": 2 * mm});
            skArc(sketch, "E19.5.7.1", {"start": v(129.41, 161.41) * mm, "mid": v(126.59, 161.41) * mm, "end": v(126.59, 158.59) * mm});
            skArc(sketch, "E19.5.7.2", {"start": v(110.1, 175.07) * mm, "mid": v(110.1, 177.9) * mm, "end": v(112.93, 177.9) * mm});
            skArc(sketch, "E19.5.7.3", {"start": v(113.41, 158.59) * mm, "mid": v(113.41, 161.41) * mm, "end": v(110.59, 161.41) * mm});
            skCircle(sketch, "E19.5.7.4", {"center": v(120, 180) * mm, "radius": 2 * mm});
            skArc(sketch, "E19.5.7.5", {"start": v(126.59, 177.41) * mm, "mid": v(126.59, 174.59) * mm, "end": v(129.41, 174.59) * mm});
            skArc(sketch, "E19.5.7.6", {"start": v(110.59, 174.59) * mm, "mid": v(113.41, 174.59) * mm, "end": v(113.41, 177.41) * mm});
            skCircle(sketch, "E19.5.7.7", {"center": v(120, 168) * mm, "radius": 7 * mm});
            skArc(sketch, "E19.5.7.8", {"start": v(129.9, 175.07) * mm, "mid": v(129.9, 177.9) * mm, "end": v(127.07, 177.9) * mm});
            skArc(sketch, "E19.5.7.9", {"start": v(127.07, 158.1) * mm, "mid": v(129.9, 158.1) * mm, "end": v(129.9, 160.93) * mm});
            skArc(sketch, "E19.5.7.10", {"start": v(110.1, 160.93) * mm, "mid": v(110.1, 158.1) * mm, "end": v(112.93, 158.1) * mm});
            skLineSegment(sketch, "E19.5.7.11", {"start": v(127.07, 158.1) * mm, "end": v(126.59, 158.59) * mm});
            skLineSegment(sketch, "E19.5.7.12", {"start": v(112.93, 177.9) * mm, "end": v(113.41, 177.41) * mm});
            skLineSegment(sketch, "E19.5.7.13", {"start": v(129.9, 175.07) * mm, "end": v(129.41, 174.59) * mm});
            skLineSegment(sketch, "E19.5.7.14", {"start": v(129.41, 161.41) * mm, "end": v(129.9, 160.93) * mm});
            skLineSegment(sketch, "E19.5.7.15", {"start": v(127.07, 177.9) * mm, "end": v(126.59, 177.41) * mm});
            skLineSegment(sketch, "E19.5.7.16", {"start": v(110.1, 175.07) * mm, "end": v(110.59, 174.59) * mm});
            skLineSegment(sketch, "E19.5.7.17", {"start": v(110.59, 161.41) * mm, "end": v(110.1, 160.93) * mm});
            skLineSegment(sketch, "E19.5.7.18", {"start": v(112.93, 158.1) * mm, "end": v(113.41, 158.59) * mm});
            skCircle(sketch, "E19.5.8.0", {"center": v(132, 191.25) * mm, "radius": 2 * mm});
            skArc(sketch, "E19.5.8.1", {"start": v(129.41, 185.41) * mm, "mid": v(126.59, 185.41) * mm, "end": v(126.59, 182.59) * mm});
            skArc(sketch, "E19.5.8.2", {"start": v(110.1, 199.07) * mm, "mid": v(110.1, 201.9) * mm, "end": v(112.93, 201.9) * mm});
            skArc(sketch, "E19.5.8.3", {"start": v(113.41, 182.59) * mm, "mid": v(113.41, 185.41) * mm, "end": v(110.59, 185.41) * mm});
            skCircle(sketch, "E19.5.8.4", {"center": v(120, 204) * mm, "radius": 2 * mm});
            skArc(sketch, "E19.5.8.5", {"start": v(126.59, 201.41) * mm, "mid": v(126.59, 198.59) * mm, "end": v(129.41, 198.59) * mm});
            skArc(sketch, "E19.5.8.6", {"start": v(110.59, 198.59) * mm, "mid": v(113.41, 198.59) * mm, "end": v(113.41, 201.41) * mm});
            skCircle(sketch, "E19.5.8.7", {"center": v(120, 192) * mm, "radius": 7 * mm});
            skArc(sketch, "E19.5.8.8", {"start": v(129.9, 199.07) * mm, "mid": v(129.9, 201.9) * mm, "end": v(127.07, 201.9) * mm});
            skArc(sketch, "E19.5.8.9", {"start": v(127.07, 182.1) * mm, "mid": v(129.9, 182.1) * mm, "end": v(129.9, 184.93) * mm});
            skArc(sketch, "E19.5.8.10", {"start": v(110.1, 184.93) * mm, "mid": v(110.1, 182.1) * mm, "end": v(112.93, 182.1) * mm});
            skLineSegment(sketch, "E19.5.8.11", {"start": v(127.07, 182.1) * mm, "end": v(126.59, 182.59) * mm});
            skLineSegment(sketch, "E19.5.8.12", {"start": v(112.93, 201.9) * mm, "end": v(113.41, 201.41) * mm});
            skLineSegment(sketch, "E19.5.8.13", {"start": v(129.9, 199.07) * mm, "end": v(129.41, 198.59) * mm});
            skLineSegment(sketch, "E19.5.8.14", {"start": v(129.41, 185.41) * mm, "end": v(129.9, 184.93) * mm});
            skLineSegment(sketch, "E19.5.8.15", {"start": v(127.07, 201.9) * mm, "end": v(126.59, 201.41) * mm});
            skLineSegment(sketch, "E19.5.8.16", {"start": v(110.1, 199.07) * mm, "end": v(110.59, 198.59) * mm});
            skLineSegment(sketch, "E19.5.8.17", {"start": v(110.59, 185.41) * mm, "end": v(110.1, 184.93) * mm});
            skLineSegment(sketch, "E19.5.8.18", {"start": v(112.93, 182.1) * mm, "end": v(113.41, 182.59) * mm});
            skCircle(sketch, "E19.6.0.0", {"center": v(156, -0.75) * mm, "radius": 2 * mm});
            skArc(sketch, "E19.6.0.1", {"start": v(153.41, -6.59) * mm, "mid": v(150.59, -6.59) * mm, "end": v(150.59, -9.41) * mm});
            skArc(sketch, "E19.6.0.2", {"start": v(134.1, 7.07) * mm, "mid": v(134.1, 9.9) * mm, "end": v(136.93, 9.9) * mm});
            skArc(sketch, "E19.6.0.3", {"start": v(137.41, -9.41) * mm, "mid": v(137.41, -6.59) * mm, "end": v(134.59, -6.59) * mm});
            skCircle(sketch, "E19.6.0.4", {"center": v(144, 12) * mm, "radius": 2 * mm});
            skArc(sketch, "E19.6.0.5", {"start": v(150.59, 9.41) * mm, "mid": v(150.59, 6.59) * mm, "end": v(153.41, 6.59) * mm});
            skArc(sketch, "E19.6.0.6", {"start": v(134.59, 6.59) * mm, "mid": v(137.41, 6.59) * mm, "end": v(137.41, 9.41) * mm});
            skCircle(sketch, "E19.6.0.7", {"center": v(144, 0) * mm, "radius": 7 * mm});
            skArc(sketch, "E19.6.0.8", {"start": v(153.9, 7.07) * mm, "mid": v(153.9, 9.9) * mm, "end": v(151.07, 9.9) * mm});
            skArc(sketch, "E19.6.0.9", {"start": v(151.07, -9.9) * mm, "mid": v(153.9, -9.9) * mm, "end": v(153.9, -7.07) * mm});
            skArc(sketch, "E19.6.0.10", {"start": v(134.1, -7.07) * mm, "mid": v(134.1, -9.9) * mm, "end": v(136.93, -9.9) * mm});
            skLineSegment(sketch, "E19.6.0.11", {"start": v(151.07, -9.9) * mm, "end": v(150.59, -9.41) * mm});
            skLineSegment(sketch, "E19.6.0.12", {"start": v(136.93, 9.9) * mm, "end": v(137.41, 9.41) * mm});
            skLineSegment(sketch, "E19.6.0.13", {"start": v(153.9, 7.07) * mm, "end": v(153.41, 6.59) * mm});
            skLineSegment(sketch, "E19.6.0.14", {"start": v(153.41, -6.59) * mm, "end": v(153.9, -7.07) * mm});
            skLineSegment(sketch, "E19.6.0.15", {"start": v(151.07, 9.9) * mm, "end": v(150.59, 9.41) * mm});
            skLineSegment(sketch, "E19.6.0.16", {"start": v(134.1, 7.07) * mm, "end": v(134.59, 6.59) * mm});
            skLineSegment(sketch, "E19.6.0.17", {"start": v(134.59, -6.59) * mm, "end": v(134.1, -7.07) * mm});
            skLineSegment(sketch, "E19.6.0.18", {"start": v(136.93, -9.9) * mm, "end": v(137.41, -9.41) * mm});
            skCircle(sketch, "E19.6.1.0", {"center": v(156, 23.25) * mm, "radius": 2 * mm});
            skArc(sketch, "E19.6.1.1", {"start": v(153.41, 17.41) * mm, "mid": v(150.59, 17.41) * mm, "end": v(150.59, 14.59) * mm});
            skArc(sketch, "E19.6.1.2", {"start": v(134.1, 31.07) * mm, "mid": v(134.1, 33.9) * mm, "end": v(136.93, 33.9) * mm});
            skArc(sketch, "E19.6.1.3", {"start": v(137.41, 14.59) * mm, "mid": v(137.41, 17.41) * mm, "end": v(134.59, 17.41) * mm});
            skCircle(sketch, "E19.6.1.4", {"center": v(144, 36) * mm, "radius": 2 * mm});
            skArc(sketch, "E19.6.1.5", {"start": v(150.59, 33.41) * mm, "mid": v(150.59, 30.59) * mm, "end": v(153.41, 30.59) * mm});
            skArc(sketch, "E19.6.1.6", {"start": v(134.59, 30.59) * mm, "mid": v(137.41, 30.59) * mm, "end": v(137.41, 33.41) * mm});
            skCircle(sketch, "E19.6.1.7", {"center": v(144, 24) * mm, "radius": 7 * mm});
            skArc(sketch, "E19.6.1.8", {"start": v(153.9, 31.07) * mm, "mid": v(153.9, 33.9) * mm, "end": v(151.07, 33.9) * mm});
            skArc(sketch, "E19.6.1.9", {"start": v(151.07, 14.1) * mm, "mid": v(153.9, 14.1) * mm, "end": v(153.9, 16.93) * mm});
            skArc(sketch, "E19.6.1.10", {"start": v(134.1, 16.93) * mm, "mid": v(134.1, 14.1) * mm, "end": v(136.93, 14.1) * mm});
            skLineSegment(sketch, "E19.6.1.11", {"start": v(151.07, 14.1) * mm, "end": v(150.59, 14.59) * mm});
            skLineSegment(sketch, "E19.6.1.12", {"start": v(136.93, 33.9) * mm, "end": v(137.41, 33.41) * mm});
            skLineSegment(sketch, "E19.6.1.13", {"start": v(153.9, 31.07) * mm, "end": v(153.41, 30.59) * mm});
            skLineSegment(sketch, "E19.6.1.14", {"start": v(153.41, 17.41) * mm, "end": v(153.9, 16.93) * mm});
            skLineSegment(sketch, "E19.6.1.15", {"start": v(151.07, 33.9) * mm, "end": v(150.59, 33.41) * mm});
            skLineSegment(sketch, "E19.6.1.16", {"start": v(134.1, 31.07) * mm, "end": v(134.59, 30.59) * mm});
            skLineSegment(sketch, "E19.6.1.17", {"start": v(134.59, 17.41) * mm, "end": v(134.1, 16.93) * mm});
            skLineSegment(sketch, "E19.6.1.18", {"start": v(136.93, 14.1) * mm, "end": v(137.41, 14.59) * mm});
            skCircle(sketch, "E19.6.2.0", {"center": v(156, 47.25) * mm, "radius": 2 * mm});
            skArc(sketch, "E19.6.2.1", {"start": v(153.41, 41.41) * mm, "mid": v(150.59, 41.41) * mm, "end": v(150.59, 38.59) * mm});
            skArc(sketch, "E19.6.2.2", {"start": v(134.1, 55.07) * mm, "mid": v(134.1, 57.9) * mm, "end": v(136.93, 57.9) * mm});
            skArc(sketch, "E19.6.2.3", {"start": v(137.41, 38.59) * mm, "mid": v(137.41, 41.41) * mm, "end": v(134.59, 41.41) * mm});
            skCircle(sketch, "E19.6.2.4", {"center": v(144, 60) * mm, "radius": 2 * mm});
            skArc(sketch, "E19.6.2.5", {"start": v(150.59, 57.41) * mm, "mid": v(150.59, 54.59) * mm, "end": v(153.41, 54.59) * mm});
            skArc(sketch, "E19.6.2.6", {"start": v(134.59, 54.59) * mm, "mid": v(137.41, 54.59) * mm, "end": v(137.41, 57.41) * mm});
            skCircle(sketch, "E19.6.2.7", {"center": v(144, 48) * mm, "radius": 7 * mm});
            skArc(sketch, "E19.6.2.8", {"start": v(153.9, 55.07) * mm, "mid": v(153.9, 57.9) * mm, "end": v(151.07, 57.9) * mm});
            skArc(sketch, "E19.6.2.9", {"start": v(151.07, 38.1) * mm, "mid": v(153.9, 38.1) * mm, "end": v(153.9, 40.93) * mm});
            skArc(sketch, "E19.6.2.10", {"start": v(134.1, 40.93) * mm, "mid": v(134.1, 38.1) * mm, "end": v(136.93, 38.1) * mm});
            skLineSegment(sketch, "E19.6.2.11", {"start": v(151.07, 38.1) * mm, "end": v(150.59, 38.59) * mm});
            skLineSegment(sketch, "E19.6.2.12", {"start": v(136.93, 57.9) * mm, "end": v(137.41, 57.41) * mm});
            skLineSegment(sketch, "E19.6.2.13", {"start": v(153.9, 55.07) * mm, "end": v(153.41, 54.59) * mm});
            skLineSegment(sketch, "E19.6.2.14", {"start": v(153.41, 41.41) * mm, "end": v(153.9, 40.93) * mm});
            skLineSegment(sketch, "E19.6.2.15", {"start": v(151.07, 57.9) * mm, "end": v(150.59, 57.41) * mm});
            skLineSegment(sketch, "E19.6.2.16", {"start": v(134.1, 55.07) * mm, "end": v(134.59, 54.59) * mm});
            skLineSegment(sketch, "E19.6.2.17", {"start": v(134.59, 41.41) * mm, "end": v(134.1, 40.93) * mm});
            skLineSegment(sketch, "E19.6.2.18", {"start": v(136.93, 38.1) * mm, "end": v(137.41, 38.59) * mm});
            skCircle(sketch, "E19.6.3.0", {"center": v(156, 71.25) * mm, "radius": 2 * mm});
            skArc(sketch, "E19.6.3.1", {"start": v(153.41, 65.41) * mm, "mid": v(150.59, 65.41) * mm, "end": v(150.59, 62.59) * mm});
            skArc(sketch, "E19.6.3.2", {"start": v(134.1, 79.07) * mm, "mid": v(134.1, 81.9) * mm, "end": v(136.93, 81.9) * mm});
            skArc(sketch, "E19.6.3.3", {"start": v(137.41, 62.59) * mm, "mid": v(137.41, 65.41) * mm, "end": v(134.59, 65.41) * mm});
            skCircle(sketch, "E19.6.3.4", {"center": v(144, 84) * mm, "radius": 2 * mm});
            skArc(sketch, "E19.6.3.5", {"start": v(150.59, 81.41) * mm, "mid": v(150.59, 78.59) * mm, "end": v(153.41, 78.59) * mm});
            skArc(sketch, "E19.6.3.6", {"start": v(134.59, 78.59) * mm, "mid": v(137.41, 78.59) * mm, "end": v(137.41, 81.41) * mm});
            skCircle(sketch, "E19.6.3.7", {"center": v(144, 72) * mm, "radius": 7 * mm});
            skArc(sketch, "E19.6.3.8", {"start": v(153.9, 79.07) * mm, "mid": v(153.9, 81.9) * mm, "end": v(151.07, 81.9) * mm});
            skArc(sketch, "E19.6.3.9", {"start": v(151.07, 62.1) * mm, "mid": v(153.9, 62.1) * mm, "end": v(153.9, 64.93) * mm});
            skArc(sketch, "E19.6.3.10", {"start": v(134.1, 64.93) * mm, "mid": v(134.1, 62.1) * mm, "end": v(136.93, 62.1) * mm});
            skLineSegment(sketch, "E19.6.3.11", {"start": v(151.07, 62.1) * mm, "end": v(150.59, 62.59) * mm});
            skLineSegment(sketch, "E19.6.3.12", {"start": v(136.93, 81.9) * mm, "end": v(137.41, 81.41) * mm});
            skLineSegment(sketch, "E19.6.3.13", {"start": v(153.9, 79.07) * mm, "end": v(153.41, 78.59) * mm});
            skLineSegment(sketch, "E19.6.3.14", {"start": v(153.41, 65.41) * mm, "end": v(153.9, 64.93) * mm});
            skLineSegment(sketch, "E19.6.3.15", {"start": v(151.07, 81.9) * mm, "end": v(150.59, 81.41) * mm});
            skLineSegment(sketch, "E19.6.3.16", {"start": v(134.1, 79.07) * mm, "end": v(134.59, 78.59) * mm});
            skLineSegment(sketch, "E19.6.3.17", {"start": v(134.59, 65.41) * mm, "end": v(134.1, 64.93) * mm});
            skLineSegment(sketch, "E19.6.3.18", {"start": v(136.93, 62.1) * mm, "end": v(137.41, 62.59) * mm});
            skCircle(sketch, "E19.6.4.0", {"center": v(156, 95.25) * mm, "radius": 2 * mm});
            skArc(sketch, "E19.6.4.1", {"start": v(153.41, 89.41) * mm, "mid": v(150.59, 89.41) * mm, "end": v(150.59, 86.59) * mm});
            skArc(sketch, "E19.6.4.2", {"start": v(134.1, 103.07) * mm, "mid": v(134.1, 105.9) * mm, "end": v(136.93, 105.9) * mm});
            skArc(sketch, "E19.6.4.3", {"start": v(137.41, 86.59) * mm, "mid": v(137.41, 89.41) * mm, "end": v(134.59, 89.41) * mm});
            skCircle(sketch, "E19.6.4.4", {"center": v(144, 108) * mm, "radius": 2 * mm});
            skArc(sketch, "E19.6.4.5", {"start": v(150.59, 105.41) * mm, "mid": v(150.59, 102.59) * mm, "end": v(153.41, 102.59) * mm});
            skArc(sketch, "E19.6.4.6", {"start": v(134.59, 102.59) * mm, "mid": v(137.41, 102.59) * mm, "end": v(137.41, 105.41) * mm});
            skCircle(sketch, "E19.6.4.7", {"center": v(144, 96) * mm, "radius": 7 * mm});
            skArc(sketch, "E19.6.4.8", {"start": v(153.9, 103.07) * mm, "mid": v(153.9, 105.9) * mm, "end": v(151.07, 105.9) * mm});
            skArc(sketch, "E19.6.4.9", {"start": v(151.07, 86.1) * mm, "mid": v(153.9, 86.1) * mm, "end": v(153.9, 88.93) * mm});
            skArc(sketch, "E19.6.4.10", {"start": v(134.1, 88.93) * mm, "mid": v(134.1, 86.1) * mm, "end": v(136.93, 86.1) * mm});
            skLineSegment(sketch, "E19.6.4.11", {"start": v(151.07, 86.1) * mm, "end": v(150.59, 86.59) * mm});
            skLineSegment(sketch, "E19.6.4.12", {"start": v(136.93, 105.9) * mm, "end": v(137.41, 105.41) * mm});
            skLineSegment(sketch, "E19.6.4.13", {"start": v(153.9, 103.07) * mm, "end": v(153.41, 102.59) * mm});
            skLineSegment(sketch, "E19.6.4.14", {"start": v(153.41, 89.41) * mm, "end": v(153.9, 88.93) * mm});
            skLineSegment(sketch, "E19.6.4.15", {"start": v(151.07, 105.9) * mm, "end": v(150.59, 105.41) * mm});
            skLineSegment(sketch, "E19.6.4.16", {"start": v(134.1, 103.07) * mm, "end": v(134.59, 102.59) * mm});
            skLineSegment(sketch, "E19.6.4.17", {"start": v(134.59, 89.41) * mm, "end": v(134.1, 88.93) * mm});
            skLineSegment(sketch, "E19.6.4.18", {"start": v(136.93, 86.1) * mm, "end": v(137.41, 86.59) * mm});
            skCircle(sketch, "E19.6.5.0", {"center": v(156, 119.25) * mm, "radius": 2 * mm});
            skArc(sketch, "E19.6.5.1", {"start": v(153.41, 113.41) * mm, "mid": v(150.59, 113.41) * mm, "end": v(150.59, 110.59) * mm});
            skArc(sketch, "E19.6.5.2", {"start": v(134.1, 127.07) * mm, "mid": v(134.1, 129.9) * mm, "end": v(136.93, 129.9) * mm});
            skArc(sketch, "E19.6.5.3", {"start": v(137.41, 110.59) * mm, "mid": v(137.41, 113.41) * mm, "end": v(134.59, 113.41) * mm});
            skCircle(sketch, "E19.6.5.4", {"center": v(144, 132) * mm, "radius": 2 * mm});
            skArc(sketch, "E19.6.5.5", {"start": v(150.59, 129.41) * mm, "mid": v(150.59, 126.59) * mm, "end": v(153.41, 126.59) * mm});
            skArc(sketch, "E19.6.5.6", {"start": v(134.59, 126.59) * mm, "mid": v(137.41, 126.59) * mm, "end": v(137.41, 129.41) * mm});
            skCircle(sketch, "E19.6.5.7", {"center": v(144, 120) * mm, "radius": 7 * mm});
            skArc(sketch, "E19.6.5.8", {"start": v(153.9, 127.07) * mm, "mid": v(153.9, 129.9) * mm, "end": v(151.07, 129.9) * mm});
            skArc(sketch, "E19.6.5.9", {"start": v(151.07, 110.1) * mm, "mid": v(153.9, 110.1) * mm, "end": v(153.9, 112.93) * mm});
            skArc(sketch, "E19.6.5.10", {"start": v(134.1, 112.93) * mm, "mid": v(134.1, 110.1) * mm, "end": v(136.93, 110.1) * mm});
            skLineSegment(sketch, "E19.6.5.11", {"start": v(151.07, 110.1) * mm, "end": v(150.59, 110.59) * mm});
            skLineSegment(sketch, "E19.6.5.12", {"start": v(136.93, 129.9) * mm, "end": v(137.41, 129.41) * mm});
            skLineSegment(sketch, "E19.6.5.13", {"start": v(153.9, 127.07) * mm, "end": v(153.41, 126.59) * mm});
            skLineSegment(sketch, "E19.6.5.14", {"start": v(153.41, 113.41) * mm, "end": v(153.9, 112.93) * mm});
            skLineSegment(sketch, "E19.6.5.15", {"start": v(151.07, 129.9) * mm, "end": v(150.59, 129.41) * mm});
            skLineSegment(sketch, "E19.6.5.16", {"start": v(134.1, 127.07) * mm, "end": v(134.59, 126.59) * mm});
            skLineSegment(sketch, "E19.6.5.17", {"start": v(134.59, 113.41) * mm, "end": v(134.1, 112.93) * mm});
            skLineSegment(sketch, "E19.6.5.18", {"start": v(136.93, 110.1) * mm, "end": v(137.41, 110.59) * mm});
            skCircle(sketch, "E19.6.6.0", {"center": v(156, 143.25) * mm, "radius": 2 * mm});
            skArc(sketch, "E19.6.6.1", {"start": v(153.41, 137.41) * mm, "mid": v(150.59, 137.41) * mm, "end": v(150.59, 134.59) * mm});
            skArc(sketch, "E19.6.6.2", {"start": v(134.1, 151.07) * mm, "mid": v(134.1, 153.9) * mm, "end": v(136.93, 153.9) * mm});
            skArc(sketch, "E19.6.6.3", {"start": v(137.41, 134.59) * mm, "mid": v(137.41, 137.41) * mm, "end": v(134.59, 137.41) * mm});
            skCircle(sketch, "E19.6.6.4", {"center": v(144, 156) * mm, "radius": 2 * mm});
            skArc(sketch, "E19.6.6.5", {"start": v(150.59, 153.41) * mm, "mid": v(150.59, 150.59) * mm, "end": v(153.41, 150.59) * mm});
            skArc(sketch, "E19.6.6.6", {"start": v(134.59, 150.59) * mm, "mid": v(137.41, 150.59) * mm, "end": v(137.41, 153.41) * mm});
            skCircle(sketch, "E19.6.6.7", {"center": v(144, 144) * mm, "radius": 7 * mm});
            skArc(sketch, "E19.6.6.8", {"start": v(153.9, 151.07) * mm, "mid": v(153.9, 153.9) * mm, "end": v(151.07, 153.9) * mm});
            skArc(sketch, "E19.6.6.9", {"start": v(151.07, 134.1) * mm, "mid": v(153.9, 134.1) * mm, "end": v(153.9, 136.93) * mm});
            skArc(sketch, "E19.6.6.10", {"start": v(134.1, 136.93) * mm, "mid": v(134.1, 134.1) * mm, "end": v(136.93, 134.1) * mm});
            skLineSegment(sketch, "E19.6.6.11", {"start": v(151.07, 134.1) * mm, "end": v(150.59, 134.59) * mm});
            skLineSegment(sketch, "E19.6.6.12", {"start": v(136.93, 153.9) * mm, "end": v(137.41, 153.41) * mm});
            skLineSegment(sketch, "E19.6.6.13", {"start": v(153.9, 151.07) * mm, "end": v(153.41, 150.59) * mm});
            skLineSegment(sketch, "E19.6.6.14", {"start": v(153.41, 137.41) * mm, "end": v(153.9, 136.93) * mm});
            skLineSegment(sketch, "E19.6.6.15", {"start": v(151.07, 153.9) * mm, "end": v(150.59, 153.41) * mm});
            skLineSegment(sketch, "E19.6.6.16", {"start": v(134.1, 151.07) * mm, "end": v(134.59, 150.59) * mm});
            skLineSegment(sketch, "E19.6.6.17", {"start": v(134.59, 137.41) * mm, "end": v(134.1, 136.93) * mm});
            skLineSegment(sketch, "E19.6.6.18", {"start": v(136.93, 134.1) * mm, "end": v(137.41, 134.59) * mm});
            skCircle(sketch, "E19.6.7.0", {"center": v(156, 167.25) * mm, "radius": 2 * mm});
            skArc(sketch, "E19.6.7.1", {"start": v(153.41, 161.41) * mm, "mid": v(150.59, 161.41) * mm, "end": v(150.59, 158.59) * mm});
            skArc(sketch, "E19.6.7.2", {"start": v(134.1, 175.07) * mm, "mid": v(134.1, 177.9) * mm, "end": v(136.93, 177.9) * mm});
            skArc(sketch, "E19.6.7.3", {"start": v(137.41, 158.59) * mm, "mid": v(137.41, 161.41) * mm, "end": v(134.59, 161.41) * mm});
            skCircle(sketch, "E19.6.7.4", {"center": v(144, 180) * mm, "radius": 2 * mm});
            skArc(sketch, "E19.6.7.5", {"start": v(150.59, 177.41) * mm, "mid": v(150.59, 174.59) * mm, "end": v(153.41, 174.59) * mm});
            skArc(sketch, "E19.6.7.6", {"start": v(134.59, 174.59) * mm, "mid": v(137.41, 174.59) * mm, "end": v(137.41, 177.41) * mm});
            skCircle(sketch, "E19.6.7.7", {"center": v(144, 168) * mm, "radius": 7 * mm});
            skArc(sketch, "E19.6.7.8", {"start": v(153.9, 175.07) * mm, "mid": v(153.9, 177.9) * mm, "end": v(151.07, 177.9) * mm});
            skArc(sketch, "E19.6.7.9", {"start": v(151.07, 158.1) * mm, "mid": v(153.9, 158.1) * mm, "end": v(153.9, 160.93) * mm});
            skArc(sketch, "E19.6.7.10", {"start": v(134.1, 160.93) * mm, "mid": v(134.1, 158.1) * mm, "end": v(136.93, 158.1) * mm});
            skLineSegment(sketch, "E19.6.7.11", {"start": v(151.07, 158.1) * mm, "end": v(150.59, 158.59) * mm});
            skLineSegment(sketch, "E19.6.7.12", {"start": v(136.93, 177.9) * mm, "end": v(137.41, 177.41) * mm});
            skLineSegment(sketch, "E19.6.7.13", {"start": v(153.9, 175.07) * mm, "end": v(153.41, 174.59) * mm});
            skLineSegment(sketch, "E19.6.7.14", {"start": v(153.41, 161.41) * mm, "end": v(153.9, 160.93) * mm});
            skLineSegment(sketch, "E19.6.7.15", {"start": v(151.07, 177.9) * mm, "end": v(150.59, 177.41) * mm});
            skLineSegment(sketch, "E19.6.7.16", {"start": v(134.1, 175.07) * mm, "end": v(134.59, 174.59) * mm});
            skLineSegment(sketch, "E19.6.7.17", {"start": v(134.59, 161.41) * mm, "end": v(134.1, 160.93) * mm});
            skLineSegment(sketch, "E19.6.7.18", {"start": v(136.93, 158.1) * mm, "end": v(137.41, 158.59) * mm});
            skCircle(sketch, "E19.6.8.0", {"center": v(156, 191.25) * mm, "radius": 2 * mm});
            skArc(sketch, "E19.6.8.1", {"start": v(153.41, 185.41) * mm, "mid": v(150.59, 185.41) * mm, "end": v(150.59, 182.59) * mm});
            skArc(sketch, "E19.6.8.2", {"start": v(134.1, 199.07) * mm, "mid": v(134.1, 201.9) * mm, "end": v(136.93, 201.9) * mm});
            skArc(sketch, "E19.6.8.3", {"start": v(137.41, 182.59) * mm, "mid": v(137.41, 185.41) * mm, "end": v(134.59, 185.41) * mm});
            skCircle(sketch, "E19.6.8.4", {"center": v(144, 204) * mm, "radius": 2 * mm});
            skArc(sketch, "E19.6.8.5", {"start": v(150.59, 201.41) * mm, "mid": v(150.59, 198.59) * mm, "end": v(153.41, 198.59) * mm});
            skArc(sketch, "E19.6.8.6", {"start": v(134.59, 198.59) * mm, "mid": v(137.41, 198.59) * mm, "end": v(137.41, 201.41) * mm});
            skCircle(sketch, "E19.6.8.7", {"center": v(144, 192) * mm, "radius": 7 * mm});
            skArc(sketch, "E19.6.8.8", {"start": v(153.9, 199.07) * mm, "mid": v(153.9, 201.9) * mm, "end": v(151.07, 201.9) * mm});
            skArc(sketch, "E19.6.8.9", {"start": v(151.07, 182.1) * mm, "mid": v(153.9, 182.1) * mm, "end": v(153.9, 184.93) * mm});
            skArc(sketch, "E19.6.8.10", {"start": v(134.1, 184.93) * mm, "mid": v(134.1, 182.1) * mm, "end": v(136.93, 182.1) * mm});
            skLineSegment(sketch, "E19.6.8.11", {"start": v(151.07, 182.1) * mm, "end": v(150.59, 182.59) * mm});
            skLineSegment(sketch, "E19.6.8.12", {"start": v(136.93, 201.9) * mm, "end": v(137.41, 201.41) * mm});
            skLineSegment(sketch, "E19.6.8.13", {"start": v(153.9, 199.07) * mm, "end": v(153.41, 198.59) * mm});
            skLineSegment(sketch, "E19.6.8.14", {"start": v(153.41, 185.41) * mm, "end": v(153.9, 184.93) * mm});
            skLineSegment(sketch, "E19.6.8.15", {"start": v(151.07, 201.9) * mm, "end": v(150.59, 201.41) * mm});
            skLineSegment(sketch, "E19.6.8.16", {"start": v(134.1, 199.07) * mm, "end": v(134.59, 198.59) * mm});
            skLineSegment(sketch, "E19.6.8.17", {"start": v(134.59, 185.41) * mm, "end": v(134.1, 184.93) * mm});
            skLineSegment(sketch, "E19.6.8.18", {"start": v(136.93, 182.1) * mm, "end": v(137.41, 182.59) * mm});
            skCircle(sketch, "E19.7.0.0", {"center": v(180, -0.75) * mm, "radius": 2 * mm});
            skArc(sketch, "E19.7.0.1", {"start": v(177.41, -6.59) * mm, "mid": v(174.59, -6.59) * mm, "end": v(174.59, -9.41) * mm});
            skArc(sketch, "E19.7.0.2", {"start": v(158.1, 7.07) * mm, "mid": v(158.1, 9.9) * mm, "end": v(160.93, 9.9) * mm});
            skArc(sketch, "E19.7.0.3", {"start": v(161.41, -9.41) * mm, "mid": v(161.41, -6.59) * mm, "end": v(158.59, -6.59) * mm});
            skCircle(sketch, "E19.7.0.4", {"center": v(168, 12) * mm, "radius": 2 * mm});
            skArc(sketch, "E19.7.0.5", {"start": v(174.59, 9.41) * mm, "mid": v(174.59, 6.59) * mm, "end": v(177.41, 6.59) * mm});
            skArc(sketch, "E19.7.0.6", {"start": v(158.59, 6.59) * mm, "mid": v(161.41, 6.59) * mm, "end": v(161.41, 9.41) * mm});
            skCircle(sketch, "E19.7.0.7", {"center": v(168, 0) * mm, "radius": 7 * mm});
            skArc(sketch, "E19.7.0.8", {"start": v(177.9, 7.07) * mm, "mid": v(177.9, 9.9) * mm, "end": v(175.07, 9.9) * mm});
            skArc(sketch, "E19.7.0.9", {"start": v(175.07, -9.9) * mm, "mid": v(177.9, -9.9) * mm, "end": v(177.9, -7.07) * mm});
            skArc(sketch, "E19.7.0.10", {"start": v(158.1, -7.07) * mm, "mid": v(158.1, -9.9) * mm, "end": v(160.93, -9.9) * mm});
            skLineSegment(sketch, "E19.7.0.11", {"start": v(175.07, -9.9) * mm, "end": v(174.59, -9.41) * mm});
            skLineSegment(sketch, "E19.7.0.12", {"start": v(160.93, 9.9) * mm, "end": v(161.41, 9.41) * mm});
            skLineSegment(sketch, "E19.7.0.13", {"start": v(177.9, 7.07) * mm, "end": v(177.41, 6.59) * mm});
            skLineSegment(sketch, "E19.7.0.14", {"start": v(177.41, -6.59) * mm, "end": v(177.9, -7.07) * mm});
            skLineSegment(sketch, "E19.7.0.15", {"start": v(175.07, 9.9) * mm, "end": v(174.59, 9.41) * mm});
            skLineSegment(sketch, "E19.7.0.16", {"start": v(158.1, 7.07) * mm, "end": v(158.59, 6.59) * mm});
            skLineSegment(sketch, "E19.7.0.17", {"start": v(158.59, -6.59) * mm, "end": v(158.1, -7.07) * mm});
            skLineSegment(sketch, "E19.7.0.18", {"start": v(160.93, -9.9) * mm, "end": v(161.41, -9.41) * mm});
            skCircle(sketch, "E19.7.1.0", {"center": v(180, 23.25) * mm, "radius": 2 * mm});
            skArc(sketch, "E19.7.1.1", {"start": v(177.41, 17.41) * mm, "mid": v(174.59, 17.41) * mm, "end": v(174.59, 14.59) * mm});
            skArc(sketch, "E19.7.1.2", {"start": v(158.1, 31.07) * mm, "mid": v(158.1, 33.9) * mm, "end": v(160.93, 33.9) * mm});
            skArc(sketch, "E19.7.1.3", {"start": v(161.41, 14.59) * mm, "mid": v(161.41, 17.41) * mm, "end": v(158.59, 17.41) * mm});
            skCircle(sketch, "E19.7.1.4", {"center": v(168, 36) * mm, "radius": 2 * mm});
            skArc(sketch, "E19.7.1.5", {"start": v(174.59, 33.41) * mm, "mid": v(174.59, 30.59) * mm, "end": v(177.41, 30.59) * mm});
            skArc(sketch, "E19.7.1.6", {"start": v(158.59, 30.59) * mm, "mid": v(161.41, 30.59) * mm, "end": v(161.41, 33.41) * mm});
            skCircle(sketch, "E19.7.1.7", {"center": v(168, 24) * mm, "radius": 7 * mm});
            skArc(sketch, "E19.7.1.8", {"start": v(177.9, 31.07) * mm, "mid": v(177.9, 33.9) * mm, "end": v(175.07, 33.9) * mm});
            skArc(sketch, "E19.7.1.9", {"start": v(175.07, 14.1) * mm, "mid": v(177.9, 14.1) * mm, "end": v(177.9, 16.93) * mm});
            skArc(sketch, "E19.7.1.10", {"start": v(158.1, 16.93) * mm, "mid": v(158.1, 14.1) * mm, "end": v(160.93, 14.1) * mm});
            skLineSegment(sketch, "E19.7.1.11", {"start": v(175.07, 14.1) * mm, "end": v(174.59, 14.59) * mm});
            skLineSegment(sketch, "E19.7.1.12", {"start": v(160.93, 33.9) * mm, "end": v(161.41, 33.41) * mm});
            skLineSegment(sketch, "E19.7.1.13", {"start": v(177.9, 31.07) * mm, "end": v(177.41, 30.59) * mm});
            skLineSegment(sketch, "E19.7.1.14", {"start": v(177.41, 17.41) * mm, "end": v(177.9, 16.93) * mm});
            skLineSegment(sketch, "E19.7.1.15", {"start": v(175.07, 33.9) * mm, "end": v(174.59, 33.41) * mm});
            skLineSegment(sketch, "E19.7.1.16", {"start": v(158.1, 31.07) * mm, "end": v(158.59, 30.59) * mm});
            skLineSegment(sketch, "E19.7.1.17", {"start": v(158.59, 17.41) * mm, "end": v(158.1, 16.93) * mm});
            skLineSegment(sketch, "E19.7.1.18", {"start": v(160.93, 14.1) * mm, "end": v(161.41, 14.59) * mm});
            skCircle(sketch, "E19.7.2.0", {"center": v(180, 47.25) * mm, "radius": 2 * mm});
            skArc(sketch, "E19.7.2.1", {"start": v(177.41, 41.41) * mm, "mid": v(174.59, 41.41) * mm, "end": v(174.59, 38.59) * mm});
            skArc(sketch, "E19.7.2.2", {"start": v(158.1, 55.07) * mm, "mid": v(158.1, 57.9) * mm, "end": v(160.93, 57.9) * mm});
            skArc(sketch, "E19.7.2.3", {"start": v(161.41, 38.59) * mm, "mid": v(161.41, 41.41) * mm, "end": v(158.59, 41.41) * mm});
            skCircle(sketch, "E19.7.2.4", {"center": v(168, 60) * mm, "radius": 2 * mm});
            skArc(sketch, "E19.7.2.5", {"start": v(174.59, 57.41) * mm, "mid": v(174.59, 54.59) * mm, "end": v(177.41, 54.59) * mm});
            skArc(sketch, "E19.7.2.6", {"start": v(158.59, 54.59) * mm, "mid": v(161.41, 54.59) * mm, "end": v(161.41, 57.41) * mm});
            skCircle(sketch, "E19.7.2.7", {"center": v(168, 48) * mm, "radius": 7 * mm});
            skArc(sketch, "E19.7.2.8", {"start": v(177.9, 55.07) * mm, "mid": v(177.9, 57.9) * mm, "end": v(175.07, 57.9) * mm});
            skArc(sketch, "E19.7.2.9", {"start": v(175.07, 38.1) * mm, "mid": v(177.9, 38.1) * mm, "end": v(177.9, 40.93) * mm});
            skArc(sketch, "E19.7.2.10", {"start": v(158.1, 40.93) * mm, "mid": v(158.1, 38.1) * mm, "end": v(160.93, 38.1) * mm});
            skLineSegment(sketch, "E19.7.2.11", {"start": v(175.07, 38.1) * mm, "end": v(174.59, 38.59) * mm});
            skLineSegment(sketch, "E19.7.2.12", {"start": v(160.93, 57.9) * mm, "end": v(161.41, 57.41) * mm});
            skLineSegment(sketch, "E19.7.2.13", {"start": v(177.9, 55.07) * mm, "end": v(177.41, 54.59) * mm});
            skLineSegment(sketch, "E19.7.2.14", {"start": v(177.41, 41.41) * mm, "end": v(177.9, 40.93) * mm});
            skLineSegment(sketch, "E19.7.2.15", {"start": v(175.07, 57.9) * mm, "end": v(174.59, 57.41) * mm});
            skLineSegment(sketch, "E19.7.2.16", {"start": v(158.1, 55.07) * mm, "end": v(158.59, 54.59) * mm});
            skLineSegment(sketch, "E19.7.2.17", {"start": v(158.59, 41.41) * mm, "end": v(158.1, 40.93) * mm});
            skLineSegment(sketch, "E19.7.2.18", {"start": v(160.93, 38.1) * mm, "end": v(161.41, 38.59) * mm});
            skCircle(sketch, "E19.7.3.0", {"center": v(180, 71.25) * mm, "radius": 2 * mm});
            skArc(sketch, "E19.7.3.1", {"start": v(177.41, 65.41) * mm, "mid": v(174.59, 65.41) * mm, "end": v(174.59, 62.59) * mm});
            skArc(sketch, "E19.7.3.2", {"start": v(158.1, 79.07) * mm, "mid": v(158.1, 81.9) * mm, "end": v(160.93, 81.9) * mm});
            skArc(sketch, "E19.7.3.3", {"start": v(161.41, 62.59) * mm, "mid": v(161.41, 65.41) * mm, "end": v(158.59, 65.41) * mm});
            skCircle(sketch, "E19.7.3.4", {"center": v(168, 84) * mm, "radius": 2 * mm});
            skArc(sketch, "E19.7.3.5", {"start": v(174.59, 81.41) * mm, "mid": v(174.59, 78.59) * mm, "end": v(177.41, 78.59) * mm});
            skArc(sketch, "E19.7.3.6", {"start": v(158.59, 78.59) * mm, "mid": v(161.41, 78.59) * mm, "end": v(161.41, 81.41) * mm});
            skCircle(sketch, "E19.7.3.7", {"center": v(168, 72) * mm, "radius": 7 * mm});
            skArc(sketch, "E19.7.3.8", {"start": v(177.9, 79.07) * mm, "mid": v(177.9, 81.9) * mm, "end": v(175.07, 81.9) * mm});
            skArc(sketch, "E19.7.3.9", {"start": v(175.07, 62.1) * mm, "mid": v(177.9, 62.1) * mm, "end": v(177.9, 64.93) * mm});
            skArc(sketch, "E19.7.3.10", {"start": v(158.1, 64.93) * mm, "mid": v(158.1, 62.1) * mm, "end": v(160.93, 62.1) * mm});
            skLineSegment(sketch, "E19.7.3.11", {"start": v(175.07, 62.1) * mm, "end": v(174.59, 62.59) * mm});
            skLineSegment(sketch, "E19.7.3.12", {"start": v(160.93, 81.9) * mm, "end": v(161.41, 81.41) * mm});
            skLineSegment(sketch, "E19.7.3.13", {"start": v(177.9, 79.07) * mm, "end": v(177.41, 78.59) * mm});
            skLineSegment(sketch, "E19.7.3.14", {"start": v(177.41, 65.41) * mm, "end": v(177.9, 64.93) * mm});
            skLineSegment(sketch, "E19.7.3.15", {"start": v(175.07, 81.9) * mm, "end": v(174.59, 81.41) * mm});
            skLineSegment(sketch, "E19.7.3.16", {"start": v(158.1, 79.07) * mm, "end": v(158.59, 78.59) * mm});
            skLineSegment(sketch, "E19.7.3.17", {"start": v(158.59, 65.41) * mm, "end": v(158.1, 64.93) * mm});
            skLineSegment(sketch, "E19.7.3.18", {"start": v(160.93, 62.1) * mm, "end": v(161.41, 62.59) * mm});
            skCircle(sketch, "E19.7.4.0", {"center": v(180, 95.25) * mm, "radius": 2 * mm});
            skArc(sketch, "E19.7.4.1", {"start": v(177.41, 89.41) * mm, "mid": v(174.59, 89.41) * mm, "end": v(174.59, 86.59) * mm});
            skArc(sketch, "E19.7.4.2", {"start": v(158.1, 103.07) * mm, "mid": v(158.1, 105.9) * mm, "end": v(160.93, 105.9) * mm});
            skArc(sketch, "E19.7.4.3", {"start": v(161.41, 86.59) * mm, "mid": v(161.41, 89.41) * mm, "end": v(158.59, 89.41) * mm});
            skCircle(sketch, "E19.7.4.4", {"center": v(168, 108) * mm, "radius": 2 * mm});
            skArc(sketch, "E19.7.4.5", {"start": v(174.59, 105.41) * mm, "mid": v(174.59, 102.59) * mm, "end": v(177.41, 102.59) * mm});
            skArc(sketch, "E19.7.4.6", {"start": v(158.59, 102.59) * mm, "mid": v(161.41, 102.59) * mm, "end": v(161.41, 105.41) * mm});
            skCircle(sketch, "E19.7.4.7", {"center": v(168, 96) * mm, "radius": 7 * mm});
            skArc(sketch, "E19.7.4.8", {"start": v(177.9, 103.07) * mm, "mid": v(177.9, 105.9) * mm, "end": v(175.07, 105.9) * mm});
            skArc(sketch, "E19.7.4.9", {"start": v(175.07, 86.1) * mm, "mid": v(177.9, 86.1) * mm, "end": v(177.9, 88.93) * mm});
            skArc(sketch, "E19.7.4.10", {"start": v(158.1, 88.93) * mm, "mid": v(158.1, 86.1) * mm, "end": v(160.93, 86.1) * mm});
            skLineSegment(sketch, "E19.7.4.11", {"start": v(175.07, 86.1) * mm, "end": v(174.59, 86.59) * mm});
            skLineSegment(sketch, "E19.7.4.12", {"start": v(160.93, 105.9) * mm, "end": v(161.41, 105.41) * mm});
            skLineSegment(sketch, "E19.7.4.13", {"start": v(177.9, 103.07) * mm, "end": v(177.41, 102.59) * mm});
            skLineSegment(sketch, "E19.7.4.14", {"start": v(177.41, 89.41) * mm, "end": v(177.9, 88.93) * mm});
            skLineSegment(sketch, "E19.7.4.15", {"start": v(175.07, 105.9) * mm, "end": v(174.59, 105.41) * mm});
            skLineSegment(sketch, "E19.7.4.16", {"start": v(158.1, 103.07) * mm, "end": v(158.59, 102.59) * mm});
            skLineSegment(sketch, "E19.7.4.17", {"start": v(158.59, 89.41) * mm, "end": v(158.1, 88.93) * mm});
            skLineSegment(sketch, "E19.7.4.18", {"start": v(160.93, 86.1) * mm, "end": v(161.41, 86.59) * mm});
            skCircle(sketch, "E19.7.5.0", {"center": v(180, 119.25) * mm, "radius": 2 * mm});
            skArc(sketch, "E19.7.5.1", {"start": v(177.41, 113.41) * mm, "mid": v(174.59, 113.41) * mm, "end": v(174.59, 110.59) * mm});
            skArc(sketch, "E19.7.5.2", {"start": v(158.1, 127.07) * mm, "mid": v(158.1, 129.9) * mm, "end": v(160.93, 129.9) * mm});
            skArc(sketch, "E19.7.5.3", {"start": v(161.41, 110.59) * mm, "mid": v(161.41, 113.41) * mm, "end": v(158.59, 113.41) * mm});
            skCircle(sketch, "E19.7.5.4", {"center": v(168, 132) * mm, "radius": 2 * mm});
            skArc(sketch, "E19.7.5.5", {"start": v(174.59, 129.41) * mm, "mid": v(174.59, 126.59) * mm, "end": v(177.41, 126.59) * mm});
            skArc(sketch, "E19.7.5.6", {"start": v(158.59, 126.59) * mm, "mid": v(161.41, 126.59) * mm, "end": v(161.41, 129.41) * mm});
            skCircle(sketch, "E19.7.5.7", {"center": v(168, 120) * mm, "radius": 7 * mm});
            skArc(sketch, "E19.7.5.8", {"start": v(177.9, 127.07) * mm, "mid": v(177.9, 129.9) * mm, "end": v(175.07, 129.9) * mm});
            skArc(sketch, "E19.7.5.9", {"start": v(175.07, 110.1) * mm, "mid": v(177.9, 110.1) * mm, "end": v(177.9, 112.93) * mm});
            skArc(sketch, "E19.7.5.10", {"start": v(158.1, 112.93) * mm, "mid": v(158.1, 110.1) * mm, "end": v(160.93, 110.1) * mm});
            skLineSegment(sketch, "E19.7.5.11", {"start": v(175.07, 110.1) * mm, "end": v(174.59, 110.59) * mm});
            skLineSegment(sketch, "E19.7.5.12", {"start": v(160.93, 129.9) * mm, "end": v(161.41, 129.41) * mm});
            skLineSegment(sketch, "E19.7.5.13", {"start": v(177.9, 127.07) * mm, "end": v(177.41, 126.59) * mm});
            skLineSegment(sketch, "E19.7.5.14", {"start": v(177.41, 113.41) * mm, "end": v(177.9, 112.93) * mm});
            skLineSegment(sketch, "E19.7.5.15", {"start": v(175.07, 129.9) * mm, "end": v(174.59, 129.41) * mm});
            skLineSegment(sketch, "E19.7.5.16", {"start": v(158.1, 127.07) * mm, "end": v(158.59, 126.59) * mm});
            skLineSegment(sketch, "E19.7.5.17", {"start": v(158.59, 113.41) * mm, "end": v(158.1, 112.93) * mm});
            skLineSegment(sketch, "E19.7.5.18", {"start": v(160.93, 110.1) * mm, "end": v(161.41, 110.59) * mm});
            skCircle(sketch, "E19.7.6.0", {"center": v(180, 143.25) * mm, "radius": 2 * mm});
            skArc(sketch, "E19.7.6.1", {"start": v(177.41, 137.41) * mm, "mid": v(174.59, 137.41) * mm, "end": v(174.59, 134.59) * mm});
            skArc(sketch, "E19.7.6.2", {"start": v(158.1, 151.07) * mm, "mid": v(158.1, 153.9) * mm, "end": v(160.93, 153.9) * mm});
            skArc(sketch, "E19.7.6.3", {"start": v(161.41, 134.59) * mm, "mid": v(161.41, 137.41) * mm, "end": v(158.59, 137.41) * mm});
            skCircle(sketch, "E19.7.6.4", {"center": v(168, 156) * mm, "radius": 2 * mm});
            skArc(sketch, "E19.7.6.5", {"start": v(174.59, 153.41) * mm, "mid": v(174.59, 150.59) * mm, "end": v(177.41, 150.59) * mm});
            skArc(sketch, "E19.7.6.6", {"start": v(158.59, 150.59) * mm, "mid": v(161.41, 150.59) * mm, "end": v(161.41, 153.41) * mm});
            skCircle(sketch, "E19.7.6.7", {"center": v(168, 144) * mm, "radius": 7 * mm});
            skArc(sketch, "E19.7.6.8", {"start": v(177.9, 151.07) * mm, "mid": v(177.9, 153.9) * mm, "end": v(175.07, 153.9) * mm});
            skArc(sketch, "E19.7.6.9", {"start": v(175.07, 134.1) * mm, "mid": v(177.9, 134.1) * mm, "end": v(177.9, 136.93) * mm});
            skArc(sketch, "E19.7.6.10", {"start": v(158.1, 136.93) * mm, "mid": v(158.1, 134.1) * mm, "end": v(160.93, 134.1) * mm});
            skLineSegment(sketch, "E19.7.6.11", {"start": v(175.07, 134.1) * mm, "end": v(174.59, 134.59) * mm});
            skLineSegment(sketch, "E19.7.6.12", {"start": v(160.93, 153.9) * mm, "end": v(161.41, 153.41) * mm});
            skLineSegment(sketch, "E19.7.6.13", {"start": v(177.9, 151.07) * mm, "end": v(177.41, 150.59) * mm});
            skLineSegment(sketch, "E19.7.6.14", {"start": v(177.41, 137.41) * mm, "end": v(177.9, 136.93) * mm});
            skLineSegment(sketch, "E19.7.6.15", {"start": v(175.07, 153.9) * mm, "end": v(174.59, 153.41) * mm});
            skLineSegment(sketch, "E19.7.6.16", {"start": v(158.1, 151.07) * mm, "end": v(158.59, 150.59) * mm});
            skLineSegment(sketch, "E19.7.6.17", {"start": v(158.59, 137.41) * mm, "end": v(158.1, 136.93) * mm});
            skLineSegment(sketch, "E19.7.6.18", {"start": v(160.93, 134.1) * mm, "end": v(161.41, 134.59) * mm});
            skCircle(sketch, "E19.7.7.0", {"center": v(180, 167.25) * mm, "radius": 2 * mm});
            skArc(sketch, "E19.7.7.1", {"start": v(177.41, 161.41) * mm, "mid": v(174.59, 161.41) * mm, "end": v(174.59, 158.59) * mm});
            skArc(sketch, "E19.7.7.2", {"start": v(158.1, 175.07) * mm, "mid": v(158.1, 177.9) * mm, "end": v(160.93, 177.9) * mm});
            skArc(sketch, "E19.7.7.3", {"start": v(161.41, 158.59) * mm, "mid": v(161.41, 161.41) * mm, "end": v(158.59, 161.41) * mm});
            skCircle(sketch, "E19.7.7.4", {"center": v(168, 180) * mm, "radius": 2 * mm});
            skArc(sketch, "E19.7.7.5", {"start": v(174.59, 177.41) * mm, "mid": v(174.59, 174.59) * mm, "end": v(177.41, 174.59) * mm});
            skArc(sketch, "E19.7.7.6", {"start": v(158.59, 174.59) * mm, "mid": v(161.41, 174.59) * mm, "end": v(161.41, 177.41) * mm});
            skCircle(sketch, "E19.7.7.7", {"center": v(168, 168) * mm, "radius": 7 * mm});
            skArc(sketch, "E19.7.7.8", {"start": v(177.9, 175.07) * mm, "mid": v(177.9, 177.9) * mm, "end": v(175.07, 177.9) * mm});
            skArc(sketch, "E19.7.7.9", {"start": v(175.07, 158.1) * mm, "mid": v(177.9, 158.1) * mm, "end": v(177.9, 160.93) * mm});
            skArc(sketch, "E19.7.7.10", {"start": v(158.1, 160.93) * mm, "mid": v(158.1, 158.1) * mm, "end": v(160.93, 158.1) * mm});
            skLineSegment(sketch, "E19.7.7.11", {"start": v(175.07, 158.1) * mm, "end": v(174.59, 158.59) * mm});
            skLineSegment(sketch, "E19.7.7.12", {"start": v(160.93, 177.9) * mm, "end": v(161.41, 177.41) * mm});
            skLineSegment(sketch, "E19.7.7.13", {"start": v(177.9, 175.07) * mm, "end": v(177.41, 174.59) * mm});
            skLineSegment(sketch, "E19.7.7.14", {"start": v(177.41, 161.41) * mm, "end": v(177.9, 160.93) * mm});
            skLineSegment(sketch, "E19.7.7.15", {"start": v(175.07, 177.9) * mm, "end": v(174.59, 177.41) * mm});
            skLineSegment(sketch, "E19.7.7.16", {"start": v(158.1, 175.07) * mm, "end": v(158.59, 174.59) * mm});
            skLineSegment(sketch, "E19.7.7.17", {"start": v(158.59, 161.41) * mm, "end": v(158.1, 160.93) * mm});
            skLineSegment(sketch, "E19.7.7.18", {"start": v(160.93, 158.1) * mm, "end": v(161.41, 158.59) * mm});
            skCircle(sketch, "E19.7.8.0", {"center": v(180, 191.25) * mm, "radius": 2 * mm});
            skArc(sketch, "E19.7.8.1", {"start": v(177.41, 185.41) * mm, "mid": v(174.59, 185.41) * mm, "end": v(174.59, 182.59) * mm});
            skArc(sketch, "E19.7.8.2", {"start": v(158.1, 199.07) * mm, "mid": v(158.1, 201.9) * mm, "end": v(160.93, 201.9) * mm});
            skArc(sketch, "E19.7.8.3", {"start": v(161.41, 182.59) * mm, "mid": v(161.41, 185.41) * mm, "end": v(158.59, 185.41) * mm});
            skCircle(sketch, "E19.7.8.4", {"center": v(168, 204) * mm, "radius": 2 * mm});
            skArc(sketch, "E19.7.8.5", {"start": v(174.59, 201.41) * mm, "mid": v(174.59, 198.59) * mm, "end": v(177.41, 198.59) * mm});
            skArc(sketch, "E19.7.8.6", {"start": v(158.59, 198.59) * mm, "mid": v(161.41, 198.59) * mm, "end": v(161.41, 201.41) * mm});
            skCircle(sketch, "E19.7.8.7", {"center": v(168, 192) * mm, "radius": 7 * mm});
            skArc(sketch, "E19.7.8.8", {"start": v(177.9, 199.07) * mm, "mid": v(177.9, 201.9) * mm, "end": v(175.07, 201.9) * mm});
            skArc(sketch, "E19.7.8.9", {"start": v(175.07, 182.1) * mm, "mid": v(177.9, 182.1) * mm, "end": v(177.9, 184.93) * mm});
            skArc(sketch, "E19.7.8.10", {"start": v(158.1, 184.93) * mm, "mid": v(158.1, 182.1) * mm, "end": v(160.93, 182.1) * mm});
            skLineSegment(sketch, "E19.7.8.11", {"start": v(175.07, 182.1) * mm, "end": v(174.59, 182.59) * mm});
            skLineSegment(sketch, "E19.7.8.12", {"start": v(160.93, 201.9) * mm, "end": v(161.41, 201.41) * mm});
            skLineSegment(sketch, "E19.7.8.13", {"start": v(177.9, 199.07) * mm, "end": v(177.41, 198.59) * mm});
            skLineSegment(sketch, "E19.7.8.14", {"start": v(177.41, 185.41) * mm, "end": v(177.9, 184.93) * mm});
            skLineSegment(sketch, "E19.7.8.15", {"start": v(175.07, 201.9) * mm, "end": v(174.59, 201.41) * mm});
            skLineSegment(sketch, "E19.7.8.16", {"start": v(158.1, 199.07) * mm, "end": v(158.59, 198.59) * mm});
            skLineSegment(sketch, "E19.7.8.17", {"start": v(158.59, 185.41) * mm, "end": v(158.1, 184.93) * mm});
            skLineSegment(sketch, "E19.7.8.18", {"start": v(160.93, 182.1) * mm, "end": v(161.41, 182.59) * mm});
            skCircle(sketch, "E19.8.0.0", {"center": v(204, -0.75) * mm, "radius": 2 * mm});
            skArc(sketch, "E19.8.0.1", {"start": v(201.41, -6.59) * mm, "mid": v(198.59, -6.59) * mm, "end": v(198.59, -9.41) * mm});
            skArc(sketch, "E19.8.0.2", {"start": v(182.1, 7.07) * mm, "mid": v(182.1, 9.9) * mm, "end": v(184.93, 9.9) * mm});
            skArc(sketch, "E19.8.0.3", {"start": v(185.41, -9.41) * mm, "mid": v(185.41, -6.59) * mm, "end": v(182.59, -6.59) * mm});
            skCircle(sketch, "E19.8.0.4", {"center": v(192, 12) * mm, "radius": 2 * mm});
            skArc(sketch, "E19.8.0.5", {"start": v(198.59, 9.41) * mm, "mid": v(198.59, 6.59) * mm, "end": v(201.41, 6.59) * mm});
            skArc(sketch, "E19.8.0.6", {"start": v(182.59, 6.59) * mm, "mid": v(185.41, 6.59) * mm, "end": v(185.41, 9.41) * mm});
            skCircle(sketch, "E19.8.0.7", {"center": v(192, 0) * mm, "radius": 7 * mm});
            skArc(sketch, "E19.8.0.8", {"start": v(201.9, 7.07) * mm, "mid": v(201.9, 9.9) * mm, "end": v(199.07, 9.9) * mm});
            skArc(sketch, "E19.8.0.9", {"start": v(199.07, -9.9) * mm, "mid": v(201.9, -9.9) * mm, "end": v(201.9, -7.07) * mm});
            skArc(sketch, "E19.8.0.10", {"start": v(182.1, -7.07) * mm, "mid": v(182.1, -9.9) * mm, "end": v(184.93, -9.9) * mm});
            skLineSegment(sketch, "E19.8.0.11", {"start": v(199.07, -9.9) * mm, "end": v(198.59, -9.41) * mm});
            skLineSegment(sketch, "E19.8.0.12", {"start": v(184.93, 9.9) * mm, "end": v(185.41, 9.41) * mm});
            skLineSegment(sketch, "E19.8.0.13", {"start": v(201.9, 7.07) * mm, "end": v(201.41, 6.59) * mm});
            skLineSegment(sketch, "E19.8.0.14", {"start": v(201.41, -6.59) * mm, "end": v(201.9, -7.07) * mm});
            skLineSegment(sketch, "E19.8.0.15", {"start": v(199.07, 9.9) * mm, "end": v(198.59, 9.41) * mm});
            skLineSegment(sketch, "E19.8.0.16", {"start": v(182.1, 7.07) * mm, "end": v(182.59, 6.59) * mm});
            skLineSegment(sketch, "E19.8.0.17", {"start": v(182.59, -6.59) * mm, "end": v(182.1, -7.07) * mm});
            skLineSegment(sketch, "E19.8.0.18", {"start": v(184.93, -9.9) * mm, "end": v(185.41, -9.41) * mm});
            skCircle(sketch, "E19.8.1.0", {"center": v(204, 23.25) * mm, "radius": 2 * mm});
            skArc(sketch, "E19.8.1.1", {"start": v(201.41, 17.41) * mm, "mid": v(198.59, 17.41) * mm, "end": v(198.59, 14.59) * mm});
            skArc(sketch, "E19.8.1.2", {"start": v(182.1, 31.07) * mm, "mid": v(182.1, 33.9) * mm, "end": v(184.93, 33.9) * mm});
            skArc(sketch, "E19.8.1.3", {"start": v(185.41, 14.59) * mm, "mid": v(185.41, 17.41) * mm, "end": v(182.59, 17.41) * mm});
            skCircle(sketch, "E19.8.1.4", {"center": v(192, 36) * mm, "radius": 2 * mm});
            skArc(sketch, "E19.8.1.5", {"start": v(198.59, 33.41) * mm, "mid": v(198.59, 30.59) * mm, "end": v(201.41, 30.59) * mm});
            skArc(sketch, "E19.8.1.6", {"start": v(182.59, 30.59) * mm, "mid": v(185.41, 30.59) * mm, "end": v(185.41, 33.41) * mm});
            skCircle(sketch, "E19.8.1.7", {"center": v(192, 24) * mm, "radius": 7 * mm});
            skArc(sketch, "E19.8.1.8", {"start": v(201.9, 31.07) * mm, "mid": v(201.9, 33.9) * mm, "end": v(199.07, 33.9) * mm});
            skArc(sketch, "E19.8.1.9", {"start": v(199.07, 14.1) * mm, "mid": v(201.9, 14.1) * mm, "end": v(201.9, 16.93) * mm});
            skArc(sketch, "E19.8.1.10", {"start": v(182.1, 16.93) * mm, "mid": v(182.1, 14.1) * mm, "end": v(184.93, 14.1) * mm});
            skLineSegment(sketch, "E19.8.1.11", {"start": v(199.07, 14.1) * mm, "end": v(198.59, 14.59) * mm});
            skLineSegment(sketch, "E19.8.1.12", {"start": v(184.93, 33.9) * mm, "end": v(185.41, 33.41) * mm});
            skLineSegment(sketch, "E19.8.1.13", {"start": v(201.9, 31.07) * mm, "end": v(201.41, 30.59) * mm});
            skLineSegment(sketch, "E19.8.1.14", {"start": v(201.41, 17.41) * mm, "end": v(201.9, 16.93) * mm});
            skLineSegment(sketch, "E19.8.1.15", {"start": v(199.07, 33.9) * mm, "end": v(198.59, 33.41) * mm});
            skLineSegment(sketch, "E19.8.1.16", {"start": v(182.1, 31.07) * mm, "end": v(182.59, 30.59) * mm});
            skLineSegment(sketch, "E19.8.1.17", {"start": v(182.59, 17.41) * mm, "end": v(182.1, 16.93) * mm});
            skLineSegment(sketch, "E19.8.1.18", {"start": v(184.93, 14.1) * mm, "end": v(185.41, 14.59) * mm});
            skCircle(sketch, "E19.8.2.0", {"center": v(204, 47.25) * mm, "radius": 2 * mm});
            skArc(sketch, "E19.8.2.1", {"start": v(201.41, 41.41) * mm, "mid": v(198.59, 41.41) * mm, "end": v(198.59, 38.59) * mm});
            skArc(sketch, "E19.8.2.2", {"start": v(182.1, 55.07) * mm, "mid": v(182.1, 57.9) * mm, "end": v(184.93, 57.9) * mm});
            skArc(sketch, "E19.8.2.3", {"start": v(185.41, 38.59) * mm, "mid": v(185.41, 41.41) * mm, "end": v(182.59, 41.41) * mm});
            skCircle(sketch, "E19.8.2.4", {"center": v(192, 60) * mm, "radius": 2 * mm});
            skArc(sketch, "E19.8.2.5", {"start": v(198.59, 57.41) * mm, "mid": v(198.59, 54.59) * mm, "end": v(201.41, 54.59) * mm});
            skArc(sketch, "E19.8.2.6", {"start": v(182.59, 54.59) * mm, "mid": v(185.41, 54.59) * mm, "end": v(185.41, 57.41) * mm});
            skCircle(sketch, "E19.8.2.7", {"center": v(192, 48) * mm, "radius": 7 * mm});
            skArc(sketch, "E19.8.2.8", {"start": v(201.9, 55.07) * mm, "mid": v(201.9, 57.9) * mm, "end": v(199.07, 57.9) * mm});
            skArc(sketch, "E19.8.2.9", {"start": v(199.07, 38.1) * mm, "mid": v(201.9, 38.1) * mm, "end": v(201.9, 40.93) * mm});
            skArc(sketch, "E19.8.2.10", {"start": v(182.1, 40.93) * mm, "mid": v(182.1, 38.1) * mm, "end": v(184.93, 38.1) * mm});
            skLineSegment(sketch, "E19.8.2.11", {"start": v(199.07, 38.1) * mm, "end": v(198.59, 38.59) * mm});
            skLineSegment(sketch, "E19.8.2.12", {"start": v(184.93, 57.9) * mm, "end": v(185.41, 57.41) * mm});
            skLineSegment(sketch, "E19.8.2.13", {"start": v(201.9, 55.07) * mm, "end": v(201.41, 54.59) * mm});
            skLineSegment(sketch, "E19.8.2.14", {"start": v(201.41, 41.41) * mm, "end": v(201.9, 40.93) * mm});
            skLineSegment(sketch, "E19.8.2.15", {"start": v(199.07, 57.9) * mm, "end": v(198.59, 57.41) * mm});
            skLineSegment(sketch, "E19.8.2.16", {"start": v(182.1, 55.07) * mm, "end": v(182.59, 54.59) * mm});
            skLineSegment(sketch, "E19.8.2.17", {"start": v(182.59, 41.41) * mm, "end": v(182.1, 40.93) * mm});
            skLineSegment(sketch, "E19.8.2.18", {"start": v(184.93, 38.1) * mm, "end": v(185.41, 38.59) * mm});
            skCircle(sketch, "E19.8.3.0", {"center": v(204, 71.25) * mm, "radius": 2 * mm});
            skArc(sketch, "E19.8.3.1", {"start": v(201.41, 65.41) * mm, "mid": v(198.59, 65.41) * mm, "end": v(198.59, 62.59) * mm});
            skArc(sketch, "E19.8.3.2", {"start": v(182.1, 79.07) * mm, "mid": v(182.1, 81.9) * mm, "end": v(184.93, 81.9) * mm});
            skArc(sketch, "E19.8.3.3", {"start": v(185.41, 62.59) * mm, "mid": v(185.41, 65.41) * mm, "end": v(182.59, 65.41) * mm});
            skCircle(sketch, "E19.8.3.4", {"center": v(192, 84) * mm, "radius": 2 * mm});
            skArc(sketch, "E19.8.3.5", {"start": v(198.59, 81.41) * mm, "mid": v(198.59, 78.59) * mm, "end": v(201.41, 78.59) * mm});
            skArc(sketch, "E19.8.3.6", {"start": v(182.59, 78.59) * mm, "mid": v(185.41, 78.59) * mm, "end": v(185.41, 81.41) * mm});
            skCircle(sketch, "E19.8.3.7", {"center": v(192, 72) * mm, "radius": 7 * mm});
            skArc(sketch, "E19.8.3.8", {"start": v(201.9, 79.07) * mm, "mid": v(201.9, 81.9) * mm, "end": v(199.07, 81.9) * mm});
            skArc(sketch, "E19.8.3.9", {"start": v(199.07, 62.1) * mm, "mid": v(201.9, 62.1) * mm, "end": v(201.9, 64.93) * mm});
            skArc(sketch, "E19.8.3.10", {"start": v(182.1, 64.93) * mm, "mid": v(182.1, 62.1) * mm, "end": v(184.93, 62.1) * mm});
            skLineSegment(sketch, "E19.8.3.11", {"start": v(199.07, 62.1) * mm, "end": v(198.59, 62.59) * mm});
            skLineSegment(sketch, "E19.8.3.12", {"start": v(184.93, 81.9) * mm, "end": v(185.41, 81.41) * mm});
            skLineSegment(sketch, "E19.8.3.13", {"start": v(201.9, 79.07) * mm, "end": v(201.41, 78.59) * mm});
            skLineSegment(sketch, "E19.8.3.14", {"start": v(201.41, 65.41) * mm, "end": v(201.9, 64.93) * mm});
            skLineSegment(sketch, "E19.8.3.15", {"start": v(199.07, 81.9) * mm, "end": v(198.59, 81.41) * mm});
            skLineSegment(sketch, "E19.8.3.16", {"start": v(182.1, 79.07) * mm, "end": v(182.59, 78.59) * mm});
            skLineSegment(sketch, "E19.8.3.17", {"start": v(182.59, 65.41) * mm, "end": v(182.1, 64.93) * mm});
            skLineSegment(sketch, "E19.8.3.18", {"start": v(184.93, 62.1) * mm, "end": v(185.41, 62.59) * mm});
            skCircle(sketch, "E19.8.4.0", {"center": v(204, 95.25) * mm, "radius": 2 * mm});
            skArc(sketch, "E19.8.4.1", {"start": v(201.41, 89.41) * mm, "mid": v(198.59, 89.41) * mm, "end": v(198.59, 86.59) * mm});
            skArc(sketch, "E19.8.4.2", {"start": v(182.1, 103.07) * mm, "mid": v(182.1, 105.9) * mm, "end": v(184.93, 105.9) * mm});
            skArc(sketch, "E19.8.4.3", {"start": v(185.41, 86.59) * mm, "mid": v(185.41, 89.41) * mm, "end": v(182.59, 89.41) * mm});
            skCircle(sketch, "E19.8.4.4", {"center": v(192, 108) * mm, "radius": 2 * mm});
            skArc(sketch, "E19.8.4.5", {"start": v(198.59, 105.41) * mm, "mid": v(198.59, 102.59) * mm, "end": v(201.41, 102.59) * mm});
            skArc(sketch, "E19.8.4.6", {"start": v(182.59, 102.59) * mm, "mid": v(185.41, 102.59) * mm, "end": v(185.41, 105.41) * mm});
            skCircle(sketch, "E19.8.4.7", {"center": v(192, 96) * mm, "radius": 7 * mm});
            skArc(sketch, "E19.8.4.8", {"start": v(201.9, 103.07) * mm, "mid": v(201.9, 105.9) * mm, "end": v(199.07, 105.9) * mm});
            skArc(sketch, "E19.8.4.9", {"start": v(199.07, 86.1) * mm, "mid": v(201.9, 86.1) * mm, "end": v(201.9, 88.93) * mm});
            skArc(sketch, "E19.8.4.10", {"start": v(182.1, 88.93) * mm, "mid": v(182.1, 86.1) * mm, "end": v(184.93, 86.1) * mm});
            skLineSegment(sketch, "E19.8.4.11", {"start": v(199.07, 86.1) * mm, "end": v(198.59, 86.59) * mm});
            skLineSegment(sketch, "E19.8.4.12", {"start": v(184.93, 105.9) * mm, "end": v(185.41, 105.41) * mm});
            skLineSegment(sketch, "E19.8.4.13", {"start": v(201.9, 103.07) * mm, "end": v(201.41, 102.59) * mm});
            skLineSegment(sketch, "E19.8.4.14", {"start": v(201.41, 89.41) * mm, "end": v(201.9, 88.93) * mm});
            skLineSegment(sketch, "E19.8.4.15", {"start": v(199.07, 105.9) * mm, "end": v(198.59, 105.41) * mm});
            skLineSegment(sketch, "E19.8.4.16", {"start": v(182.1, 103.07) * mm, "end": v(182.59, 102.59) * mm});
            skLineSegment(sketch, "E19.8.4.17", {"start": v(182.59, 89.41) * mm, "end": v(182.1, 88.93) * mm});
            skLineSegment(sketch, "E19.8.4.18", {"start": v(184.93, 86.1) * mm, "end": v(185.41, 86.59) * mm});
            skCircle(sketch, "E19.8.5.0", {"center": v(204, 119.25) * mm, "radius": 2 * mm});
            skArc(sketch, "E19.8.5.1", {"start": v(201.41, 113.41) * mm, "mid": v(198.59, 113.41) * mm, "end": v(198.59, 110.59) * mm});
            skArc(sketch, "E19.8.5.2", {"start": v(182.1, 127.07) * mm, "mid": v(182.1, 129.9) * mm, "end": v(184.93, 129.9) * mm});
            skArc(sketch, "E19.8.5.3", {"start": v(185.41, 110.59) * mm, "mid": v(185.41, 113.41) * mm, "end": v(182.59, 113.41) * mm});
            skCircle(sketch, "E19.8.5.4", {"center": v(192, 132) * mm, "radius": 2 * mm});
            skArc(sketch, "E19.8.5.5", {"start": v(198.59, 129.41) * mm, "mid": v(198.59, 126.59) * mm, "end": v(201.41, 126.59) * mm});
            skArc(sketch, "E19.8.5.6", {"start": v(182.59, 126.59) * mm, "mid": v(185.41, 126.59) * mm, "end": v(185.41, 129.41) * mm});
            skCircle(sketch, "E19.8.5.7", {"center": v(192, 120) * mm, "radius": 7 * mm});
            skArc(sketch, "E19.8.5.8", {"start": v(201.9, 127.07) * mm, "mid": v(201.9, 129.9) * mm, "end": v(199.07, 129.9) * mm});
            skArc(sketch, "E19.8.5.9", {"start": v(199.07, 110.1) * mm, "mid": v(201.9, 110.1) * mm, "end": v(201.9, 112.93) * mm});
            skArc(sketch, "E19.8.5.10", {"start": v(182.1, 112.93) * mm, "mid": v(182.1, 110.1) * mm, "end": v(184.93, 110.1) * mm});
            skLineSegment(sketch, "E19.8.5.11", {"start": v(199.07, 110.1) * mm, "end": v(198.59, 110.59) * mm});
            skLineSegment(sketch, "E19.8.5.12", {"start": v(184.93, 129.9) * mm, "end": v(185.41, 129.41) * mm});
            skLineSegment(sketch, "E19.8.5.13", {"start": v(201.9, 127.07) * mm, "end": v(201.41, 126.59) * mm});
            skLineSegment(sketch, "E19.8.5.14", {"start": v(201.41, 113.41) * mm, "end": v(201.9, 112.93) * mm});
            skLineSegment(sketch, "E19.8.5.15", {"start": v(199.07, 129.9) * mm, "end": v(198.59, 129.41) * mm});
            skLineSegment(sketch, "E19.8.5.16", {"start": v(182.1, 127.07) * mm, "end": v(182.59, 126.59) * mm});
            skLineSegment(sketch, "E19.8.5.17", {"start": v(182.59, 113.41) * mm, "end": v(182.1, 112.93) * mm});
            skLineSegment(sketch, "E19.8.5.18", {"start": v(184.93, 110.1) * mm, "end": v(185.41, 110.59) * mm});
            skCircle(sketch, "E19.8.6.0", {"center": v(204, 143.25) * mm, "radius": 2 * mm});
            skArc(sketch, "E19.8.6.1", {"start": v(201.41, 137.41) * mm, "mid": v(198.59, 137.41) * mm, "end": v(198.59, 134.59) * mm});
            skArc(sketch, "E19.8.6.2", {"start": v(182.1, 151.07) * mm, "mid": v(182.1, 153.9) * mm, "end": v(184.93, 153.9) * mm});
            skArc(sketch, "E19.8.6.3", {"start": v(185.41, 134.59) * mm, "mid": v(185.41, 137.41) * mm, "end": v(182.59, 137.41) * mm});
            skCircle(sketch, "E19.8.6.4", {"center": v(192, 156) * mm, "radius": 2 * mm});
            skArc(sketch, "E19.8.6.5", {"start": v(198.59, 153.41) * mm, "mid": v(198.59, 150.59) * mm, "end": v(201.41, 150.59) * mm});
            skArc(sketch, "E19.8.6.6", {"start": v(182.59, 150.59) * mm, "mid": v(185.41, 150.59) * mm, "end": v(185.41, 153.41) * mm});
            skCircle(sketch, "E19.8.6.7", {"center": v(192, 144) * mm, "radius": 7 * mm});
            skArc(sketch, "E19.8.6.8", {"start": v(201.9, 151.07) * mm, "mid": v(201.9, 153.9) * mm, "end": v(199.07, 153.9) * mm});
            skArc(sketch, "E19.8.6.9", {"start": v(199.07, 134.1) * mm, "mid": v(201.9, 134.1) * mm, "end": v(201.9, 136.93) * mm});
            skArc(sketch, "E19.8.6.10", {"start": v(182.1, 136.93) * mm, "mid": v(182.1, 134.1) * mm, "end": v(184.93, 134.1) * mm});
            skLineSegment(sketch, "E19.8.6.11", {"start": v(199.07, 134.1) * mm, "end": v(198.59, 134.59) * mm});
            skLineSegment(sketch, "E19.8.6.12", {"start": v(184.93, 153.9) * mm, "end": v(185.41, 153.41) * mm});
            skLineSegment(sketch, "E19.8.6.13", {"start": v(201.9, 151.07) * mm, "end": v(201.41, 150.59) * mm});
            skLineSegment(sketch, "E19.8.6.14", {"start": v(201.41, 137.41) * mm, "end": v(201.9, 136.93) * mm});
            skLineSegment(sketch, "E19.8.6.15", {"start": v(199.07, 153.9) * mm, "end": v(198.59, 153.41) * mm});
            skLineSegment(sketch, "E19.8.6.16", {"start": v(182.1, 151.07) * mm, "end": v(182.59, 150.59) * mm});
            skLineSegment(sketch, "E19.8.6.17", {"start": v(182.59, 137.41) * mm, "end": v(182.1, 136.93) * mm});
            skLineSegment(sketch, "E19.8.6.18", {"start": v(184.93, 134.1) * mm, "end": v(185.41, 134.59) * mm});
            skCircle(sketch, "E19.8.7.0", {"center": v(204, 167.25) * mm, "radius": 2 * mm});
            skArc(sketch, "E19.8.7.1", {"start": v(201.41, 161.41) * mm, "mid": v(198.59, 161.41) * mm, "end": v(198.59, 158.59) * mm});
            skArc(sketch, "E19.8.7.2", {"start": v(182.1, 175.07) * mm, "mid": v(182.1, 177.9) * mm, "end": v(184.93, 177.9) * mm});
            skArc(sketch, "E19.8.7.3", {"start": v(185.41, 158.59) * mm, "mid": v(185.41, 161.41) * mm, "end": v(182.59, 161.41) * mm});
            skCircle(sketch, "E19.8.7.4", {"center": v(192, 180) * mm, "radius": 2 * mm});
            skArc(sketch, "E19.8.7.5", {"start": v(198.59, 177.41) * mm, "mid": v(198.59, 174.59) * mm, "end": v(201.41, 174.59) * mm});
            skArc(sketch, "E19.8.7.6", {"start": v(182.59, 174.59) * mm, "mid": v(185.41, 174.59) * mm, "end": v(185.41, 177.41) * mm});
            skCircle(sketch, "E19.8.7.7", {"center": v(192, 168) * mm, "radius": 7 * mm});
            skArc(sketch, "E19.8.7.8", {"start": v(201.9, 175.07) * mm, "mid": v(201.9, 177.9) * mm, "end": v(199.07, 177.9) * mm});
            skArc(sketch, "E19.8.7.9", {"start": v(199.07, 158.1) * mm, "mid": v(201.9, 158.1) * mm, "end": v(201.9, 160.93) * mm});
            skArc(sketch, "E19.8.7.10", {"start": v(182.1, 160.93) * mm, "mid": v(182.1, 158.1) * mm, "end": v(184.93, 158.1) * mm});
            skLineSegment(sketch, "E19.8.7.11", {"start": v(199.07, 158.1) * mm, "end": v(198.59, 158.59) * mm});
            skLineSegment(sketch, "E19.8.7.12", {"start": v(184.93, 177.9) * mm, "end": v(185.41, 177.41) * mm});
            skLineSegment(sketch, "E19.8.7.13", {"start": v(201.9, 175.07) * mm, "end": v(201.41, 174.59) * mm});
            skLineSegment(sketch, "E19.8.7.14", {"start": v(201.41, 161.41) * mm, "end": v(201.9, 160.93) * mm});
            skLineSegment(sketch, "E19.8.7.15", {"start": v(199.07, 177.9) * mm, "end": v(198.59, 177.41) * mm});
            skLineSegment(sketch, "E19.8.7.16", {"start": v(182.1, 175.07) * mm, "end": v(182.59, 174.59) * mm});
            skLineSegment(sketch, "E19.8.7.17", {"start": v(182.59, 161.41) * mm, "end": v(182.1, 160.93) * mm});
            skLineSegment(sketch, "E19.8.7.18", {"start": v(184.93, 158.1) * mm, "end": v(185.41, 158.59) * mm});
            skCircle(sketch, "E19.8.8.0", {"center": v(204, 191.25) * mm, "radius": 2 * mm});
            skArc(sketch, "E19.8.8.1", {"start": v(201.41, 185.41) * mm, "mid": v(198.59, 185.41) * mm, "end": v(198.59, 182.59) * mm});
            skArc(sketch, "E19.8.8.2", {"start": v(182.1, 199.07) * mm, "mid": v(182.1, 201.9) * mm, "end": v(184.93, 201.9) * mm});
            skArc(sketch, "E19.8.8.3", {"start": v(185.41, 182.59) * mm, "mid": v(185.41, 185.41) * mm, "end": v(182.59, 185.41) * mm});
            skCircle(sketch, "E19.8.8.4", {"center": v(192, 204) * mm, "radius": 2 * mm});
            skArc(sketch, "E19.8.8.5", {"start": v(198.59, 201.41) * mm, "mid": v(198.59, 198.59) * mm, "end": v(201.41, 198.59) * mm});
            skArc(sketch, "E19.8.8.6", {"start": v(182.59, 198.59) * mm, "mid": v(185.41, 198.59) * mm, "end": v(185.41, 201.41) * mm});
            skCircle(sketch, "E19.8.8.7", {"center": v(192, 192) * mm, "radius": 7 * mm});
            skArc(sketch, "E19.8.8.8", {"start": v(201.9, 199.07) * mm, "mid": v(201.9, 201.9) * mm, "end": v(199.07, 201.9) * mm});
            skArc(sketch, "E19.8.8.9", {"start": v(199.07, 182.1) * mm, "mid": v(201.9, 182.1) * mm, "end": v(201.9, 184.93) * mm});
            skArc(sketch, "E19.8.8.10", {"start": v(182.1, 184.93) * mm, "mid": v(182.1, 182.1) * mm, "end": v(184.93, 182.1) * mm});
            skLineSegment(sketch, "E19.8.8.11", {"start": v(199.07, 182.1) * mm, "end": v(198.59, 182.59) * mm});
            skLineSegment(sketch, "E19.8.8.12", {"start": v(184.93, 201.9) * mm, "end": v(185.41, 201.41) * mm});
            skLineSegment(sketch, "E19.8.8.13", {"start": v(201.9, 199.07) * mm, "end": v(201.41, 198.59) * mm});
            skLineSegment(sketch, "E19.8.8.14", {"start": v(201.41, 185.41) * mm, "end": v(201.9, 184.93) * mm});
            skLineSegment(sketch, "E19.8.8.15", {"start": v(199.07, 201.9) * mm, "end": v(198.59, 201.41) * mm});
            skLineSegment(sketch, "E19.8.8.16", {"start": v(182.1, 199.07) * mm, "end": v(182.59, 198.59) * mm});
            skLineSegment(sketch, "E19.8.8.17", {"start": v(182.59, 185.41) * mm, "end": v(182.1, 184.93) * mm});
            skLineSegment(sketch, "E19.8.8.18", {"start": v(184.93, 182.1) * mm, "end": v(185.41, 182.59) * mm});
            skLineSegment(sketch, "E19.direction1", {"start": v(-7.07, -9.9) * mm, "end": v(16.93, -9.9) * mm, "construction": true});
            skLineSegment(sketch, "E19.direction2", {"start": v(-7.07, -9.9) * mm, "end": v(-7.07, 14.1) * mm, "construction": true});
            skSolve(sketch);
        }
        {
            var Q0;
            Q0 = qSketchRegion(id + "F0", true);
            extrude(context, id + "F1", {"entities" : qUnion([Q0]), "depth" : 25 * mm, "offsetDistance" : 25 * mm});
        }
        {
            var Q0;
            Q0=makeQuery(id+"F1.opExtrude","CAP_FACE",FACE,{"disambiguationData":[OSD([sQuery(id+"F0.wireOp",EDGE,"E19.4.4.7")])],"isStart":true});
            var sketch = newSketch(context, id + "F2", { "sketchPlane" : qUnion([Q0])});
            skCircle(sketch, "E20", {"center": v(-96, 96) * mm, "radius": 110 * mm});
            skSolve(sketch);
        }
        {
            var Q0;
            Q0 = qSketchRegion(id + "F2", true);
            extrude(context, id + "F3", {"entities" : qUnion([Q0]), "operationType" : NewBodyOperationType.INTERSECT, "oppositeDirection" : true, "depth" : 25 * mm, "offsetDistance" : 25 * mm});
        }
    });
